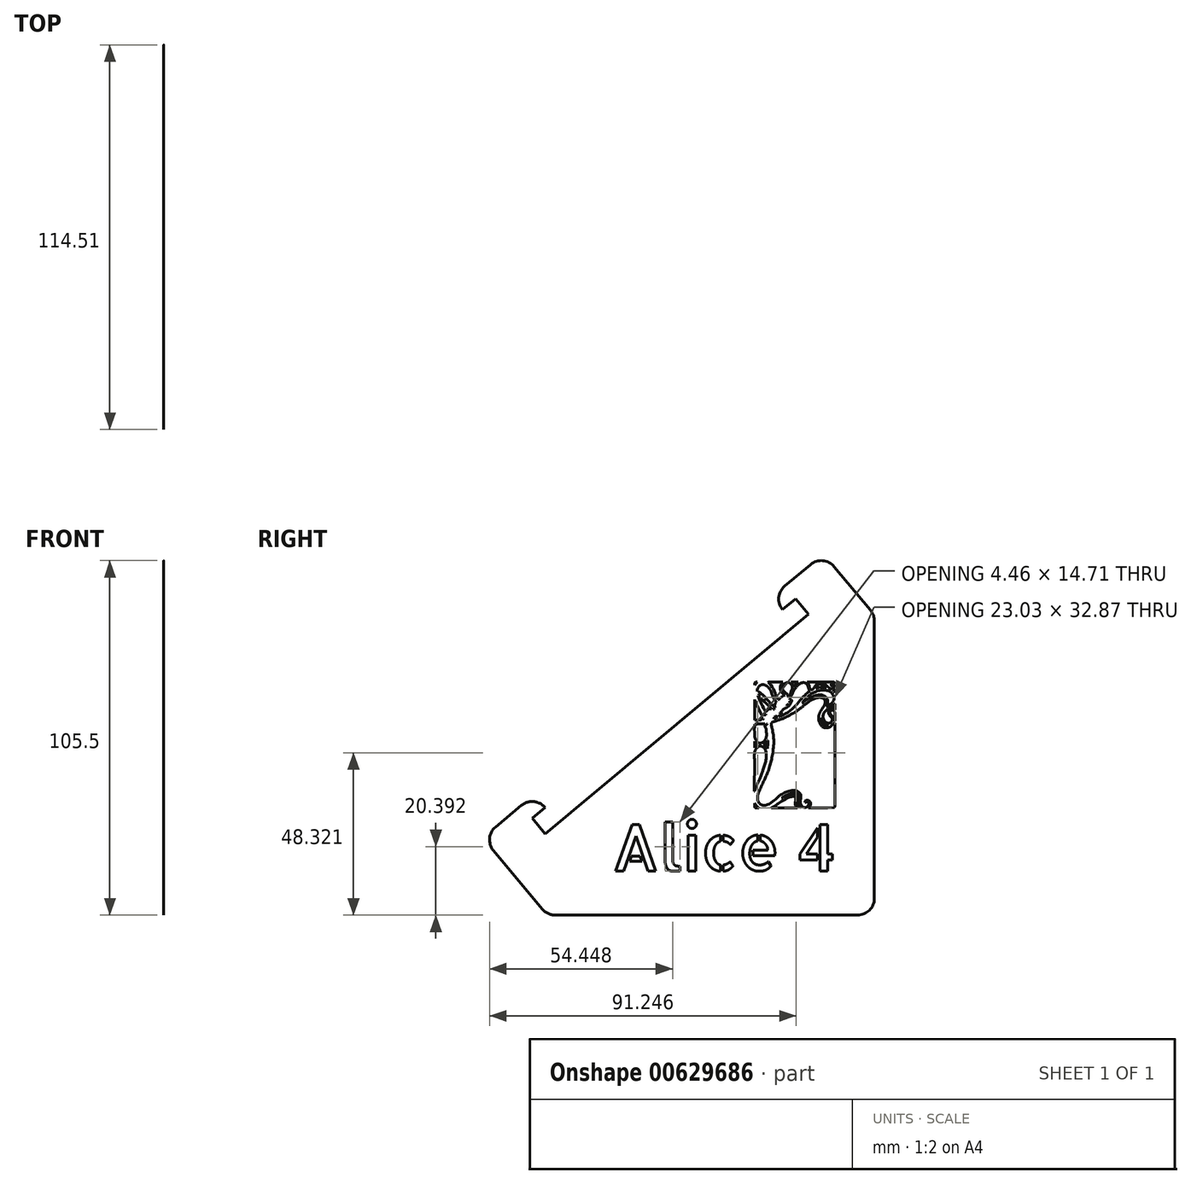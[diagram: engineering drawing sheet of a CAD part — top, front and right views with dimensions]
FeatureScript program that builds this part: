
annotation { "Feature Type Name" : "Feature", "Feature Type Description" : "" }
export const myFeature = defineFeature(function(context is Context, id is Id, definition is map)
    precondition{}
    {
        {
            var Q0;
            Q0=qCreatedBy(makeId("Right.planeOp"),FACE);
            var sketch = newSketch(context, id + "F0", { "sketchPlane" : qUnion([Q0])});
            skLineSegment(sketch, "E0", {"start": v(-36.5, -38.06) * mm, "end": v(41.85, 27.24) * mm});
            skLineSegment(sketch, "E1", {"start": v(41.85, 27.24) * mm, "end": v(38.01, 31.85) * mm});
            skLineSegment(sketch, "E2", {"start": v(38.01, 31.85) * mm, "end": v(34.17, 28.65) * mm});
            skLineSegment(sketch, "E3", {"start": v(34.17, 28.65) * mm, "end": v(34.17, 28.65) * mm});
            skLineSegment(sketch, "E4", {"start": v(-36.5, -38.06) * mm, "end": v(-40.35, -33.45) * mm});
            skLineSegment(sketch, "E5", {"start": v(-40.35, -33.45) * mm, "end": v(-36.5, -30.24) * mm});
            skLineSegment(sketch, "E6", {"start": v(-36.5, -30.24) * mm, "end": v(-36.61, -30.12) * mm});
            skLineSegment(sketch, "E7", {"start": v(-36.5, -30.24) * mm, "end": v(-36.5, -30.24) * mm});
            skLineSegment(sketch, "E8", {"start": v(34.81, 35.7) * mm, "end": v(42.5, 42.1) * mm});
            skLineSegment(sketch, "E9", {"start": v(-43.55, -29.6) * mm, "end": v(-51.23, -36) * mm});
            skLineSegment(sketch, "E10", {"start": v(49.54, 41.46) * mm, "end": v(60.32, 28.52) * mm});
            skLineSegment(sketch, "E11", {"start": v(-51.87, -43.05) * mm, "end": v(-37.36, -60.46) * mm});
            skPoint(sketch, "E12.visualSharp", {"position": v(-35.87, -62.25) * mm});
            skPoint(sketch, "E13.visualSharp", {"position": v(-55.07, -39.2) * mm});
            skArc(sketch, "E13.filletArc", {"start": v(-51.23, -36) * mm, "mid": v(-53, -39.4) * mm, "end": v(-51.87, -43.05) * mm});
            skPoint(sketch, "E14.visualSharp", {"position": v(-39.7, -26.4) * mm});
            skArc(sketch, "E14.filletArc", {"start": v(-36.5, -30.24) * mm, "mid": v(-39.9, -28.47) * mm, "end": v(-43.55, -29.6) * mm});
            skPoint(sketch, "E15.visualSharp", {"position": v(30.97, 32.5) * mm});
            skArc(sketch, "E15.filletArc", {"start": v(34.81, 35.7) * mm, "mid": v(33.03, 32.3) * mm, "end": v(34.17, 28.65) * mm});
            skPoint(sketch, "E16.visualSharp", {"position": v(46.33, 45.3) * mm});
            skArc(sketch, "E16.filletArc", {"start": v(49.54, 41.46) * mm, "mid": v(46.15, 43.23) * mm, "end": v(42.5, 42.1) * mm});
            skLineSegment(sketch, "E17", {"start": v(-33.52, -62.25) * mm, "end": v(56.48, -62.25) * mm});
            skLineSegment(sketch, "E18", {"start": v(61.48, -57.25) * mm, "end": v(61.48, 25.32) * mm});
            skArc(sketch, "E19.filletArc", {"start": v(-37.36, -60.46) * mm, "mid": v(-35.64, -61.78) * mm, "end": v(-33.52, -62.25) * mm});
            skPoint(sketch, "E20.visualSharp", {"position": v(61.48, -62.25) * mm});
            skArc(sketch, "E20.filletArc", {"start": v(56.48, -62.25) * mm, "mid": v(60.01, -60.79) * mm, "end": v(61.48, -57.25) * mm});
            skPoint(sketch, "E21.visualSharp", {"position": v(61.48, 27.13) * mm});
            skArc(sketch, "E21.filletArc", {"start": v(61.48, 25.32) * mm, "mid": v(61.18, 27.02) * mm, "end": v(60.32, 28.52) * mm});
            skText(sketch, "E22", { "text": "Alice 4", "fontName": "AllertaStencil-Regular.ttf"});
            const initialGuessF0  = {"E22": [-0.01667, -0.04912, 1, 0, 0.01387]};
            skSetInitialGuess(sketch, initialGuessF0);
            skSolve(sketch);
        }
        {
            var Q0;
            Q0=makeQuery(id+"F0.imprint","IMPRINT",FACE,{"disambiguationData":[TD([[makeQuery(id+"F0.imprint","IMPRINT",EDGE,{"derivedFrom":sQuery(id+"F0.wireOp",EDGE,"E0")}),-1.0]])]});
            extrude(context, id + "F1", {"entities" : qUnion([Q0]), "depth" : 1 / 203.2 * mm, "offsetDistance" : 25 * mm});
        }
        {
            var Q0;
            Q0=makeQuery(id+"F1.opExtrude","CAP_FACE",FACE,{"disambiguationData":[OSD([sQuery(id+"F0.wireOp",EDGE,"E0"),sQuery(id+"F0.wireOp",EDGE,"E1"),sQuery(id+"F0.wireOp",EDGE,"E2"),sQuery(id+"F0.wireOp",EDGE,"E4"),sQuery(id+"F0.wireOp",EDGE,"E5"),sQuery(id+"F0.wireOp",EDGE,"E8"),sQuery(id+"F0.wireOp",EDGE,"E9"),sQuery(id+"F0.wireOp",EDGE,"E10"),sQuery(id+"F0.wireOp",EDGE,"E11"),sQuery(id+"F0.wireOp",EDGE,"E13.filletArc"),sQuery(id+"F0.wireOp",EDGE,"E14.filletArc"),sQuery(id+"F0.wireOp",EDGE,"E15.filletArc"),sQuery(id+"F0.wireOp",EDGE,"E16.filletArc"),sQuery(id+"F0.wireOp",EDGE,"E17"),sQuery(id+"F0.wireOp",EDGE,"E18"),sQuery(id+"F0.wireOp",EDGE,"E19.filletArc"),sQuery(id+"F0.wireOp",EDGE,"E20.filletArc"),sQuery(id+"F0.wireOp",EDGE,"E21.filletArc"),sQuery(id+"F0.wireOp",EDGE,"E22.sketch_text.stroke-0"),sQuery(id+"F0.wireOp",EDGE,"E22.sketch_text.stroke-1"),sQuery(id+"F0.wireOp",EDGE,"E22.sketch_text.stroke-2"),sQuery(id+"F0.wireOp",EDGE,"E22.sketch_text.stroke-3"),sQuery(id+"F0.wireOp",EDGE,"E22.sketch_text.stroke-4"),sQuery(id+"F0.wireOp",EDGE,"E22.sketch_text.stroke-5"),sQuery(id+"F0.wireOp",EDGE,"E22.sketch_text.stroke-6"),sQuery(id+"F0.wireOp",EDGE,"E22.sketch_text.stroke-7"),sQuery(id+"F0.wireOp",EDGE,"E22.sketch_text.stroke-8"),sQuery(id+"F0.wireOp",EDGE,"E22.sketch_text.stroke-9"),sQuery(id+"F0.wireOp",EDGE,"E22.sketch_text.stroke-10"),sQuery(id+"F0.wireOp",EDGE,"E22.sketch_text.stroke-11"),sQuery(id+"F0.wireOp",EDGE,"E22.sketch_text.stroke-12"),sQuery(id+"F0.wireOp",EDGE,"E22.sketch_text.stroke-13"),sQuery(id+"F0.wireOp",EDGE,"E22.sketch_text.stroke-14"),sQuery(id+"F0.wireOp",EDGE,"E22.sketch_text.stroke-15"),sQuery(id+"F0.wireOp",EDGE,"E22.sketch_text.stroke-16"),sQuery(id+"F0.wireOp",EDGE,"E22.sketch_text.stroke-17"),sQuery(id+"F0.wireOp",EDGE,"E22.sketch_text.stroke-18"),sQuery(id+"F0.wireOp",EDGE,"E22.sketch_text.stroke-19"),sQuery(id+"F0.wireOp",EDGE,"E22.sketch_text.stroke-20"),sQuery(id+"F0.wireOp",EDGE,"E22.sketch_text.stroke-21"),sQuery(id+"F0.wireOp",EDGE,"E22.sketch_text.stroke-22"),sQuery(id+"F0.wireOp",EDGE,"E22.sketch_text.stroke-23"),sQuery(id+"F0.wireOp",EDGE,"E22.sketch_text.stroke-24"),sQuery(id+"F0.wireOp",EDGE,"E22.sketch_text.stroke-25"),sQuery(id+"F0.wireOp",EDGE,"E22.sketch_text.stroke-26"),sQuery(id+"F0.wireOp",EDGE,"E22.sketch_text.stroke-27"),sQuery(id+"F0.wireOp",EDGE,"E22.sketch_text.stroke-28"),sQuery(id+"F0.wireOp",EDGE,"E22.sketch_text.stroke-29"),sQuery(id+"F0.wireOp",EDGE,"E22.sketch_text.stroke-30"),sQuery(id+"F0.wireOp",EDGE,"E22.sketch_text.stroke-31"),sQuery(id+"F0.wireOp",EDGE,"E22.sketch_text.stroke-32"),sQuery(id+"F0.wireOp",EDGE,"E22.sketch_text.stroke-33"),sQuery(id+"F0.wireOp",EDGE,"E22.sketch_text.stroke-34"),sQuery(id+"F0.wireOp",EDGE,"E22.sketch_text.stroke-35"),sQuery(id+"F0.wireOp",EDGE,"E22.sketch_text.stroke-36"),sQuery(id+"F0.wireOp",EDGE,"E22.sketch_text.stroke-37"),sQuery(id+"F0.wireOp",EDGE,"E22.sketch_text.stroke-38"),sQuery(id+"F0.wireOp",EDGE,"E22.sketch_text.stroke-39"),sQuery(id+"F0.wireOp",EDGE,"E22.sketch_text.stroke-40"),sQuery(id+"F0.wireOp",EDGE,"E22.sketch_text.stroke-41"),sQuery(id+"F0.wireOp",EDGE,"E22.sketch_text.stroke-42"),sQuery(id+"F0.wireOp",EDGE,"E22.sketch_text.stroke-43"),sQuery(id+"F0.wireOp",EDGE,"E22.sketch_text.stroke-44"),sQuery(id+"F0.wireOp",EDGE,"E22.sketch_text.stroke-45"),sQuery(id+"F0.wireOp",EDGE,"E22.sketch_text.stroke-46"),sQuery(id+"F0.wireOp",EDGE,"E22.sketch_text.stroke-47"),sQuery(id+"F0.wireOp",EDGE,"E22.sketch_text.stroke-48"),sQuery(id+"F0.wireOp",EDGE,"E22.sketch_text.stroke-49"),sQuery(id+"F0.wireOp",EDGE,"E22.sketch_text.stroke-50"),sQuery(id+"F0.wireOp",EDGE,"E22.sketch_text.stroke-51"),sQuery(id+"F0.wireOp",EDGE,"E22.sketch_text.stroke-52"),sQuery(id+"F0.wireOp",EDGE,"E22.sketch_text.stroke-53"),sQuery(id+"F0.wireOp",EDGE,"E22.sketch_text.stroke-54"),sQuery(id+"F0.wireOp",EDGE,"E22.sketch_text.stroke-55"),sQuery(id+"F0.wireOp",EDGE,"E22.sketch_text.stroke-56"),sQuery(id+"F0.wireOp",EDGE,"E22.sketch_text.stroke-57"),sQuery(id+"F0.wireOp",EDGE,"E22.sketch_text.stroke-58"),sQuery(id+"F0.wireOp",EDGE,"E22.sketch_text.stroke-59"),sQuery(id+"F0.wireOp",EDGE,"E22.sketch_text.stroke-60"),sQuery(id+"F0.wireOp",EDGE,"E22.sketch_text.stroke-61"),sQuery(id+"F0.wireOp",EDGE,"E22.sketch_text.stroke-62"),sQuery(id+"F0.wireOp",EDGE,"E22.sketch_text.stroke-63"),sQuery(id+"F0.wireOp",EDGE,"E22.sketch_text.stroke-64"),sQuery(id+"F0.wireOp",EDGE,"E22.sketch_text.stroke-65"),sQuery(id+"F0.wireOp",EDGE,"E22.sketch_text.stroke-66"),sQuery(id+"F0.wireOp",EDGE,"E22.sketch_text.stroke-67"),sQuery(id+"F0.wireOp",EDGE,"E22.sketch_text.stroke-68"),sQuery(id+"F0.wireOp",EDGE,"E22.sketch_text.stroke-69"),sQuery(id+"F0.wireOp",EDGE,"E22.sketch_text.stroke-70"),sQuery(id+"F0.wireOp",EDGE,"E22.sketch_text.stroke-71"),sQuery(id+"F0.wireOp",EDGE,"E22.sketch_text.stroke-72"),sQuery(id+"F0.wireOp",EDGE,"E22.sketch_text.stroke-73"),sQuery(id+"F0.wireOp",EDGE,"E22.sketch_text.stroke-74"),sQuery(id+"F0.wireOp",EDGE,"E22.sketch_text.stroke-75"),sQuery(id+"F0.wireOp",EDGE,"E22.sketch_text.stroke-76"),sQuery(id+"F0.wireOp",EDGE,"E22.sketch_text.stroke-77"),sQuery(id+"F0.wireOp",EDGE,"E22.sketch_text.stroke-78"),sQuery(id+"F0.wireOp",EDGE,"E22.sketch_text.stroke-79"),sQuery(id+"F0.wireOp",EDGE,"E22.sketch_text.stroke-80"),sQuery(id+"F0.wireOp",EDGE,"E22.sketch_text.stroke-81"),sQuery(id+"F0.wireOp",EDGE,"E22.sketch_text.stroke-82"),sQuery(id+"F0.wireOp",EDGE,"E22.sketch_text.stroke-83"),sQuery(id+"F0.wireOp",EDGE,"E22.sketch_text.stroke-84"),sQuery(id+"F0.wireOp",EDGE,"E22.sketch_text.stroke-85"),sQuery(id+"F0.wireOp",EDGE,"E22.sketch_text.stroke-86"),sQuery(id+"F0.wireOp",EDGE,"E22.sketch_text.stroke-87"),sQuery(id+"F0.wireOp",EDGE,"E22.sketch_text.stroke-88"),sQuery(id+"F0.wireOp",EDGE,"E22.sketch_text.stroke-89"),sQuery(id+"F0.wireOp",EDGE,"E22.sketch_text.stroke-90"),sQuery(id+"F0.wireOp",EDGE,"E22.sketch_text.stroke-91"),sQuery(id+"F0.wireOp",EDGE,"E22.sketch_text.stroke-92"),sQuery(id+"F0.wireOp",EDGE,"E22.sketch_text.stroke-93"),sQuery(id+"F0.wireOp",EDGE,"E22.sketch_text.stroke-94"),sQuery(id+"F0.wireOp",EDGE,"E22.sketch_text.stroke-95"),sQuery(id+"F0.wireOp",EDGE,"E22.sketch_text.stroke-96"),sQuery(id+"F0.wireOp",EDGE,"E22.sketch_text.stroke-97"),sQuery(id+"F0.wireOp",EDGE,"E22.sketch_text.stroke-98"),sQuery(id+"F0.wireOp",EDGE,"E22.sketch_text.stroke-99"),sQuery(id+"F0.wireOp",EDGE,"E22.sketch_text.stroke-100"),sQuery(id+"F0.wireOp",EDGE,"E22.sketch_text.stroke-101"),sQuery(id+"F0.wireOp",EDGE,"E22.sketch_text.stroke-102"),sQuery(id+"F0.wireOp",EDGE,"E22.sketch_text.stroke-103"),sQuery(id+"F0.wireOp",EDGE,"E22.sketch_text.stroke-104"),sQuery(id+"F0.wireOp",EDGE,"E22.sketch_text.stroke-105"),sQuery(id+"F0.wireOp",EDGE,"E22.sketch_text.stroke-106"),sQuery(id+"F0.wireOp",EDGE,"E22.sketch_text.stroke-107"),sQuery(id+"F0.wireOp",EDGE,"E22.sketch_text.stroke-108"),sQuery(id+"F0.wireOp",EDGE,"E22.sketch_text.stroke-109"),sQuery(id+"F0.wireOp",EDGE,"E22.sketch_text.stroke-110"),sQuery(id+"F0.wireOp",EDGE,"E22.sketch_text.stroke-111"),sQuery(id+"F0.wireOp",EDGE,"E22.sketch_text.stroke-112"),sQuery(id+"F0.wireOp",EDGE,"E22.sketch_text.stroke-113"),sQuery(id+"F0.wireOp",EDGE,"E22.sketch_text.stroke-114"),sQuery(id+"F0.wireOp",EDGE,"E22.sketch_text.stroke-115"),sQuery(id+"F0.wireOp",EDGE,"E22.sketch_text.stroke-116"),sQuery(id+"F0.wireOp",EDGE,"E22.sketch_text.stroke-117"),sQuery(id+"F0.wireOp",EDGE,"E22.sketch_text.stroke-118"),sQuery(id+"F0.wireOp",EDGE,"E22.sketch_text.stroke-119"),sQuery(id+"F0.wireOp",EDGE,"E22.sketch_text.stroke-120")])],"isStart":false});
            var sketch = newSketch(context, id + "F2", { "sketchPlane" : qUnion([Q0])});
            skLineSegment(sketch, "E23", {"start": v(41.9, -30.34) * mm, "end": v(41.97, -30.26) * mm});
            skLineSegment(sketch, "E24", {"start": v(41.97, -30.26) * mm, "end": v(42.03, -30.2) * mm});
            skLineSegment(sketch, "E25", {"start": v(42.03, -30.2) * mm, "end": v(42.09, -30.12) * mm});
            skLineSegment(sketch, "E26", {"start": v(42.09, -30.12) * mm, "end": v(42.14, -30.06) * mm});
            skLineSegment(sketch, "E27", {"start": v(42.14, -30.06) * mm, "end": v(42.37, -29.72) * mm});
            skLineSegment(sketch, "E28", {"start": v(42.37, -29.72) * mm, "end": v(42.46, -29.36) * mm});
            skLineSegment(sketch, "E29", {"start": v(42.46, -29.36) * mm, "end": v(42.45, -29) * mm});
            skLineSegment(sketch, "E30", {"start": v(42.45, -29) * mm, "end": v(42.35, -28.61) * mm});
            skLineSegment(sketch, "E31", {"start": v(42.35, -28.61) * mm, "end": v(42.28, -28.44) * mm});
            skLineSegment(sketch, "E32", {"start": v(42.28, -28.44) * mm, "end": v(42.17, -28.28) * mm});
            skLineSegment(sketch, "E33", {"start": v(42.17, -28.28) * mm, "end": v(42.03, -28.17) * mm});
            skLineSegment(sketch, "E34", {"start": v(42.03, -28.17) * mm, "end": v(41.85, -28.1) * mm});
            skLineSegment(sketch, "E35", {"start": v(41.85, -28.1) * mm, "end": v(41.6, -28.06) * mm});
            skLineSegment(sketch, "E36", {"start": v(41.6, -28.06) * mm, "end": v(41.34, -28.06) * mm});
            skLineSegment(sketch, "E37", {"start": v(41.34, -28.06) * mm, "end": v(41.1, -28.12) * mm});
            skLineSegment(sketch, "E38", {"start": v(41.1, -28.12) * mm, "end": v(40.89, -28.3) * mm});
            skLineSegment(sketch, "E39", {"start": v(40.89, -28.3) * mm, "end": v(40.84, -28.38) * mm});
            skLineSegment(sketch, "E40", {"start": v(40.84, -28.38) * mm, "end": v(40.81, -28.45) * mm});
            skLineSegment(sketch, "E41", {"start": v(40.81, -28.45) * mm, "end": v(40.8, -28.52) * mm});
            skLineSegment(sketch, "E42", {"start": v(40.8, -28.52) * mm, "end": v(40.85, -28.6) * mm});
            skLineSegment(sketch, "E43", {"start": v(40.85, -28.6) * mm, "end": v(40.91, -28.65) * mm});
            skLineSegment(sketch, "E44", {"start": v(40.91, -28.65) * mm, "end": v(40.99, -28.69) * mm});
            skLineSegment(sketch, "E45", {"start": v(40.99, -28.69) * mm, "end": v(41.07, -28.7) * mm});
            skLineSegment(sketch, "E46", {"start": v(41.07, -28.7) * mm, "end": v(41.16, -28.66) * mm});
            skLineSegment(sketch, "E47", {"start": v(41.16, -28.66) * mm, "end": v(41.3, -28.6) * mm});
            skLineSegment(sketch, "E48", {"start": v(41.3, -28.6) * mm, "end": v(41.43, -28.55) * mm});
            skLineSegment(sketch, "E49", {"start": v(41.43, -28.55) * mm, "end": v(41.57, -28.54) * mm});
            skLineSegment(sketch, "E50", {"start": v(41.57, -28.54) * mm, "end": v(41.71, -28.57) * mm});
            skLineSegment(sketch, "E51", {"start": v(41.71, -28.57) * mm, "end": v(41.88, -28.66) * mm});
            skLineSegment(sketch, "E52", {"start": v(41.88, -28.66) * mm, "end": v(41.98, -28.8) * mm});
            skLineSegment(sketch, "E53", {"start": v(41.98, -28.8) * mm, "end": v(42.02, -28.96) * mm});
            skLineSegment(sketch, "E54", {"start": v(42.02, -28.96) * mm, "end": v(42, -29.17) * mm});
            skLineSegment(sketch, "E55", {"start": v(42, -29.17) * mm, "end": v(41.93, -29.48) * mm});
            skLineSegment(sketch, "E56", {"start": v(41.93, -29.48) * mm, "end": v(41.78, -29.74) * mm});
            skLineSegment(sketch, "E57", {"start": v(41.78, -29.74) * mm, "end": v(41.57, -29.95) * mm});
            skLineSegment(sketch, "E58", {"start": v(41.57, -29.95) * mm, "end": v(41.31, -30.11) * mm});
            skLineSegment(sketch, "E59", {"start": v(41.31, -30.11) * mm, "end": v(40.94, -30.21) * mm});
            skLineSegment(sketch, "E60", {"start": v(40.94, -30.21) * mm, "end": v(40.54, -30.2) * mm});
            skLineSegment(sketch, "E61", {"start": v(40.54, -30.2) * mm, "end": v(40.15, -30.05) * mm});
            skLineSegment(sketch, "E62", {"start": v(40.15, -30.05) * mm, "end": v(39.83, -29.76) * mm});
            skLineSegment(sketch, "E63", {"start": v(39.83, -29.76) * mm, "end": v(39.67, -29.51) * mm});
            skLineSegment(sketch, "E64", {"start": v(39.67, -29.51) * mm, "end": v(39.55, -29.25) * mm});
            skLineSegment(sketch, "E65", {"start": v(39.55, -29.25) * mm, "end": v(39.47, -28.97) * mm});
            skLineSegment(sketch, "E66", {"start": v(39.47, -28.97) * mm, "end": v(39.43, -28.68) * mm});
            skLineSegment(sketch, "E67", {"start": v(39.43, -28.68) * mm, "end": v(39.43, -28.55) * mm});
            skLineSegment(sketch, "E68", {"start": v(39.43, -28.55) * mm, "end": v(39.43, -28.43) * mm});
            skLineSegment(sketch, "E69", {"start": v(39.43, -28.43) * mm, "end": v(39.44, -28.3) * mm});
            skLineSegment(sketch, "E70", {"start": v(39.44, -28.3) * mm, "end": v(39.46, -28.17) * mm});
            skLineSegment(sketch, "E71", {"start": v(39.46, -28.17) * mm, "end": v(39.5, -28) * mm});
            skLineSegment(sketch, "E72", {"start": v(39.5, -28) * mm, "end": v(39.53, -27.83) * mm});
            skLineSegment(sketch, "E73", {"start": v(39.53, -27.83) * mm, "end": v(39.56, -27.66) * mm});
            skLineSegment(sketch, "E74", {"start": v(39.56, -27.66) * mm, "end": v(39.6, -27.5) * mm});
            skLineSegment(sketch, "E75", {"start": v(39.6, -27.5) * mm, "end": v(39.63, -27) * mm});
            skLineSegment(sketch, "E76", {"start": v(39.63, -27) * mm, "end": v(39.57, -26.54) * mm});
            skLineSegment(sketch, "E77", {"start": v(39.57, -26.54) * mm, "end": v(39.4, -26.12) * mm});
            skLineSegment(sketch, "E78", {"start": v(39.4, -26.12) * mm, "end": v(39.1, -25.74) * mm});
            skLineSegment(sketch, "E79", {"start": v(39.1, -25.74) * mm, "end": v(38.92, -25.6) * mm});
            skLineSegment(sketch, "E80", {"start": v(38.92, -25.6) * mm, "end": v(38.72, -25.5) * mm});
            skLineSegment(sketch, "E81", {"start": v(38.72, -25.5) * mm, "end": v(38.5, -25.4) * mm});
            skLineSegment(sketch, "E82", {"start": v(38.5, -25.4) * mm, "end": v(38.3, -25.31) * mm});
            skLineSegment(sketch, "E83", {"start": v(38.3, -25.31) * mm, "end": v(37.82, -25.17) * mm});
            skLineSegment(sketch, "E84", {"start": v(37.82, -25.17) * mm, "end": v(37.33, -25.13) * mm});
            skLineSegment(sketch, "E85", {"start": v(37.33, -25.13) * mm, "end": v(36.85, -25.16) * mm});
            skLineSegment(sketch, "E86", {"start": v(36.85, -25.16) * mm, "end": v(36.37, -25.28) * mm});
            skLineSegment(sketch, "E87", {"start": v(36.37, -25.28) * mm, "end": v(35.96, -25.4) * mm});
            skLineSegment(sketch, "E88", {"start": v(35.96, -25.4) * mm, "end": v(35.55, -25.53) * mm});
            skLineSegment(sketch, "E89", {"start": v(35.55, -25.53) * mm, "end": v(35.15, -25.68) * mm});
            skLineSegment(sketch, "E90", {"start": v(35.15, -25.68) * mm, "end": v(34.76, -25.84) * mm});
            skLineSegment(sketch, "E91", {"start": v(34.76, -25.84) * mm, "end": v(34.37, -26.03) * mm});
            skLineSegment(sketch, "E92", {"start": v(34.37, -26.03) * mm, "end": v(34, -26.24) * mm});
            skLineSegment(sketch, "E93", {"start": v(34, -26.24) * mm, "end": v(33.63, -26.47) * mm});
            skLineSegment(sketch, "E94", {"start": v(33.63, -26.47) * mm, "end": v(33.27, -26.72) * mm});
            skLineSegment(sketch, "E95", {"start": v(33.27, -26.72) * mm, "end": v(32.86, -27.06) * mm});
            skLineSegment(sketch, "E96", {"start": v(32.86, -27.06) * mm, "end": v(32.46, -27.41) * mm});
            skLineSegment(sketch, "E97", {"start": v(32.46, -27.41) * mm, "end": v(32.06, -27.77) * mm});
            skLineSegment(sketch, "E98", {"start": v(32.06, -27.77) * mm, "end": v(31.65, -28.13) * mm});
            skLineSegment(sketch, "E99", {"start": v(31.65, -28.13) * mm, "end": v(31.18, -28.5) * mm});
            skLineSegment(sketch, "E100", {"start": v(31.18, -28.5) * mm, "end": v(30.7, -28.86) * mm});
            skLineSegment(sketch, "E101", {"start": v(30.7, -28.86) * mm, "end": v(30.18, -29.16) * mm});
            skLineSegment(sketch, "E102", {"start": v(30.18, -29.16) * mm, "end": v(29.61, -29.38) * mm});
            skLineSegment(sketch, "E103", {"start": v(29.61, -29.38) * mm, "end": v(29.46, -29.43) * mm});
            skLineSegment(sketch, "E104", {"start": v(29.46, -29.43) * mm, "end": v(29.31, -29.5) * mm});
            skLineSegment(sketch, "E105", {"start": v(29.31, -29.5) * mm, "end": v(29.16, -29.54) * mm});
            skLineSegment(sketch, "E106", {"start": v(29.16, -29.54) * mm, "end": v(29.01, -29.58) * mm});
            skLineSegment(sketch, "E107", {"start": v(29.01, -29.58) * mm, "end": v(28.87, -29.59) * mm});
            skLineSegment(sketch, "E108", {"start": v(28.87, -29.59) * mm, "end": v(28.73, -29.58) * mm});
            skLineSegment(sketch, "E109", {"start": v(28.73, -29.58) * mm, "end": v(28.58, -29.56) * mm});
            skLineSegment(sketch, "E110", {"start": v(28.58, -29.56) * mm, "end": v(28.44, -29.55) * mm});
            skLineSegment(sketch, "E111", {"start": v(28.44, -29.55) * mm, "end": v(28.4, -29.54) * mm});
            skLineSegment(sketch, "E112", {"start": v(28.4, -29.54) * mm, "end": v(28.35, -29.54) * mm});
            skLineSegment(sketch, "E113", {"start": v(28.35, -29.54) * mm, "end": v(28.31, -29.53) * mm});
            skLineSegment(sketch, "E114", {"start": v(28.31, -29.53) * mm, "end": v(28.27, -29.53) * mm});
            skLineSegment(sketch, "E115", {"start": v(28.27, -29.53) * mm, "end": v(27.97, -29.52) * mm});
            skLineSegment(sketch, "E116", {"start": v(27.97, -29.52) * mm, "end": v(27.71, -29.42) * mm});
            skLineSegment(sketch, "E117", {"start": v(27.71, -29.42) * mm, "end": v(27.49, -29.26) * mm});
            skLineSegment(sketch, "E118", {"start": v(27.49, -29.26) * mm, "end": v(27.3, -29.05) * mm});
            skLineSegment(sketch, "E119", {"start": v(27.3, -29.05) * mm, "end": v(26.97, -28.58) * mm});
            skLineSegment(sketch, "E120", {"start": v(26.97, -28.58) * mm, "end": v(26.77, -28.07) * mm});
            skLineSegment(sketch, "E121", {"start": v(26.77, -28.07) * mm, "end": v(26.7, -27.53) * mm});
            skLineSegment(sketch, "E122", {"start": v(26.7, -27.53) * mm, "end": v(26.74, -26.96) * mm});
            skLineSegment(sketch, "E123", {"start": v(26.74, -26.96) * mm, "end": v(26.77, -26.77) * mm});
            skLineSegment(sketch, "E124", {"start": v(26.77, -26.77) * mm, "end": v(26.8, -26.57) * mm});
            skLineSegment(sketch, "E125", {"start": v(26.8, -26.57) * mm, "end": v(26.82, -26.39) * mm});
            skLineSegment(sketch, "E126", {"start": v(26.82, -26.39) * mm, "end": v(26.87, -26.2) * mm});
            skLineSegment(sketch, "E127", {"start": v(26.87, -26.2) * mm, "end": v(27.05, -25.77) * mm});
            skLineSegment(sketch, "E128", {"start": v(27.05, -25.77) * mm, "end": v(27.23, -25.33) * mm});
            skLineSegment(sketch, "E129", {"start": v(27.23, -25.33) * mm, "end": v(27.43, -24.9) * mm});
            skLineSegment(sketch, "E130", {"start": v(27.43, -24.9) * mm, "end": v(27.62, -24.47) * mm});
            skLineSegment(sketch, "E131", {"start": v(27.62, -24.47) * mm, "end": v(27.82, -24) * mm});
            skLineSegment(sketch, "E132", {"start": v(27.82, -24) * mm, "end": v(28.03, -23.54) * mm});
            skLineSegment(sketch, "E133", {"start": v(28.03, -23.54) * mm, "end": v(28.24, -23.07) * mm});
            skLineSegment(sketch, "E134", {"start": v(28.24, -23.07) * mm, "end": v(28.45, -22.6) * mm});
            skLineSegment(sketch, "E135", {"start": v(28.45, -22.6) * mm, "end": v(28.55, -22.39) * mm});
            skLineSegment(sketch, "E136", {"start": v(28.55, -22.39) * mm, "end": v(28.65, -22.17) * mm});
            skLineSegment(sketch, "E137", {"start": v(28.65, -22.17) * mm, "end": v(28.75, -21.95) * mm});
            skLineSegment(sketch, "E138", {"start": v(28.75, -21.95) * mm, "end": v(28.85, -21.73) * mm});
            skLineSegment(sketch, "E139", {"start": v(28.85, -21.73) * mm, "end": v(29.03, -21.33) * mm});
            skLineSegment(sketch, "E140", {"start": v(29.03, -21.33) * mm, "end": v(29.22, -20.93) * mm});
            skLineSegment(sketch, "E141", {"start": v(29.22, -20.93) * mm, "end": v(29.4, -20.54) * mm});
            skLineSegment(sketch, "E142", {"start": v(29.4, -20.54) * mm, "end": v(29.58, -20.14) * mm});
            skLineSegment(sketch, "E143", {"start": v(29.58, -20.14) * mm, "end": v(29.65, -19.95) * mm});
            skLineSegment(sketch, "E144", {"start": v(29.65, -19.95) * mm, "end": v(29.72, -19.76) * mm});
            skLineSegment(sketch, "E145", {"start": v(29.72, -19.76) * mm, "end": v(29.79, -19.57) * mm});
            skLineSegment(sketch, "E146", {"start": v(29.79, -19.57) * mm, "end": v(29.87, -19.39) * mm});
            skLineSegment(sketch, "E147", {"start": v(29.87, -19.39) * mm, "end": v(30.06, -18.92) * mm});
            skLineSegment(sketch, "E148", {"start": v(30.06, -18.92) * mm, "end": v(30.2, -18.45) * mm});
            skLineSegment(sketch, "E149", {"start": v(30.2, -18.45) * mm, "end": v(30.34, -17.97) * mm});
            skLineSegment(sketch, "E150", {"start": v(30.34, -17.97) * mm, "end": v(30.47, -17.49) * mm});
            skLineSegment(sketch, "E151", {"start": v(30.47, -17.49) * mm, "end": v(30.58, -17.1) * mm});
            skLineSegment(sketch, "E152", {"start": v(30.58, -17.1) * mm, "end": v(30.7, -16.7) * mm});
            skLineSegment(sketch, "E153", {"start": v(30.7, -16.7) * mm, "end": v(30.8, -16.3) * mm});
            skLineSegment(sketch, "E154", {"start": v(30.8, -16.3) * mm, "end": v(30.9, -15.89) * mm});
            skLineSegment(sketch, "E155", {"start": v(30.9, -15.89) * mm, "end": v(31, -15.4) * mm});
            skLineSegment(sketch, "E156", {"start": v(31, -15.4) * mm, "end": v(31.1, -14.9) * mm});
            skLineSegment(sketch, "E157", {"start": v(31.1, -14.9) * mm, "end": v(31.2, -14.42) * mm});
            skLineSegment(sketch, "E158", {"start": v(31.2, -14.42) * mm, "end": v(31.28, -13.92) * mm});
            skLineSegment(sketch, "E159", {"start": v(31.28, -13.92) * mm, "end": v(31.33, -13.54) * mm});
            skLineSegment(sketch, "E160", {"start": v(31.33, -13.54) * mm, "end": v(31.36, -13.16) * mm});
            skLineSegment(sketch, "E161", {"start": v(31.36, -13.16) * mm, "end": v(31.38, -12.77) * mm});
            skLineSegment(sketch, "E162", {"start": v(31.38, -12.77) * mm, "end": v(31.41, -12.39) * mm});
            skLineSegment(sketch, "E163", {"start": v(31.41, -12.39) * mm, "end": v(31.45, -12.06) * mm});
            skLineSegment(sketch, "E164", {"start": v(31.45, -12.06) * mm, "end": v(31.49, -11.73) * mm});
            skLineSegment(sketch, "E165", {"start": v(31.49, -11.73) * mm, "end": v(31.52, -11.4) * mm});
            skLineSegment(sketch, "E166", {"start": v(31.52, -11.4) * mm, "end": v(31.55, -11.07) * mm});
            skLineSegment(sketch, "E167", {"start": v(31.55, -11.07) * mm, "end": v(31.56, -10.82) * mm});
            skLineSegment(sketch, "E168", {"start": v(31.56, -10.82) * mm, "end": v(31.55, -10.57) * mm});
            skLineSegment(sketch, "E169", {"start": v(31.55, -10.57) * mm, "end": v(31.54, -10.32) * mm});
            skLineSegment(sketch, "E170", {"start": v(31.54, -10.32) * mm, "end": v(31.52, -10.07) * mm});
            skLineSegment(sketch, "E171", {"start": v(31.52, -10.07) * mm, "end": v(31.5, -9.71) * mm});
            skLineSegment(sketch, "E172", {"start": v(31.5, -9.71) * mm, "end": v(31.48, -9.35) * mm});
            skLineSegment(sketch, "E173", {"start": v(31.48, -9.35) * mm, "end": v(31.46, -9) * mm});
            skLineSegment(sketch, "E174", {"start": v(31.46, -9) * mm, "end": v(31.42, -8.64) * mm});
            skLineSegment(sketch, "E175", {"start": v(31.42, -8.64) * mm, "end": v(31.34, -8.17) * mm});
            skLineSegment(sketch, "E176", {"start": v(31.34, -8.17) * mm, "end": v(31.25, -7.7) * mm});
            skLineSegment(sketch, "E177", {"start": v(31.25, -7.7) * mm, "end": v(31.15, -7.22) * mm});
            skLineSegment(sketch, "E178", {"start": v(31.15, -7.22) * mm, "end": v(31.05, -6.75) * mm});
            skLineSegment(sketch, "E179", {"start": v(31.05, -6.75) * mm, "end": v(30.98, -6.46) * mm});
            skLineSegment(sketch, "E180", {"start": v(30.98, -6.46) * mm, "end": v(30.9, -6.17) * mm});
            skLineSegment(sketch, "E181", {"start": v(30.9, -6.17) * mm, "end": v(30.83, -5.87) * mm});
            skLineSegment(sketch, "E182", {"start": v(30.83, -5.87) * mm, "end": v(30.76, -5.58) * mm});
            skLineSegment(sketch, "E183", {"start": v(30.76, -5.58) * mm, "end": v(30.75, -5.5) * mm});
            skLineSegment(sketch, "E184", {"start": v(30.75, -5.5) * mm, "end": v(30.76, -5.43) * mm});
            skLineSegment(sketch, "E185", {"start": v(30.76, -5.43) * mm, "end": v(30.78, -5.36) * mm});
            skLineSegment(sketch, "E186", {"start": v(30.78, -5.36) * mm, "end": v(30.8, -5.28) * mm});
            skLineSegment(sketch, "E187", {"start": v(30.8, -5.28) * mm, "end": v(30.84, -5.2) * mm});
            skLineSegment(sketch, "E188", {"start": v(30.84, -5.2) * mm, "end": v(30.88, -5.13) * mm});
            skLineSegment(sketch, "E189", {"start": v(30.88, -5.13) * mm, "end": v(30.92, -5.05) * mm});
            skLineSegment(sketch, "E190", {"start": v(30.92, -5.05) * mm, "end": v(30.97, -4.97) * mm});
            skLineSegment(sketch, "E191", {"start": v(30.97, -4.97) * mm, "end": v(31.03, -4.87) * mm});
            skLineSegment(sketch, "E192", {"start": v(31.03, -4.87) * mm, "end": v(31.12, -4.8) * mm});
            skLineSegment(sketch, "E193", {"start": v(31.12, -4.8) * mm, "end": v(31.22, -4.73) * mm});
            skLineSegment(sketch, "E194", {"start": v(31.22, -4.73) * mm, "end": v(31.34, -4.7) * mm});
            skLineSegment(sketch, "E195", {"start": v(31.34, -4.7) * mm, "end": v(31.56, -4.65) * mm});
            skLineSegment(sketch, "E196", {"start": v(31.56, -4.65) * mm, "end": v(31.77, -4.59) * mm});
            skLineSegment(sketch, "E197", {"start": v(31.77, -4.59) * mm, "end": v(31.98, -4.52) * mm});
            skLineSegment(sketch, "E198", {"start": v(31.98, -4.52) * mm, "end": v(32.2, -4.45) * mm});
            skLineSegment(sketch, "E199", {"start": v(32.2, -4.45) * mm, "end": v(32.32, -4.42) * mm});
            skLineSegment(sketch, "E200", {"start": v(32.32, -4.42) * mm, "end": v(32.45, -4.39) * mm});
            skLineSegment(sketch, "E201", {"start": v(32.45, -4.39) * mm, "end": v(32.57, -4.36) * mm});
            skLineSegment(sketch, "E202", {"start": v(32.57, -4.36) * mm, "end": v(32.7, -4.32) * mm});
            skLineSegment(sketch, "E203", {"start": v(32.7, -4.32) * mm, "end": v(32.9, -4.24) * mm});
            skLineSegment(sketch, "E204", {"start": v(32.9, -4.24) * mm, "end": v(33.1, -4.17) * mm});
            skLineSegment(sketch, "E205", {"start": v(33.1, -4.17) * mm, "end": v(33.3, -4.1) * mm});
            skLineSegment(sketch, "E206", {"start": v(33.3, -4.1) * mm, "end": v(33.5, -4.02) * mm});
            skLineSegment(sketch, "E207", {"start": v(33.5, -4.02) * mm, "end": v(33.57, -4) * mm});
            skLineSegment(sketch, "E208", {"start": v(33.57, -4) * mm, "end": v(33.64, -3.98) * mm});
            skLineSegment(sketch, "E209", {"start": v(33.64, -3.98) * mm, "end": v(33.7, -3.97) * mm});
            skLineSegment(sketch, "E210", {"start": v(33.7, -3.97) * mm, "end": v(33.76, -3.95) * mm});
            skLineSegment(sketch, "E211", {"start": v(33.76, -3.95) * mm, "end": v(34, -3.85) * mm});
            skLineSegment(sketch, "E212", {"start": v(34, -3.85) * mm, "end": v(34.22, -3.75) * mm});
            skLineSegment(sketch, "E213", {"start": v(34.22, -3.75) * mm, "end": v(34.45, -3.65) * mm});
            skLineSegment(sketch, "E214", {"start": v(34.45, -3.65) * mm, "end": v(34.68, -3.55) * mm});
            skLineSegment(sketch, "E215", {"start": v(34.68, -3.55) * mm, "end": v(35.03, -3.38) * mm});
            skLineSegment(sketch, "E216", {"start": v(35.03, -3.38) * mm, "end": v(35.38, -3.22) * mm});
            skLineSegment(sketch, "E217", {"start": v(35.38, -3.22) * mm, "end": v(35.73, -3.05) * mm});
            skLineSegment(sketch, "E218", {"start": v(35.73, -3.05) * mm, "end": v(36.08, -2.87) * mm});
            skLineSegment(sketch, "E219", {"start": v(36.08, -2.87) * mm, "end": v(36.33, -2.74) * mm});
            skLineSegment(sketch, "E220", {"start": v(36.33, -2.74) * mm, "end": v(36.6, -2.6) * mm});
            skLineSegment(sketch, "E221", {"start": v(36.6, -2.6) * mm, "end": v(36.84, -2.44) * mm});
            skLineSegment(sketch, "E222", {"start": v(36.84, -2.44) * mm, "end": v(37.1, -2.3) * mm});
            skLineSegment(sketch, "E223", {"start": v(37.1, -2.3) * mm, "end": v(37.2, -2.25) * mm});
            skLineSegment(sketch, "E224", {"start": v(37.2, -2.25) * mm, "end": v(37.32, -2.2) * mm});
            skLineSegment(sketch, "E225", {"start": v(37.32, -2.2) * mm, "end": v(37.43, -2.16) * mm});
            skLineSegment(sketch, "E226", {"start": v(37.43, -2.16) * mm, "end": v(37.54, -2.1) * mm});
            skLineSegment(sketch, "E227", {"start": v(37.54, -2.1) * mm, "end": v(37.62, -2.06) * mm});
            skLineSegment(sketch, "E228", {"start": v(37.62, -2.06) * mm, "end": v(37.7, -2) * mm});
            skLineSegment(sketch, "E229", {"start": v(37.7, -2) * mm, "end": v(37.78, -1.95) * mm});
            skLineSegment(sketch, "E230", {"start": v(37.78, -1.95) * mm, "end": v(37.86, -1.9) * mm});
            skLineSegment(sketch, "E231", {"start": v(37.86, -1.9) * mm, "end": v(38.05, -1.77) * mm});
            skLineSegment(sketch, "E232", {"start": v(38.05, -1.77) * mm, "end": v(38.23, -1.64) * mm});
            skLineSegment(sketch, "E233", {"start": v(38.23, -1.64) * mm, "end": v(38.42, -1.5) * mm});
            skLineSegment(sketch, "E234", {"start": v(38.42, -1.5) * mm, "end": v(38.6, -1.37) * mm});
            skLineSegment(sketch, "E235", {"start": v(38.6, -1.37) * mm, "end": v(38.84, -1.18) * mm});
            skLineSegment(sketch, "E236", {"start": v(38.84, -1.18) * mm, "end": v(39.08, -1) * mm});
            skLineSegment(sketch, "E237", {"start": v(39.08, -1) * mm, "end": v(39.32, -0.8) * mm});
            skLineSegment(sketch, "E238", {"start": v(39.32, -0.8) * mm, "end": v(39.56, -0.61) * mm});
            skLineSegment(sketch, "E239", {"start": v(39.56, -0.61) * mm, "end": v(39.77, -0.45) * mm});
            skLineSegment(sketch, "E240", {"start": v(39.77, -0.45) * mm, "end": v(40, -0.28) * mm});
            skLineSegment(sketch, "E241", {"start": v(40, -0.28) * mm, "end": v(40.2, -0.1) * mm});
            skLineSegment(sketch, "E242", {"start": v(40.2, -0.1) * mm, "end": v(40.42, 0.06) * mm});
            skLineSegment(sketch, "E243", {"start": v(40.42, 0.06) * mm, "end": v(40.6, 0.2) * mm});
            skLineSegment(sketch, "E244", {"start": v(40.6, 0.2) * mm, "end": v(40.77, 0.36) * mm});
            skLineSegment(sketch, "E245", {"start": v(40.77, 0.36) * mm, "end": v(40.95, 0.5) * mm});
            skLineSegment(sketch, "E246", {"start": v(40.95, 0.5) * mm, "end": v(41.13, 0.65) * mm});
            skLineSegment(sketch, "E247", {"start": v(41.13, 0.65) * mm, "end": v(41.3, 0.78) * mm});
            skLineSegment(sketch, "E248", {"start": v(41.3, 0.78) * mm, "end": v(41.48, 0.9) * mm});
            skLineSegment(sketch, "E249", {"start": v(41.48, 0.9) * mm, "end": v(41.65, 1.04) * mm});
            skLineSegment(sketch, "E250", {"start": v(41.65, 1.04) * mm, "end": v(41.83, 1.17) * mm});
            skLineSegment(sketch, "E251", {"start": v(41.83, 1.17) * mm, "end": v(42.18, 1.43) * mm});
            skLineSegment(sketch, "E252", {"start": v(42.18, 1.43) * mm, "end": v(42.56, 1.65) * mm});
            skLineSegment(sketch, "E253", {"start": v(42.56, 1.65) * mm, "end": v(42.95, 1.86) * mm});
            skLineSegment(sketch, "E254", {"start": v(42.95, 1.86) * mm, "end": v(43.33, 2.06) * mm});
            skLineSegment(sketch, "E255", {"start": v(43.33, 2.06) * mm, "end": v(43.53, 2.15) * mm});
            skLineSegment(sketch, "E256", {"start": v(43.53, 2.15) * mm, "end": v(43.74, 2.21) * mm});
            skLineSegment(sketch, "E257", {"start": v(43.74, 2.21) * mm, "end": v(43.95, 2.27) * mm});
            skLineSegment(sketch, "E258", {"start": v(43.95, 2.27) * mm, "end": v(44.17, 2.32) * mm});
            skLineSegment(sketch, "E259", {"start": v(44.17, 2.32) * mm, "end": v(44.3, 2.36) * mm});
            skLineSegment(sketch, "E260", {"start": v(44.3, 2.36) * mm, "end": v(44.44, 2.4) * mm});
            skLineSegment(sketch, "E261", {"start": v(44.44, 2.4) * mm, "end": v(44.58, 2.44) * mm});
            skLineSegment(sketch, "E262", {"start": v(44.58, 2.44) * mm, "end": v(44.72, 2.47) * mm});
            skLineSegment(sketch, "E263", {"start": v(44.72, 2.47) * mm, "end": v(45.04, 2.5) * mm});
            skLineSegment(sketch, "E264", {"start": v(45.04, 2.5) * mm, "end": v(45.35, 2.49) * mm});
            skLineSegment(sketch, "E265", {"start": v(45.35, 2.49) * mm, "end": v(45.67, 2.43) * mm});
            skLineSegment(sketch, "E266", {"start": v(45.67, 2.43) * mm, "end": v(45.98, 2.37) * mm});
            skLineSegment(sketch, "E267", {"start": v(45.98, 2.37) * mm, "end": v(46.21, 2.29) * mm});
            skLineSegment(sketch, "E268", {"start": v(46.21, 2.29) * mm, "end": v(46.4, 2.15) * mm});
            skLineSegment(sketch, "E269", {"start": v(46.4, 2.15) * mm, "end": v(46.56, 2) * mm});
            skLineSegment(sketch, "E270", {"start": v(46.56, 2) * mm, "end": v(46.72, 1.83) * mm});
            skLineSegment(sketch, "E271", {"start": v(46.72, 1.83) * mm, "end": v(46.77, 1.75) * mm});
            skLineSegment(sketch, "E272", {"start": v(46.77, 1.75) * mm, "end": v(46.8, 1.65) * mm});
            skLineSegment(sketch, "E273", {"start": v(46.8, 1.65) * mm, "end": v(46.82, 1.55) * mm});
            skLineSegment(sketch, "E274", {"start": v(46.82, 1.55) * mm, "end": v(46.84, 1.44) * mm});
            skLineSegment(sketch, "E275", {"start": v(46.84, 1.44) * mm, "end": v(46.88, 1.07) * mm});
            skLineSegment(sketch, "E276", {"start": v(46.88, 1.07) * mm, "end": v(46.84, 0.71) * mm});
            skLineSegment(sketch, "E277", {"start": v(46.84, 0.71) * mm, "end": v(46.72, 0.37) * mm});
            skLineSegment(sketch, "E278", {"start": v(46.72, 0.37) * mm, "end": v(46.55, 0.05) * mm});
            skLineSegment(sketch, "E279", {"start": v(46.55, 0.05) * mm, "end": v(46.25, -0.4) * mm});
            skLineSegment(sketch, "E280", {"start": v(46.25, -0.4) * mm, "end": v(45.95, -0.86) * mm});
            skLineSegment(sketch, "E281", {"start": v(45.95, -0.86) * mm, "end": v(45.65, -1.31) * mm});
            skLineSegment(sketch, "E282", {"start": v(45.65, -1.31) * mm, "end": v(45.35, -1.77) * mm});
            skLineSegment(sketch, "E283", {"start": v(45.35, -1.77) * mm, "end": v(45.3, -1.88) * mm});
            skLineSegment(sketch, "E284", {"start": v(45.3, -1.88) * mm, "end": v(45.24, -2) * mm});
            skLineSegment(sketch, "E285", {"start": v(45.24, -2) * mm, "end": v(45.2, -2.14) * mm});
            skLineSegment(sketch, "E286", {"start": v(45.2, -2.14) * mm, "end": v(45.15, -2.27) * mm});
            skLineSegment(sketch, "E287", {"start": v(45.15, -2.27) * mm, "end": v(45.09, -2.45) * mm});
            skLineSegment(sketch, "E288", {"start": v(45.09, -2.45) * mm, "end": v(45.02, -2.64) * mm});
            skLineSegment(sketch, "E289", {"start": v(45.02, -2.64) * mm, "end": v(44.96, -2.83) * mm});
            skLineSegment(sketch, "E290", {"start": v(44.96, -2.83) * mm, "end": v(44.92, -3.03) * mm});
            skLineSegment(sketch, "E291", {"start": v(44.92, -3.03) * mm, "end": v(44.9, -3.22) * mm});
            skLineSegment(sketch, "E292", {"start": v(44.9, -3.22) * mm, "end": v(44.89, -3.42) * mm});
            skLineSegment(sketch, "E293", {"start": v(44.89, -3.42) * mm, "end": v(44.9, -3.61) * mm});
            skLineSegment(sketch, "E294", {"start": v(44.9, -3.61) * mm, "end": v(44.9, -3.81) * mm});
            skLineSegment(sketch, "E295", {"start": v(44.9, -3.81) * mm, "end": v(44.9, -3.97) * mm});
            skLineSegment(sketch, "E296", {"start": v(44.9, -3.97) * mm, "end": v(44.92, -4.13) * mm});
            skLineSegment(sketch, "E297", {"start": v(44.92, -4.13) * mm, "end": v(44.94, -4.29) * mm});
            skLineSegment(sketch, "E298", {"start": v(44.94, -4.29) * mm, "end": v(44.96, -4.44) * mm});
            skLineSegment(sketch, "E299", {"start": v(44.96, -4.44) * mm, "end": v(45, -4.59) * mm});
            skLineSegment(sketch, "E300", {"start": v(45, -4.59) * mm, "end": v(45.04, -4.73) * mm});
            skLineSegment(sketch, "E301", {"start": v(45.04, -4.73) * mm, "end": v(45.09, -4.87) * mm});
            skLineSegment(sketch, "E302", {"start": v(45.09, -4.87) * mm, "end": v(45.15, -5) * mm});
            skLineSegment(sketch, "E303", {"start": v(45.15, -5) * mm, "end": v(45.29, -5.26) * mm});
            skLineSegment(sketch, "E304", {"start": v(45.29, -5.26) * mm, "end": v(45.43, -5.52) * mm});
            skLineSegment(sketch, "E305", {"start": v(45.43, -5.52) * mm, "end": v(45.6, -5.77) * mm});
            skLineSegment(sketch, "E306", {"start": v(45.6, -5.77) * mm, "end": v(45.77, -6) * mm});
            skLineSegment(sketch, "E307", {"start": v(45.77, -6) * mm, "end": v(46, -6.2) * mm});
            skLineSegment(sketch, "E308", {"start": v(46, -6.2) * mm, "end": v(46.27, -6.36) * mm});
            skLineSegment(sketch, "E309", {"start": v(46.27, -6.36) * mm, "end": v(46.56, -6.45) * mm});
            skLineSegment(sketch, "E310", {"start": v(46.56, -6.45) * mm, "end": v(46.88, -6.5) * mm});
            skLineSegment(sketch, "E311", {"start": v(46.88, -6.5) * mm, "end": v(47.1, -6.51) * mm});
            skLineSegment(sketch, "E312", {"start": v(47.1, -6.51) * mm, "end": v(47.34, -6.52) * mm});
            skLineSegment(sketch, "E313", {"start": v(47.34, -6.52) * mm, "end": v(47.57, -6.5) * mm});
            skLineSegment(sketch, "E314", {"start": v(47.57, -6.5) * mm, "end": v(47.8, -6.47) * mm});
            skLineSegment(sketch, "E315", {"start": v(47.8, -6.47) * mm, "end": v(47.97, -6.4) * mm});
            skLineSegment(sketch, "E316", {"start": v(47.97, -6.4) * mm, "end": v(48.13, -6.32) * mm});
            skLineSegment(sketch, "E317", {"start": v(48.13, -6.32) * mm, "end": v(48.29, -6.2) * mm});
            skLineSegment(sketch, "E318", {"start": v(48.29, -6.2) * mm, "end": v(48.44, -6.09) * mm});
            skLineSegment(sketch, "E319", {"start": v(48.44, -6.09) * mm, "end": v(48.62, -5.92) * mm});
            skLineSegment(sketch, "E320", {"start": v(48.62, -5.92) * mm, "end": v(48.8, -5.75) * mm});
            skLineSegment(sketch, "E321", {"start": v(48.8, -5.75) * mm, "end": v(48.96, -5.57) * mm});
            skLineSegment(sketch, "E322", {"start": v(48.96, -5.57) * mm, "end": v(49.14, -5.4) * mm});
            skLineSegment(sketch, "E323", {"start": v(49.14, -5.4) * mm, "end": v(49.21, -5.33) * mm});
            skLineSegment(sketch, "E324", {"start": v(49.21, -5.33) * mm, "end": v(49.29, -5.26) * mm});
            skLineSegment(sketch, "E325", {"start": v(49.29, -5.26) * mm, "end": v(49.37, -5.2) * mm});
            skLineSegment(sketch, "E326", {"start": v(49.37, -5.2) * mm, "end": v(49.45, -5.14) * mm});
            skLineSegment(sketch, "E327", {"start": v(49.45, -5.14) * mm, "end": v(49.56, -5.08) * mm});
            skLineSegment(sketch, "E328", {"start": v(49.56, -5.08) * mm, "end": v(49.65, -5.08) * mm});
            skLineSegment(sketch, "E329", {"start": v(49.65, -5.08) * mm, "end": v(49.7, -5.14) * mm});
            skLineSegment(sketch, "E330", {"start": v(49.7, -5.14) * mm, "end": v(49.73, -5.26) * mm});
            skLineSegment(sketch, "E331", {"start": v(49.73, -5.26) * mm, "end": v(49.73, -5.4) * mm});
            skLineSegment(sketch, "E332", {"start": v(49.73, -5.4) * mm, "end": v(49.73, -5.52) * mm});
            skLineSegment(sketch, "E333", {"start": v(49.73, -5.52) * mm, "end": v(49.72, -5.65) * mm});
            skLineSegment(sketch, "E334", {"start": v(49.72, -5.65) * mm, "end": v(49.72, -5.78) * mm});
            skLineSegment(sketch, "E335", {"start": v(49.72, -5.78) * mm, "end": v(49.72, -10.78) * mm});
            skLineSegment(sketch, "E336", {"start": v(49.72, -10.78) * mm, "end": v(49.72, -15.78) * mm});
            skLineSegment(sketch, "E337", {"start": v(49.72, -15.78) * mm, "end": v(49.72, -20.78) * mm});
            skLineSegment(sketch, "E338", {"start": v(49.72, -20.78) * mm, "end": v(49.72, -25.78) * mm});
            skLineSegment(sketch, "E339", {"start": v(49.72, -25.78) * mm, "end": v(49.72, -26.37) * mm});
            skLineSegment(sketch, "E340", {"start": v(49.72, -26.37) * mm, "end": v(49.73, -26.96) * mm});
            skLineSegment(sketch, "E341", {"start": v(49.73, -26.96) * mm, "end": v(49.73, -27.55) * mm});
            skLineSegment(sketch, "E342", {"start": v(49.73, -27.55) * mm, "end": v(49.73, -28.14) * mm});
            skLineSegment(sketch, "E343", {"start": v(49.73, -28.14) * mm, "end": v(49.73, -28.52) * mm});
            skLineSegment(sketch, "E344", {"start": v(49.73, -28.52) * mm, "end": v(49.73, -28.9) * mm});
            skLineSegment(sketch, "E345", {"start": v(49.73, -28.9) * mm, "end": v(49.72, -29.27) * mm});
            skLineSegment(sketch, "E346", {"start": v(49.72, -29.27) * mm, "end": v(49.71, -29.65) * mm});
            skLineSegment(sketch, "E347", {"start": v(49.71, -29.65) * mm, "end": v(49.7, -29.74) * mm});
            skLineSegment(sketch, "E348", {"start": v(49.7, -29.74) * mm, "end": v(49.7, -29.84) * mm});
            skLineSegment(sketch, "E349", {"start": v(49.7, -29.84) * mm, "end": v(49.7, -29.93) * mm});
            skLineSegment(sketch, "E350", {"start": v(49.7, -29.93) * mm, "end": v(49.68, -30.02) * mm});
            skLineSegment(sketch, "E351", {"start": v(49.68, -30.02) * mm, "end": v(49.65, -30.13) * mm});
            skLineSegment(sketch, "E352", {"start": v(49.65, -30.13) * mm, "end": v(49.6, -30.21) * mm});
            skLineSegment(sketch, "E353", {"start": v(49.6, -30.21) * mm, "end": v(49.51, -30.26) * mm});
            skLineSegment(sketch, "E354", {"start": v(49.51, -30.26) * mm, "end": v(49.39, -30.29) * mm});
            skLineSegment(sketch, "E355", {"start": v(49.39, -30.29) * mm, "end": v(47.54, -30.36) * mm});
            skLineSegment(sketch, "E356", {"start": v(47.54, -30.36) * mm, "end": v(45.68, -30.37) * mm});
            skLineSegment(sketch, "E357", {"start": v(45.68, -30.37) * mm, "end": v(43.83, -30.35) * mm});
            skLineSegment(sketch, "E358", {"start": v(43.83, -30.35) * mm, "end": v(41.98, -30.36) * mm});
            skLineSegment(sketch, "E359", {"start": v(41.98, -30.36) * mm, "end": v(41.97, -30.35) * mm});
            skLineSegment(sketch, "E360", {"start": v(41.97, -30.35) * mm, "end": v(41.96, -30.35) * mm});
            skLineSegment(sketch, "E361", {"start": v(41.96, -30.35) * mm, "end": v(41.94, -30.35) * mm});
            skLineSegment(sketch, "E362", {"start": v(41.94, -30.35) * mm, "end": v(41.9, -30.34) * mm});
            skLineSegment(sketch, "E363", {"start": v(25.79, -25.44) * mm, "end": v(25.79, -24.69) * mm});
            skLineSegment(sketch, "E364", {"start": v(25.79, -24.69) * mm, "end": v(25.79, -23.93) * mm});
            skLineSegment(sketch, "E365", {"start": v(25.79, -23.93) * mm, "end": v(25.79, -23.18) * mm});
            skLineSegment(sketch, "E366", {"start": v(25.79, -23.18) * mm, "end": v(25.79, -22.42) * mm});
            skLineSegment(sketch, "E367", {"start": v(25.79, -22.42) * mm, "end": v(25.8, -21.34) * mm});
            skLineSegment(sketch, "E368", {"start": v(25.8, -21.34) * mm, "end": v(25.8, -20.25) * mm});
            skLineSegment(sketch, "E369", {"start": v(25.8, -20.25) * mm, "end": v(25.82, -19.16) * mm});
            skLineSegment(sketch, "E370", {"start": v(25.82, -19.16) * mm, "end": v(25.82, -18.07) * mm});
            skLineSegment(sketch, "E371", {"start": v(25.82, -18.07) * mm, "end": v(25.83, -17.71) * mm});
            skLineSegment(sketch, "E372", {"start": v(25.83, -17.71) * mm, "end": v(25.83, -17.36) * mm});
            skLineSegment(sketch, "E373", {"start": v(25.83, -17.36) * mm, "end": v(25.83, -17) * mm});
            skLineSegment(sketch, "E374", {"start": v(25.83, -17) * mm, "end": v(25.82, -16.64) * mm});
            skLineSegment(sketch, "E375", {"start": v(25.82, -16.64) * mm, "end": v(25.82, -16.24) * mm});
            skLineSegment(sketch, "E376", {"start": v(25.82, -16.24) * mm, "end": v(25.8, -15.84) * mm});
            skLineSegment(sketch, "E377", {"start": v(25.8, -15.84) * mm, "end": v(25.8, -15.44) * mm});
            skLineSegment(sketch, "E378", {"start": v(25.8, -15.44) * mm, "end": v(25.8, -15.04) * mm});
            skLineSegment(sketch, "E379", {"start": v(25.8, -15.04) * mm, "end": v(25.79, -14.75) * mm});
            skLineSegment(sketch, "E380", {"start": v(25.79, -14.75) * mm, "end": v(25.79, -14.46) * mm});
            skLineSegment(sketch, "E381", {"start": v(25.79, -14.46) * mm, "end": v(25.8, -14.16) * mm});
            skLineSegment(sketch, "E382", {"start": v(25.8, -14.16) * mm, "end": v(25.84, -13.88) * mm});
            skLineSegment(sketch, "E383", {"start": v(25.84, -13.88) * mm, "end": v(25.9, -13.63) * mm});
            skLineSegment(sketch, "E384", {"start": v(25.9, -13.63) * mm, "end": v(25.99, -13.38) * mm});
            skLineSegment(sketch, "E385", {"start": v(25.99, -13.38) * mm, "end": v(26.09, -13.14) * mm});
            skLineSegment(sketch, "E386", {"start": v(26.09, -13.14) * mm, "end": v(26.2, -12.9) * mm});
            skLineSegment(sketch, "E387", {"start": v(26.2, -12.9) * mm, "end": v(26.3, -12.73) * mm});
            skLineSegment(sketch, "E388", {"start": v(26.3, -12.73) * mm, "end": v(26.42, -12.55) * mm});
            skLineSegment(sketch, "E389", {"start": v(26.42, -12.55) * mm, "end": v(26.55, -12.4) * mm});
            skLineSegment(sketch, "E390", {"start": v(26.55, -12.4) * mm, "end": v(26.7, -12.27) * mm});
            skLineSegment(sketch, "E391", {"start": v(26.7, -12.27) * mm, "end": v(26.95, -12.1) * mm});
            skLineSegment(sketch, "E392", {"start": v(26.95, -12.1) * mm, "end": v(27.22, -11.99) * mm});
            skLineSegment(sketch, "E393", {"start": v(27.22, -11.99) * mm, "end": v(27.51, -11.93) * mm});
            skLineSegment(sketch, "E394", {"start": v(27.51, -11.93) * mm, "end": v(27.82, -11.95) * mm});
            skLineSegment(sketch, "E395", {"start": v(27.82, -11.95) * mm, "end": v(28.05, -12.02) * mm});
            skLineSegment(sketch, "E396", {"start": v(28.05, -12.02) * mm, "end": v(28.27, -12.13) * mm});
            skLineSegment(sketch, "E397", {"start": v(28.27, -12.13) * mm, "end": v(28.48, -12.27) * mm});
            skLineSegment(sketch, "E398", {"start": v(28.48, -12.27) * mm, "end": v(28.66, -12.45) * mm});
            skLineSegment(sketch, "E399", {"start": v(28.66, -12.45) * mm, "end": v(28.9, -12.75) * mm});
            skLineSegment(sketch, "E400", {"start": v(28.9, -12.75) * mm, "end": v(29.07, -13.07) * mm});
            skLineSegment(sketch, "E401", {"start": v(29.07, -13.07) * mm, "end": v(29.13, -13.22) * mm});
            skLineSegment(sketch, "E402", {"start": v(29.13, -13.22) * mm, "end": v(29.2, -13.42) * mm});
            skLineSegment(sketch, "E403", {"start": v(29.2, -13.42) * mm, "end": v(29.26, -13.8) * mm});
            skLineSegment(sketch, "E404", {"start": v(29.26, -13.8) * mm, "end": v(29.28, -14.08) * mm});
            skLineSegment(sketch, "E405", {"start": v(29.28, -14.08) * mm, "end": v(29.31, -14.37) * mm});
            skLineSegment(sketch, "E406", {"start": v(29.31, -14.37) * mm, "end": v(29.33, -14.65) * mm});
            skLineSegment(sketch, "E407", {"start": v(29.33, -14.65) * mm, "end": v(29.32, -14.93) * mm});
            skLineSegment(sketch, "E408", {"start": v(29.32, -14.93) * mm, "end": v(29.3, -15.32) * mm});
            skLineSegment(sketch, "E409", {"start": v(29.3, -15.32) * mm, "end": v(29.24, -15.71) * mm});
            skLineSegment(sketch, "E410", {"start": v(29.24, -15.71) * mm, "end": v(29.19, -16.1) * mm});
            skLineSegment(sketch, "E411", {"start": v(29.19, -16.1) * mm, "end": v(29.12, -16.49) * mm});
            skLineSegment(sketch, "E412", {"start": v(29.12, -16.49) * mm, "end": v(28.94, -17.3) * mm});
            skLineSegment(sketch, "E413", {"start": v(28.94, -17.3) * mm, "end": v(28.71, -18.08) * mm});
            skLineSegment(sketch, "E414", {"start": v(28.71, -18.08) * mm, "end": v(28.44, -18.86) * mm});
            skLineSegment(sketch, "E415", {"start": v(28.44, -18.86) * mm, "end": v(28.15, -19.63) * mm});
            skLineSegment(sketch, "E416", {"start": v(28.15, -19.63) * mm, "end": v(28.01, -19.99) * mm});
            skLineSegment(sketch, "E417", {"start": v(28.01, -19.99) * mm, "end": v(27.87, -20.35) * mm});
            skLineSegment(sketch, "E418", {"start": v(27.87, -20.35) * mm, "end": v(27.73, -20.71) * mm});
            skLineSegment(sketch, "E419", {"start": v(27.73, -20.71) * mm, "end": v(27.59, -21.07) * mm});
            skLineSegment(sketch, "E420", {"start": v(27.59, -21.07) * mm, "end": v(27.48, -21.36) * mm});
            skLineSegment(sketch, "E421", {"start": v(27.48, -21.36) * mm, "end": v(27.37, -21.66) * mm});
            skLineSegment(sketch, "E422", {"start": v(27.37, -21.66) * mm, "end": v(27.26, -21.95) * mm});
            skLineSegment(sketch, "E423", {"start": v(27.26, -21.95) * mm, "end": v(27.14, -22.24) * mm});
            skLineSegment(sketch, "E424", {"start": v(27.14, -22.24) * mm, "end": v(27.04, -22.48) * mm});
            skLineSegment(sketch, "E425", {"start": v(27.04, -22.48) * mm, "end": v(26.93, -22.72) * mm});
            skLineSegment(sketch, "E426", {"start": v(26.93, -22.72) * mm, "end": v(26.82, -22.96) * mm});
            skLineSegment(sketch, "E427", {"start": v(26.82, -22.96) * mm, "end": v(26.7, -23.2) * mm});
            skLineSegment(sketch, "E428", {"start": v(26.7, -23.2) * mm, "end": v(26.54, -23.58) * mm});
            skLineSegment(sketch, "E429", {"start": v(26.54, -23.58) * mm, "end": v(26.37, -23.97) * mm});
            skLineSegment(sketch, "E430", {"start": v(26.37, -23.97) * mm, "end": v(26.2, -24.36) * mm});
            skLineSegment(sketch, "E431", {"start": v(26.2, -24.36) * mm, "end": v(26.04, -24.76) * mm});
            skLineSegment(sketch, "E432", {"start": v(26.04, -24.76) * mm, "end": v(25.97, -24.93) * mm});
            skLineSegment(sketch, "E433", {"start": v(25.97, -24.93) * mm, "end": v(25.92, -25.1) * mm});
            skLineSegment(sketch, "E434", {"start": v(25.92, -25.1) * mm, "end": v(25.87, -25.27) * mm});
            skLineSegment(sketch, "E435", {"start": v(25.87, -25.27) * mm, "end": v(25.83, -25.44) * mm});
            skLineSegment(sketch, "E436", {"start": v(25.83, -25.44) * mm, "end": v(25.82, -25.44) * mm});
            skLineSegment(sketch, "E437", {"start": v(25.82, -25.44) * mm, "end": v(25.8, -25.44) * mm});
            skLineSegment(sketch, "E438", {"start": v(25.8, -25.44) * mm, "end": v(25.8, -25.44) * mm});
            skLineSegment(sketch, "E439", {"start": v(25.8, -25.44) * mm, "end": v(25.79, -25.44) * mm});
            skLineSegment(sketch, "E440", {"start": v(33.05, -3.22) * mm, "end": v(33.09, -3.1) * mm});
            skLineSegment(sketch, "E441", {"start": v(33.09, -3.1) * mm, "end": v(33.12, -2.98) * mm});
            skLineSegment(sketch, "E442", {"start": v(33.12, -2.98) * mm, "end": v(33.15, -2.87) * mm});
            skLineSegment(sketch, "E443", {"start": v(33.15, -2.87) * mm, "end": v(33.2, -2.78) * mm});
            skLineSegment(sketch, "E444", {"start": v(33.2, -2.78) * mm, "end": v(33.25, -2.72) * mm});
            skLineSegment(sketch, "E445", {"start": v(33.25, -2.72) * mm, "end": v(33.31, -2.66) * mm});
            skLineSegment(sketch, "E446", {"start": v(33.31, -2.66) * mm, "end": v(33.38, -2.62) * mm});
            skLineSegment(sketch, "E447", {"start": v(33.38, -2.62) * mm, "end": v(33.46, -2.59) * mm});
            skLineSegment(sketch, "E448", {"start": v(33.46, -2.59) * mm, "end": v(33.59, -2.53) * mm});
            skLineSegment(sketch, "E449", {"start": v(33.59, -2.53) * mm, "end": v(33.7, -2.47) * mm});
            skLineSegment(sketch, "E450", {"start": v(33.7, -2.47) * mm, "end": v(33.8, -2.37) * mm});
            skLineSegment(sketch, "E451", {"start": v(33.8, -2.37) * mm, "end": v(33.86, -2.24) * mm});
            skLineSegment(sketch, "E452", {"start": v(33.86, -2.24) * mm, "end": v(33.86, -2.17) * mm});
            skLineSegment(sketch, "E453", {"start": v(33.86, -2.17) * mm, "end": v(33.84, -2.1) * mm});
            skLineSegment(sketch, "E454", {"start": v(33.84, -2.1) * mm, "end": v(33.81, -2.03) * mm});
            skLineSegment(sketch, "E455", {"start": v(33.81, -2.03) * mm, "end": v(33.77, -2) * mm});
            skLineSegment(sketch, "E456", {"start": v(33.77, -2) * mm, "end": v(33.71, -2) * mm});
            skLineSegment(sketch, "E457", {"start": v(33.71, -2) * mm, "end": v(33.64, -2) * mm});
            skLineSegment(sketch, "E458", {"start": v(33.64, -2) * mm, "end": v(33.57, -2.03) * mm});
            skLineSegment(sketch, "E459", {"start": v(33.57, -2.03) * mm, "end": v(33.5, -2.06) * mm});
            skLineSegment(sketch, "E460", {"start": v(33.5, -2.06) * mm, "end": v(33.47, -2.07) * mm});
            skLineSegment(sketch, "E461", {"start": v(33.47, -2.07) * mm, "end": v(33.45, -2.1) * mm});
            skLineSegment(sketch, "E462", {"start": v(33.45, -2.1) * mm, "end": v(33.43, -2.11) * mm});
            skLineSegment(sketch, "E463", {"start": v(33.43, -2.11) * mm, "end": v(33.41, -2.14) * mm});
            skLineSegment(sketch, "E464", {"start": v(33.41, -2.14) * mm, "end": v(33.4, -2.12) * mm});
            skLineSegment(sketch, "E465", {"start": v(33.4, -2.12) * mm, "end": v(33.4, -2.11) * mm});
            skLineSegment(sketch, "E466", {"start": v(33.4, -2.11) * mm, "end": v(33.38, -2.1) * mm});
            skLineSegment(sketch, "E467", {"start": v(33.38, -2.1) * mm, "end": v(33.37, -2.1) * mm});
            skLineSegment(sketch, "E468", {"start": v(33.37, -2.1) * mm, "end": v(33.48, -1.97) * mm});
            skLineSegment(sketch, "E469", {"start": v(33.48, -1.97) * mm, "end": v(33.59, -1.85) * mm});
            skLineSegment(sketch, "E470", {"start": v(33.59, -1.85) * mm, "end": v(33.7, -1.73) * mm});
            skLineSegment(sketch, "E471", {"start": v(33.7, -1.73) * mm, "end": v(33.81, -1.61) * mm});
            skLineSegment(sketch, "E472", {"start": v(33.81, -1.61) * mm, "end": v(33.94, -1.46) * mm});
            skLineSegment(sketch, "E473", {"start": v(33.94, -1.46) * mm, "end": v(34.07, -1.31) * mm});
            skLineSegment(sketch, "E474", {"start": v(34.07, -1.31) * mm, "end": v(34.2, -1.16) * mm});
            skLineSegment(sketch, "E475", {"start": v(34.2, -1.16) * mm, "end": v(34.34, -1.03) * mm});
            skLineSegment(sketch, "E476", {"start": v(34.34, -1.03) * mm, "end": v(34.47, -0.93) * mm});
            skLineSegment(sketch, "E477", {"start": v(34.47, -0.93) * mm, "end": v(34.6, -0.85) * mm});
            skLineSegment(sketch, "E478", {"start": v(34.6, -0.85) * mm, "end": v(34.75, -0.77) * mm});
            skLineSegment(sketch, "E479", {"start": v(34.75, -0.77) * mm, "end": v(34.89, -0.7) * mm});
            skLineSegment(sketch, "E480", {"start": v(34.89, -0.7) * mm, "end": v(35.06, -0.6) * mm});
            skLineSegment(sketch, "E481", {"start": v(35.06, -0.6) * mm, "end": v(35.24, -0.51) * mm});
            skLineSegment(sketch, "E482", {"start": v(35.24, -0.51) * mm, "end": v(35.42, -0.42) * mm});
            skLineSegment(sketch, "E483", {"start": v(35.42, -0.42) * mm, "end": v(35.6, -0.33) * mm});
            skLineSegment(sketch, "E484", {"start": v(35.6, -0.33) * mm, "end": v(35.65, -0.29) * mm});
            skLineSegment(sketch, "E485", {"start": v(35.65, -0.29) * mm, "end": v(35.7, -0.25) * mm});
            skLineSegment(sketch, "E486", {"start": v(35.7, -0.25) * mm, "end": v(35.76, -0.2) * mm});
            skLineSegment(sketch, "E487", {"start": v(35.76, -0.2) * mm, "end": v(35.81, -0.16) * mm});
            skLineSegment(sketch, "E488", {"start": v(35.81, -0.16) * mm, "end": v(35.97, 0) * mm});
            skLineSegment(sketch, "E489", {"start": v(35.97, 0) * mm, "end": v(36.12, 0.15) * mm});
            skLineSegment(sketch, "E490", {"start": v(36.12, 0.15) * mm, "end": v(36.27, 0.3) * mm});
            skLineSegment(sketch, "E491", {"start": v(36.27, 0.3) * mm, "end": v(36.41, 0.46) * mm});
            skLineSegment(sketch, "E492", {"start": v(36.41, 0.46) * mm, "end": v(36.59, 0.7) * mm});
            skLineSegment(sketch, "E493", {"start": v(36.59, 0.7) * mm, "end": v(36.72, 0.98) * mm});
            skLineSegment(sketch, "E494", {"start": v(36.72, 0.98) * mm, "end": v(36.8, 1.26) * mm});
            skLineSegment(sketch, "E495", {"start": v(36.8, 1.26) * mm, "end": v(36.88, 1.55) * mm});
            skLineSegment(sketch, "E496", {"start": v(36.88, 1.55) * mm, "end": v(36.88, 1.68) * mm});
            skLineSegment(sketch, "E497", {"start": v(36.88, 1.68) * mm, "end": v(36.83, 1.78) * mm});
            skLineSegment(sketch, "E498", {"start": v(36.83, 1.78) * mm, "end": v(36.74, 1.85) * mm});
            skLineSegment(sketch, "E499", {"start": v(36.74, 1.85) * mm, "end": v(36.6, 1.87) * mm});
            skLineSegment(sketch, "E500", {"start": v(36.6, 1.87) * mm, "end": v(36.51, 1.88) * mm});
            skLineSegment(sketch, "E501", {"start": v(36.51, 1.88) * mm, "end": v(36.42, 1.9) * mm});
            skLineSegment(sketch, "E502", {"start": v(36.42, 1.9) * mm, "end": v(36.33, 1.9) * mm});
            skLineSegment(sketch, "E503", {"start": v(36.33, 1.9) * mm, "end": v(36.24, 1.92) * mm});
            skLineSegment(sketch, "E504", {"start": v(36.24, 1.92) * mm, "end": v(36.28, 2) * mm});
            skLineSegment(sketch, "E505", {"start": v(36.28, 2) * mm, "end": v(36.31, 2.07) * mm});
            skLineSegment(sketch, "E506", {"start": v(36.31, 2.07) * mm, "end": v(36.35, 2.15) * mm});
            skLineSegment(sketch, "E507", {"start": v(36.35, 2.15) * mm, "end": v(36.39, 2.22) * mm});
            skLineSegment(sketch, "E508", {"start": v(36.39, 2.22) * mm, "end": v(36.6, 2.64) * mm});
            skLineSegment(sketch, "E509", {"start": v(36.6, 2.64) * mm, "end": v(36.8, 3.07) * mm});
            skLineSegment(sketch, "E510", {"start": v(36.8, 3.07) * mm, "end": v(37.01, 3.5) * mm});
            skLineSegment(sketch, "E511", {"start": v(37.01, 3.5) * mm, "end": v(37.22, 3.92) * mm});
            skLineSegment(sketch, "E512", {"start": v(37.22, 3.92) * mm, "end": v(37.34, 4.18) * mm});
            skLineSegment(sketch, "E513", {"start": v(37.34, 4.18) * mm, "end": v(37.46, 4.45) * mm});
            skLineSegment(sketch, "E514", {"start": v(37.46, 4.45) * mm, "end": v(37.58, 4.7) * mm});
            skLineSegment(sketch, "E515", {"start": v(37.58, 4.7) * mm, "end": v(37.72, 4.95) * mm});
            skLineSegment(sketch, "E516", {"start": v(37.72, 4.95) * mm, "end": v(37.89, 5.19) * mm});
            skLineSegment(sketch, "E517", {"start": v(37.89, 5.19) * mm, "end": v(38.06, 5.41) * mm});
            skLineSegment(sketch, "E518", {"start": v(38.06, 5.41) * mm, "end": v(38.25, 5.63) * mm});
            skLineSegment(sketch, "E519", {"start": v(38.25, 5.63) * mm, "end": v(38.43, 5.85) * mm});
            skLineSegment(sketch, "E520", {"start": v(38.43, 5.85) * mm, "end": v(38.47, 5.9) * mm});
            skLineSegment(sketch, "E521", {"start": v(38.47, 5.9) * mm, "end": v(38.5, 5.95) * mm});
            skLineSegment(sketch, "E522", {"start": v(38.5, 5.95) * mm, "end": v(38.54, 6) * mm});
            skLineSegment(sketch, "E523", {"start": v(38.54, 6) * mm, "end": v(38.58, 6.04) * mm});
            skLineSegment(sketch, "E524", {"start": v(38.58, 6.04) * mm, "end": v(38.68, 6.13) * mm});
            skLineSegment(sketch, "E525", {"start": v(38.68, 6.13) * mm, "end": v(38.78, 6.22) * mm});
            skLineSegment(sketch, "E526", {"start": v(38.78, 6.22) * mm, "end": v(38.88, 6.3) * mm});
            skLineSegment(sketch, "E527", {"start": v(38.88, 6.3) * mm, "end": v(38.98, 6.4) * mm});
            skLineSegment(sketch, "E528", {"start": v(38.98, 6.4) * mm, "end": v(39.02, 6.42) * mm});
            skLineSegment(sketch, "E529", {"start": v(39.02, 6.42) * mm, "end": v(39.07, 6.44) * mm});
            skLineSegment(sketch, "E530", {"start": v(39.07, 6.44) * mm, "end": v(39.12, 6.46) * mm});
            skLineSegment(sketch, "E531", {"start": v(39.12, 6.46) * mm, "end": v(39.16, 6.49) * mm});
            skLineSegment(sketch, "E532", {"start": v(39.16, 6.49) * mm, "end": v(39.4, 6.68) * mm});
            skLineSegment(sketch, "E533", {"start": v(39.4, 6.68) * mm, "end": v(39.65, 6.8) * mm});
            skLineSegment(sketch, "E534", {"start": v(39.65, 6.8) * mm, "end": v(39.93, 6.87) * mm});
            skLineSegment(sketch, "E535", {"start": v(39.93, 6.87) * mm, "end": v(40.2, 6.93) * mm});
            skLineSegment(sketch, "E536", {"start": v(40.2, 6.93) * mm, "end": v(40.52, 6.94) * mm});
            skLineSegment(sketch, "E537", {"start": v(40.52, 6.94) * mm, "end": v(40.82, 6.88) * mm});
            skLineSegment(sketch, "E538", {"start": v(40.82, 6.88) * mm, "end": v(41.1, 6.76) * mm});
            skLineSegment(sketch, "E539", {"start": v(41.1, 6.76) * mm, "end": v(41.36, 6.57) * mm});
            skLineSegment(sketch, "E540", {"start": v(41.36, 6.57) * mm, "end": v(41.54, 6.36) * mm});
            skLineSegment(sketch, "E541", {"start": v(41.54, 6.36) * mm, "end": v(41.65, 6.13) * mm});
            skLineSegment(sketch, "E542", {"start": v(41.65, 6.13) * mm, "end": v(41.72, 5.88) * mm});
            skLineSegment(sketch, "E543", {"start": v(41.72, 5.88) * mm, "end": v(41.79, 5.63) * mm});
            skLineSegment(sketch, "E544", {"start": v(41.79, 5.63) * mm, "end": v(41.84, 5.44) * mm});
            skLineSegment(sketch, "E545", {"start": v(41.84, 5.44) * mm, "end": v(41.9, 5.25) * mm});
            skLineSegment(sketch, "E546", {"start": v(41.9, 5.25) * mm, "end": v(41.94, 5.07) * mm});
            skLineSegment(sketch, "E547", {"start": v(41.94, 5.07) * mm, "end": v(42.01, 4.88) * mm});
            skLineSegment(sketch, "E548", {"start": v(42.01, 4.88) * mm, "end": v(42.07, 4.78) * mm});
            skLineSegment(sketch, "E549", {"start": v(42.07, 4.78) * mm, "end": v(42.15, 4.68) * mm});
            skLineSegment(sketch, "E550", {"start": v(42.15, 4.68) * mm, "end": v(42.24, 4.6) * mm});
            skLineSegment(sketch, "E551", {"start": v(42.24, 4.6) * mm, "end": v(42.32, 4.5) * mm});
            skLineSegment(sketch, "E552", {"start": v(42.32, 4.5) * mm, "end": v(42.1, 4.33) * mm});
            skLineSegment(sketch, "E553", {"start": v(42.1, 4.33) * mm, "end": v(41.89, 4.15) * mm});
            skLineSegment(sketch, "E554", {"start": v(41.89, 4.15) * mm, "end": v(41.66, 3.96) * mm});
            skLineSegment(sketch, "E555", {"start": v(41.66, 3.96) * mm, "end": v(41.44, 3.77) * mm});
            skLineSegment(sketch, "E556", {"start": v(41.44, 3.77) * mm, "end": v(41.13, 3.5) * mm});
            skLineSegment(sketch, "E557", {"start": v(41.13, 3.5) * mm, "end": v(40.8, 3.21) * mm});
            skLineSegment(sketch, "E558", {"start": v(40.8, 3.21) * mm, "end": v(40.5, 2.92) * mm});
            skLineSegment(sketch, "E559", {"start": v(40.5, 2.92) * mm, "end": v(40.2, 2.62) * mm});
            skLineSegment(sketch, "E560", {"start": v(40.2, 2.62) * mm, "end": v(39.77, 2.13) * mm});
            skLineSegment(sketch, "E561", {"start": v(39.77, 2.13) * mm, "end": v(39.35, 1.64) * mm});
            skLineSegment(sketch, "E562", {"start": v(39.35, 1.64) * mm, "end": v(38.93, 1.14) * mm});
            skLineSegment(sketch, "E563", {"start": v(38.93, 1.14) * mm, "end": v(38.5, 0.64) * mm});
            skLineSegment(sketch, "E564", {"start": v(38.5, 0.64) * mm, "end": v(38.18, 0.28) * mm});
            skLineSegment(sketch, "E565", {"start": v(38.18, 0.28) * mm, "end": v(37.85, -0.07) * mm});
            skLineSegment(sketch, "E566", {"start": v(37.85, -0.07) * mm, "end": v(37.5, -0.42) * mm});
            skLineSegment(sketch, "E567", {"start": v(37.5, -0.42) * mm, "end": v(37.17, -0.76) * mm});
            skLineSegment(sketch, "E568", {"start": v(37.17, -0.76) * mm, "end": v(36.87, -1.04) * mm});
            skLineSegment(sketch, "E569", {"start": v(36.87, -1.04) * mm, "end": v(36.56, -1.32) * mm});
            skLineSegment(sketch, "E570", {"start": v(36.56, -1.32) * mm, "end": v(36.24, -1.57) * mm});
            skLineSegment(sketch, "E571", {"start": v(36.24, -1.57) * mm, "end": v(35.9, -1.8) * mm});
            skLineSegment(sketch, "E572", {"start": v(35.9, -1.8) * mm, "end": v(35.6, -1.98) * mm});
            skLineSegment(sketch, "E573", {"start": v(35.6, -1.98) * mm, "end": v(35.29, -2.15) * mm});
            skLineSegment(sketch, "E574", {"start": v(35.29, -2.15) * mm, "end": v(34.98, -2.33) * mm});
            skLineSegment(sketch, "E575", {"start": v(34.98, -2.33) * mm, "end": v(34.67, -2.5) * mm});
            skLineSegment(sketch, "E576", {"start": v(34.67, -2.5) * mm, "end": v(34.38, -2.65) * mm});
            skLineSegment(sketch, "E577", {"start": v(34.38, -2.65) * mm, "end": v(34.1, -2.79) * mm});
            skLineSegment(sketch, "E578", {"start": v(34.1, -2.79) * mm, "end": v(33.81, -2.93) * mm});
            skLineSegment(sketch, "E579", {"start": v(33.81, -2.93) * mm, "end": v(33.52, -3.07) * mm});
            skLineSegment(sketch, "E580", {"start": v(33.52, -3.07) * mm, "end": v(33.44, -3.1) * mm});
            skLineSegment(sketch, "E581", {"start": v(33.44, -3.1) * mm, "end": v(33.36, -3.14) * mm});
            skLineSegment(sketch, "E582", {"start": v(33.36, -3.14) * mm, "end": v(33.27, -3.17) * mm});
            skLineSegment(sketch, "E583", {"start": v(33.27, -3.17) * mm, "end": v(33.19, -3.2) * mm});
            skLineSegment(sketch, "E584", {"start": v(33.19, -3.2) * mm, "end": v(33.16, -3.21) * mm});
            skLineSegment(sketch, "E585", {"start": v(33.16, -3.21) * mm, "end": v(33.12, -3.22) * mm});
            skLineSegment(sketch, "E586", {"start": v(33.12, -3.22) * mm, "end": v(33.09, -3.22) * mm});
            skLineSegment(sketch, "E587", {"start": v(33.09, -3.22) * mm, "end": v(33.05, -3.22) * mm});
            skLineSegment(sketch, "E588", {"start": v(25.84, -8.02) * mm, "end": v(25.83, -7.78) * mm});
            skLineSegment(sketch, "E589", {"start": v(25.83, -7.78) * mm, "end": v(25.8, -7.55) * mm});
            skLineSegment(sketch, "E590", {"start": v(25.8, -7.55) * mm, "end": v(25.8, -7.32) * mm});
            skLineSegment(sketch, "E591", {"start": v(25.8, -7.32) * mm, "end": v(25.8, -7.08) * mm});
            skLineSegment(sketch, "E592", {"start": v(25.8, -7.08) * mm, "end": v(25.8, -6.71) * mm});
            skLineSegment(sketch, "E593", {"start": v(25.8, -6.71) * mm, "end": v(25.8, -6.34) * mm});
            skLineSegment(sketch, "E594", {"start": v(25.8, -6.34) * mm, "end": v(25.82, -5.97) * mm});
            skLineSegment(sketch, "E595", {"start": v(25.82, -5.97) * mm, "end": v(25.83, -5.6) * mm});
            skLineSegment(sketch, "E596", {"start": v(25.83, -5.6) * mm, "end": v(25.85, -5.55) * mm});
            skLineSegment(sketch, "E597", {"start": v(25.85, -5.55) * mm, "end": v(25.88, -5.5) * mm});
            skLineSegment(sketch, "E598", {"start": v(25.88, -5.5) * mm, "end": v(25.93, -5.47) * mm});
            skLineSegment(sketch, "E599", {"start": v(25.93, -5.47) * mm, "end": v(25.97, -5.45) * mm});
            skLineSegment(sketch, "E600", {"start": v(25.97, -5.45) * mm, "end": v(26.5, -5.42) * mm});
            skLineSegment(sketch, "E601", {"start": v(26.5, -5.42) * mm, "end": v(27.03, -5.4) * mm});
            skLineSegment(sketch, "E602", {"start": v(27.03, -5.4) * mm, "end": v(27.55, -5.37) * mm});
            skLineSegment(sketch, "E603", {"start": v(27.55, -5.37) * mm, "end": v(28.08, -5.35) * mm});
            skLineSegment(sketch, "E604", {"start": v(28.08, -5.35) * mm, "end": v(28.22, -5.34) * mm});
            skLineSegment(sketch, "E605", {"start": v(28.22, -5.34) * mm, "end": v(28.37, -5.32) * mm});
            skLineSegment(sketch, "E606", {"start": v(28.37, -5.32) * mm, "end": v(28.51, -5.3) * mm});
            skLineSegment(sketch, "E607", {"start": v(28.51, -5.3) * mm, "end": v(28.66, -5.28) * mm});
            skLineSegment(sketch, "E608", {"start": v(28.66, -5.28) * mm, "end": v(28.8, -5.29) * mm});
            skLineSegment(sketch, "E609", {"start": v(28.8, -5.29) * mm, "end": v(28.92, -5.34) * mm});
            skLineSegment(sketch, "E610", {"start": v(28.92, -5.34) * mm, "end": v(28.97, -5.45) * mm});
            skLineSegment(sketch, "E611", {"start": v(28.97, -5.45) * mm, "end": v(28.97, -5.6) * mm});
            skLineSegment(sketch, "E612", {"start": v(28.97, -5.6) * mm, "end": v(28.95, -5.78) * mm});
            skLineSegment(sketch, "E613", {"start": v(28.95, -5.78) * mm, "end": v(28.94, -5.95) * mm});
            skLineSegment(sketch, "E614", {"start": v(28.94, -5.95) * mm, "end": v(28.97, -6.13) * mm});
            skLineSegment(sketch, "E615", {"start": v(28.97, -6.13) * mm, "end": v(29.03, -6.3) * mm});
            skLineSegment(sketch, "E616", {"start": v(29.03, -6.3) * mm, "end": v(29.04, -6.32) * mm});
            skLineSegment(sketch, "E617", {"start": v(29.04, -6.32) * mm, "end": v(29.04, -6.34) * mm});
            skLineSegment(sketch, "E618", {"start": v(29.04, -6.34) * mm, "end": v(29.05, -6.36) * mm});
            skLineSegment(sketch, "E619", {"start": v(29.05, -6.36) * mm, "end": v(29.06, -6.38) * mm});
            skLineSegment(sketch, "E620", {"start": v(29.06, -6.38) * mm, "end": v(29.22, -6.64) * mm});
            skLineSegment(sketch, "E621", {"start": v(29.22, -6.64) * mm, "end": v(29.3, -6.92) * mm});
            skLineSegment(sketch, "E622", {"start": v(29.3, -6.92) * mm, "end": v(29.33, -7.2) * mm});
            skLineSegment(sketch, "E623", {"start": v(29.33, -7.2) * mm, "end": v(29.34, -7.5) * mm});
            skLineSegment(sketch, "E624", {"start": v(29.34, -7.5) * mm, "end": v(29.35, -7.83) * mm});
            skLineSegment(sketch, "E625", {"start": v(29.35, -7.83) * mm, "end": v(29.37, -8.16) * mm});
            skLineSegment(sketch, "E626", {"start": v(29.37, -8.16) * mm, "end": v(29.38, -8.48) * mm});
            skLineSegment(sketch, "E627", {"start": v(29.38, -8.48) * mm, "end": v(29.36, -8.8) * mm});
            skLineSegment(sketch, "E628", {"start": v(29.36, -8.8) * mm, "end": v(29.3, -9.3) * mm});
            skLineSegment(sketch, "E629", {"start": v(29.3, -9.3) * mm, "end": v(29.17, -9.76) * mm});
            skLineSegment(sketch, "E630", {"start": v(29.17, -9.76) * mm, "end": v(28.96, -10.2) * mm});
            skLineSegment(sketch, "E631", {"start": v(28.96, -10.2) * mm, "end": v(28.64, -10.58) * mm});
            skLineSegment(sketch, "E632", {"start": v(28.64, -10.58) * mm, "end": v(28.32, -10.82) * mm});
            skLineSegment(sketch, "E633", {"start": v(28.32, -10.82) * mm, "end": v(27.99, -10.98) * mm});
            skLineSegment(sketch, "E634", {"start": v(27.99, -10.98) * mm, "end": v(27.62, -11.05) * mm});
            skLineSegment(sketch, "E635", {"start": v(27.62, -11.05) * mm, "end": v(27.23, -11.03) * mm});
            skLineSegment(sketch, "E636", {"start": v(27.23, -11.03) * mm, "end": v(27.14, -11) * mm});
            skLineSegment(sketch, "E637", {"start": v(27.14, -11) * mm, "end": v(27.05, -10.97) * mm});
            skLineSegment(sketch, "E638", {"start": v(27.05, -10.97) * mm, "end": v(26.96, -10.92) * mm});
            skLineSegment(sketch, "E639", {"start": v(26.96, -10.92) * mm, "end": v(26.88, -10.87) * mm});
            skLineSegment(sketch, "E640", {"start": v(26.88, -10.87) * mm, "end": v(26.68, -10.71) * mm});
            skLineSegment(sketch, "E641", {"start": v(26.68, -10.71) * mm, "end": v(26.52, -10.53) * mm});
            skLineSegment(sketch, "E642", {"start": v(26.52, -10.53) * mm, "end": v(26.37, -10.33) * mm});
            skLineSegment(sketch, "E643", {"start": v(26.37, -10.33) * mm, "end": v(26.23, -10.12) * mm});
            skLineSegment(sketch, "E644", {"start": v(26.23, -10.12) * mm, "end": v(26, -9.62) * mm});
            skLineSegment(sketch, "E645", {"start": v(26, -9.62) * mm, "end": v(25.89, -9.1) * mm});
            skLineSegment(sketch, "E646", {"start": v(25.89, -9.1) * mm, "end": v(25.84, -8.56) * mm});
            skLineSegment(sketch, "E647", {"start": v(25.84, -8.56) * mm, "end": v(25.84, -8.02) * mm});
            skLineSegment(sketch, "E648", {"start": v(26.64, 4.32) * mm, "end": v(26.69, 4.76) * mm});
            skLineSegment(sketch, "E649", {"start": v(26.69, 4.76) * mm, "end": v(26.79, 5.17) * mm});
            skLineSegment(sketch, "E650", {"start": v(26.79, 5.17) * mm, "end": v(26.96, 5.53) * mm});
            skLineSegment(sketch, "E651", {"start": v(26.96, 5.53) * mm, "end": v(27.2, 5.86) * mm});
            skLineSegment(sketch, "E652", {"start": v(27.2, 5.86) * mm, "end": v(27.32, 5.99) * mm});
            skLineSegment(sketch, "E653", {"start": v(27.32, 5.99) * mm, "end": v(27.46, 6.1) * mm});
            skLineSegment(sketch, "E654", {"start": v(27.46, 6.1) * mm, "end": v(27.61, 6.2) * mm});
            skLineSegment(sketch, "E655", {"start": v(27.61, 6.2) * mm, "end": v(27.77, 6.28) * mm});
            skLineSegment(sketch, "E656", {"start": v(27.77, 6.28) * mm, "end": v(27.93, 6.33) * mm});
            skLineSegment(sketch, "E657", {"start": v(27.93, 6.33) * mm, "end": v(28.1, 6.35) * mm});
            skLineSegment(sketch, "E658", {"start": v(28.1, 6.35) * mm, "end": v(28.29, 6.36) * mm});
            skLineSegment(sketch, "E659", {"start": v(28.29, 6.36) * mm, "end": v(28.46, 6.34) * mm});
            skLineSegment(sketch, "E660", {"start": v(28.46, 6.34) * mm, "end": v(28.64, 6.3) * mm});
            skLineSegment(sketch, "E661", {"start": v(28.64, 6.3) * mm, "end": v(28.82, 6.25) * mm});
            skLineSegment(sketch, "E662", {"start": v(28.82, 6.25) * mm, "end": v(29, 6.19) * mm});
            skLineSegment(sketch, "E663", {"start": v(29, 6.19) * mm, "end": v(29.17, 6.11) * mm});
            skLineSegment(sketch, "E664", {"start": v(29.17, 6.11) * mm, "end": v(29.48, 5.94) * mm});
            skLineSegment(sketch, "E665", {"start": v(29.48, 5.94) * mm, "end": v(29.75, 5.72) * mm});
            skLineSegment(sketch, "E666", {"start": v(29.75, 5.72) * mm, "end": v(29.99, 5.46) * mm});
            skLineSegment(sketch, "E667", {"start": v(29.99, 5.46) * mm, "end": v(30.2, 5.17) * mm});
            skLineSegment(sketch, "E668", {"start": v(30.2, 5.17) * mm, "end": v(30.51, 4.67) * mm});
            skLineSegment(sketch, "E669", {"start": v(30.51, 4.67) * mm, "end": v(30.77, 4.15) * mm});
            skLineSegment(sketch, "E670", {"start": v(30.77, 4.15) * mm, "end": v(30.98, 3.62) * mm});
            skLineSegment(sketch, "E671", {"start": v(30.98, 3.62) * mm, "end": v(31.17, 3.07) * mm});
            skLineSegment(sketch, "E672", {"start": v(31.17, 3.07) * mm, "end": v(31.36, 2.6) * mm});
            skLineSegment(sketch, "E673", {"start": v(31.36, 2.6) * mm, "end": v(31.6, 2.16) * mm});
            skLineSegment(sketch, "E674", {"start": v(31.6, 2.16) * mm, "end": v(31.88, 1.75) * mm});
            skLineSegment(sketch, "E675", {"start": v(31.88, 1.75) * mm, "end": v(32.2, 1.36) * mm});
            skLineSegment(sketch, "E676", {"start": v(32.2, 1.36) * mm, "end": v(32.25, 1.31) * mm});
            skLineSegment(sketch, "E677", {"start": v(32.25, 1.31) * mm, "end": v(32.27, 1.27) * mm});
            skLineSegment(sketch, "E678", {"start": v(32.27, 1.27) * mm, "end": v(32.26, 1.22) * mm});
            skLineSegment(sketch, "E679", {"start": v(32.26, 1.22) * mm, "end": v(32.22, 1.16) * mm});
            skLineSegment(sketch, "E680", {"start": v(32.22, 1.16) * mm, "end": v(31.92, 0.8) * mm});
            skLineSegment(sketch, "E681", {"start": v(31.92, 0.8) * mm, "end": v(31.8, 0.4) * mm});
            skLineSegment(sketch, "E682", {"start": v(31.8, 0.4) * mm, "end": v(31.8, -0.03) * mm});
            skLineSegment(sketch, "E683", {"start": v(31.8, -0.03) * mm, "end": v(31.93, -0.47) * mm});
            skLineSegment(sketch, "E684", {"start": v(31.93, -0.47) * mm, "end": v(31.93, -0.49) * mm});
            skLineSegment(sketch, "E685", {"start": v(31.93, -0.49) * mm, "end": v(31.93, -0.5) * mm});
            skLineSegment(sketch, "E686", {"start": v(31.93, -0.5) * mm, "end": v(31.92, -0.52) * mm});
            skLineSegment(sketch, "E687", {"start": v(31.92, -0.52) * mm, "end": v(31.9, -0.55) * mm});
            skLineSegment(sketch, "E688", {"start": v(31.9, -0.55) * mm, "end": v(31.87, -0.52) * mm});
            skLineSegment(sketch, "E689", {"start": v(31.87, -0.52) * mm, "end": v(31.84, -0.5) * mm});
            skLineSegment(sketch, "E690", {"start": v(31.84, -0.5) * mm, "end": v(31.81, -0.46) * mm});
            skLineSegment(sketch, "E691", {"start": v(31.81, -0.46) * mm, "end": v(31.8, -0.42) * mm});
            skLineSegment(sketch, "E692", {"start": v(31.8, -0.42) * mm, "end": v(31.76, -0.32) * mm});
            skLineSegment(sketch, "E693", {"start": v(31.76, -0.32) * mm, "end": v(31.7, -0.24) * mm});
            skLineSegment(sketch, "E694", {"start": v(31.7, -0.24) * mm, "end": v(31.62, -0.17) * mm});
            skLineSegment(sketch, "E695", {"start": v(31.62, -0.17) * mm, "end": v(31.53, -0.12) * mm});
            skLineSegment(sketch, "E696", {"start": v(31.53, -0.12) * mm, "end": v(31.48, -0.1) * mm});
            skLineSegment(sketch, "E697", {"start": v(31.48, -0.1) * mm, "end": v(31.45, -0.05) * mm});
            skLineSegment(sketch, "E698", {"start": v(31.45, -0.05) * mm, "end": v(31.4, 0) * mm});
            skLineSegment(sketch, "E699", {"start": v(31.4, 0) * mm, "end": v(31.37, 0.03) * mm});
            skLineSegment(sketch, "E700", {"start": v(31.37, 0.03) * mm, "end": v(31.29, 0.1) * mm});
            skLineSegment(sketch, "E701", {"start": v(31.29, 0.1) * mm, "end": v(31.2, 0.17) * mm});
            skLineSegment(sketch, "E702", {"start": v(31.2, 0.17) * mm, "end": v(31.12, 0.24) * mm});
            skLineSegment(sketch, "E703", {"start": v(31.12, 0.24) * mm, "end": v(31.04, 0.3) * mm});
            skLineSegment(sketch, "E704", {"start": v(31.04, 0.3) * mm, "end": v(30.71, 0.59) * mm});
            skLineSegment(sketch, "E705", {"start": v(30.71, 0.59) * mm, "end": v(30.43, 0.9) * mm});
            skLineSegment(sketch, "E706", {"start": v(30.43, 0.9) * mm, "end": v(30.16, 1.24) * mm});
            skLineSegment(sketch, "E707", {"start": v(30.16, 1.24) * mm, "end": v(29.88, 1.57) * mm});
            skLineSegment(sketch, "E708", {"start": v(29.88, 1.57) * mm, "end": v(29.58, 1.9) * mm});
            skLineSegment(sketch, "E709", {"start": v(29.58, 1.9) * mm, "end": v(29.29, 2.24) * mm});
            skLineSegment(sketch, "E710", {"start": v(29.29, 2.24) * mm, "end": v(29, 2.58) * mm});
            skLineSegment(sketch, "E711", {"start": v(29, 2.58) * mm, "end": v(28.68, 2.9) * mm});
            skLineSegment(sketch, "E712", {"start": v(28.68, 2.9) * mm, "end": v(28.4, 3.17) * mm});
            skLineSegment(sketch, "E713", {"start": v(28.4, 3.17) * mm, "end": v(28.1, 3.42) * mm});
            skLineSegment(sketch, "E714", {"start": v(28.1, 3.42) * mm, "end": v(27.8, 3.67) * mm});
            skLineSegment(sketch, "E715", {"start": v(27.8, 3.67) * mm, "end": v(27.5, 3.92) * mm});
            skLineSegment(sketch, "E716", {"start": v(27.5, 3.92) * mm, "end": v(27.38, 4.02) * mm});
            skLineSegment(sketch, "E717", {"start": v(27.38, 4.02) * mm, "end": v(27.26, 4.12) * mm});
            skLineSegment(sketch, "E718", {"start": v(27.26, 4.12) * mm, "end": v(27.14, 4.22) * mm});
            skLineSegment(sketch, "E719", {"start": v(27.14, 4.22) * mm, "end": v(27.02, 4.32) * mm});
            skLineSegment(sketch, "E720", {"start": v(27.02, 4.32) * mm, "end": v(26.94, 4.38) * mm});
            skLineSegment(sketch, "E721", {"start": v(26.94, 4.38) * mm, "end": v(26.86, 4.42) * mm});
            skLineSegment(sketch, "E722", {"start": v(26.86, 4.42) * mm, "end": v(26.76, 4.4) * mm});
            skLineSegment(sketch, "E723", {"start": v(26.76, 4.4) * mm, "end": v(26.64, 4.32) * mm});
            skLineSegment(sketch, "E724", {"start": v(38.6, -30.36) * mm, "end": v(36.67, -30.36) * mm});
            skLineSegment(sketch, "E725", {"start": v(36.67, -30.36) * mm, "end": v(34.73, -30.36) * mm});
            skLineSegment(sketch, "E726", {"start": v(34.73, -30.36) * mm, "end": v(32.77, -30.36) * mm});
            skLineSegment(sketch, "E727", {"start": v(32.77, -30.36) * mm, "end": v(30.81, -30.36) * mm});
            skLineSegment(sketch, "E728", {"start": v(30.81, -30.36) * mm, "end": v(30.81, -30.35) * mm});
            skLineSegment(sketch, "E729", {"start": v(30.81, -30.35) * mm, "end": v(30.8, -30.34) * mm});
            skLineSegment(sketch, "E730", {"start": v(30.8, -30.34) * mm, "end": v(30.8, -30.32) * mm});
            skLineSegment(sketch, "E731", {"start": v(30.8, -30.32) * mm, "end": v(30.8, -30.31) * mm});
            skLineSegment(sketch, "E732", {"start": v(30.8, -30.31) * mm, "end": v(30.9, -30.27) * mm});
            skLineSegment(sketch, "E733", {"start": v(30.9, -30.27) * mm, "end": v(30.98, -30.22) * mm});
            skLineSegment(sketch, "E734", {"start": v(30.98, -30.22) * mm, "end": v(31.08, -30.17) * mm});
            skLineSegment(sketch, "E735", {"start": v(31.08, -30.17) * mm, "end": v(31.17, -30.13) * mm});
            skLineSegment(sketch, "E736", {"start": v(31.17, -30.13) * mm, "end": v(31.38, -30.03) * mm});
            skLineSegment(sketch, "E737", {"start": v(31.38, -30.03) * mm, "end": v(31.59, -29.93) * mm});
            skLineSegment(sketch, "E738", {"start": v(31.59, -29.93) * mm, "end": v(31.8, -29.83) * mm});
            skLineSegment(sketch, "E739", {"start": v(31.8, -29.83) * mm, "end": v(32, -29.71) * mm});
            skLineSegment(sketch, "E740", {"start": v(32, -29.71) * mm, "end": v(32.2, -29.57) * mm});
            skLineSegment(sketch, "E741", {"start": v(32.2, -29.57) * mm, "end": v(32.41, -29.42) * mm});
            skLineSegment(sketch, "E742", {"start": v(32.41, -29.42) * mm, "end": v(32.61, -29.27) * mm});
            skLineSegment(sketch, "E743", {"start": v(32.61, -29.27) * mm, "end": v(32.82, -29.12) * mm});
            skLineSegment(sketch, "E744", {"start": v(32.82, -29.12) * mm, "end": v(33.28, -28.8) * mm});
            skLineSegment(sketch, "E745", {"start": v(33.28, -28.8) * mm, "end": v(33.75, -28.47) * mm});
            skLineSegment(sketch, "E746", {"start": v(33.75, -28.47) * mm, "end": v(34.22, -28.16) * mm});
            skLineSegment(sketch, "E747", {"start": v(34.22, -28.16) * mm, "end": v(34.72, -27.9) * mm});
            skLineSegment(sketch, "E748", {"start": v(34.72, -27.9) * mm, "end": v(35, -27.75) * mm});
            skLineSegment(sketch, "E749", {"start": v(35, -27.75) * mm, "end": v(35.26, -27.6) * mm});
            skLineSegment(sketch, "E750", {"start": v(35.26, -27.6) * mm, "end": v(35.52, -27.47) * mm});
            skLineSegment(sketch, "E751", {"start": v(35.52, -27.47) * mm, "end": v(35.8, -27.34) * mm});
            skLineSegment(sketch, "E752", {"start": v(35.8, -27.34) * mm, "end": v(36.11, -27.22) * mm});
            skLineSegment(sketch, "E753", {"start": v(36.11, -27.22) * mm, "end": v(36.43, -27.1) * mm});
            skLineSegment(sketch, "E754", {"start": v(36.43, -27.1) * mm, "end": v(36.76, -27) * mm});
            skLineSegment(sketch, "E755", {"start": v(36.76, -27) * mm, "end": v(37.09, -26.91) * mm});
            skLineSegment(sketch, "E756", {"start": v(37.09, -26.91) * mm, "end": v(37.33, -26.9) * mm});
            skLineSegment(sketch, "E757", {"start": v(37.33, -26.9) * mm, "end": v(37.63, -26.95) * mm});
            skLineSegment(sketch, "E758", {"start": v(37.63, -26.95) * mm, "end": v(37.9, -27.08) * mm});
            skLineSegment(sketch, "E759", {"start": v(37.9, -27.08) * mm, "end": v(38.05, -27.28) * mm});
            skLineSegment(sketch, "E760", {"start": v(38.05, -27.28) * mm, "end": v(38.08, -27.41) * mm});
            skLineSegment(sketch, "E761", {"start": v(38.08, -27.41) * mm, "end": v(38.1, -27.55) * mm});
            skLineSegment(sketch, "E762", {"start": v(38.1, -27.55) * mm, "end": v(38.1, -27.68) * mm});
            skLineSegment(sketch, "E763", {"start": v(38.1, -27.68) * mm, "end": v(38.1, -27.81) * mm});
            skLineSegment(sketch, "E764", {"start": v(38.1, -27.81) * mm, "end": v(38.06, -28.06) * mm});
            skLineSegment(sketch, "E765", {"start": v(38.06, -28.06) * mm, "end": v(38.02, -28.31) * mm});
            skLineSegment(sketch, "E766", {"start": v(38.02, -28.31) * mm, "end": v(37.98, -28.56) * mm});
            skLineSegment(sketch, "E767", {"start": v(37.98, -28.56) * mm, "end": v(37.93, -28.8) * mm});
            skLineSegment(sketch, "E768", {"start": v(37.93, -28.8) * mm, "end": v(37.92, -29.12) * mm});
            skLineSegment(sketch, "E769", {"start": v(37.92, -29.12) * mm, "end": v(37.98, -29.42) * mm});
            skLineSegment(sketch, "E770", {"start": v(37.98, -29.42) * mm, "end": v(38.1, -29.7) * mm});
            skLineSegment(sketch, "E771", {"start": v(38.1, -29.7) * mm, "end": v(38.27, -29.95) * mm});
            skLineSegment(sketch, "E772", {"start": v(38.27, -29.95) * mm, "end": v(38.35, -30.06) * mm});
            skLineSegment(sketch, "E773", {"start": v(38.35, -30.06) * mm, "end": v(38.43, -30.16) * mm});
            skLineSegment(sketch, "E774", {"start": v(38.43, -30.16) * mm, "end": v(38.52, -30.26) * mm});
            skLineSegment(sketch, "E775", {"start": v(38.52, -30.26) * mm, "end": v(38.6, -30.36) * mm});
            skLineSegment(sketch, "E776", {"start": v(47.26, -0.21) * mm, "end": v(47.32, -0.1) * mm});
            skLineSegment(sketch, "E777", {"start": v(47.32, -0.1) * mm, "end": v(47.37, 0) * mm});
            skLineSegment(sketch, "E778", {"start": v(47.37, 0) * mm, "end": v(47.43, 0.1) * mm});
            skLineSegment(sketch, "E779", {"start": v(47.43, 0.1) * mm, "end": v(47.47, 0.22) * mm});
            skLineSegment(sketch, "E780", {"start": v(47.47, 0.22) * mm, "end": v(47.52, 0.35) * mm});
            skLineSegment(sketch, "E781", {"start": v(47.52, 0.35) * mm, "end": v(47.56, 0.49) * mm});
            skLineSegment(sketch, "E782", {"start": v(47.56, 0.49) * mm, "end": v(47.59, 0.63) * mm});
            skLineSegment(sketch, "E783", {"start": v(47.59, 0.63) * mm, "end": v(47.6, 0.77) * mm});
            skLineSegment(sketch, "E784", {"start": v(47.6, 0.77) * mm, "end": v(47.6, 1) * mm});
            skLineSegment(sketch, "E785", {"start": v(47.6, 1) * mm, "end": v(47.6, 1.24) * mm});
            skLineSegment(sketch, "E786", {"start": v(47.6, 1.24) * mm, "end": v(47.6, 1.47) * mm});
            skLineSegment(sketch, "E787", {"start": v(47.6, 1.47) * mm, "end": v(47.55, 1.7) * mm});
            skLineSegment(sketch, "E788", {"start": v(47.55, 1.7) * mm, "end": v(47.43, 2.05) * mm});
            skLineSegment(sketch, "E789", {"start": v(47.43, 2.05) * mm, "end": v(47.25, 2.36) * mm});
            skLineSegment(sketch, "E790", {"start": v(47.25, 2.36) * mm, "end": v(47.01, 2.63) * mm});
            skLineSegment(sketch, "E791", {"start": v(47.01, 2.63) * mm, "end": v(46.7, 2.87) * mm});
            skLineSegment(sketch, "E792", {"start": v(46.7, 2.87) * mm, "end": v(46.48, 3) * mm});
            skLineSegment(sketch, "E793", {"start": v(46.48, 3) * mm, "end": v(46.26, 3.12) * mm});
            skLineSegment(sketch, "E794", {"start": v(46.26, 3.12) * mm, "end": v(46.02, 3.22) * mm});
            skLineSegment(sketch, "E795", {"start": v(46.02, 3.22) * mm, "end": v(45.78, 3.27) * mm});
            skLineSegment(sketch, "E796", {"start": v(45.78, 3.27) * mm, "end": v(45.54, 3.3) * mm});
            skLineSegment(sketch, "E797", {"start": v(45.54, 3.3) * mm, "end": v(45.3, 3.33) * mm});
            skLineSegment(sketch, "E798", {"start": v(45.3, 3.33) * mm, "end": v(45.05, 3.33) * mm});
            skLineSegment(sketch, "E799", {"start": v(45.05, 3.33) * mm, "end": v(44.81, 3.32) * mm});
            skLineSegment(sketch, "E800", {"start": v(44.81, 3.32) * mm, "end": v(44.1, 3.2) * mm});
            skLineSegment(sketch, "E801", {"start": v(44.1, 3.2) * mm, "end": v(43.44, 2.98) * mm});
            skLineSegment(sketch, "E802", {"start": v(43.44, 2.98) * mm, "end": v(42.79, 2.7) * mm});
            skLineSegment(sketch, "E803", {"start": v(42.79, 2.7) * mm, "end": v(42.15, 2.38) * mm});
            skLineSegment(sketch, "E804", {"start": v(42.15, 2.38) * mm, "end": v(41.95, 2.27) * mm});
            skLineSegment(sketch, "E805", {"start": v(41.95, 2.27) * mm, "end": v(41.75, 2.14) * mm});
            skLineSegment(sketch, "E806", {"start": v(41.75, 2.14) * mm, "end": v(41.55, 2) * mm});
            skLineSegment(sketch, "E807", {"start": v(41.55, 2) * mm, "end": v(41.36, 1.87) * mm});
            skLineSegment(sketch, "E808", {"start": v(41.36, 1.87) * mm, "end": v(41.04, 1.62) * mm});
            skLineSegment(sketch, "E809", {"start": v(41.04, 1.62) * mm, "end": v(40.72, 1.37) * mm});
            skLineSegment(sketch, "E810", {"start": v(40.72, 1.37) * mm, "end": v(40.4, 1.12) * mm});
            skLineSegment(sketch, "E811", {"start": v(40.4, 1.12) * mm, "end": v(40.08, 0.87) * mm});
            skLineSegment(sketch, "E812", {"start": v(40.08, 0.87) * mm, "end": v(40.06, 0.85) * mm});
            skLineSegment(sketch, "E813", {"start": v(40.06, 0.85) * mm, "end": v(40.03, 0.84) * mm});
            skLineSegment(sketch, "E814", {"start": v(40.03, 0.84) * mm, "end": v(40, 0.84) * mm});
            skLineSegment(sketch, "E815", {"start": v(40, 0.84) * mm, "end": v(39.95, 0.84) * mm});
            skLineSegment(sketch, "E816", {"start": v(39.95, 0.84) * mm, "end": v(40.06, 0.99) * mm});
            skLineSegment(sketch, "E817", {"start": v(40.06, 0.99) * mm, "end": v(40.17, 1.13) * mm});
            skLineSegment(sketch, "E818", {"start": v(40.17, 1.13) * mm, "end": v(40.28, 1.28) * mm});
            skLineSegment(sketch, "E819", {"start": v(40.28, 1.28) * mm, "end": v(40.4, 1.42) * mm});
            skLineSegment(sketch, "E820", {"start": v(40.4, 1.42) * mm, "end": v(40.62, 1.68) * mm});
            skLineSegment(sketch, "E821", {"start": v(40.62, 1.68) * mm, "end": v(40.85, 1.94) * mm});
            skLineSegment(sketch, "E822", {"start": v(40.85, 1.94) * mm, "end": v(41.09, 2.2) * mm});
            skLineSegment(sketch, "E823", {"start": v(41.09, 2.2) * mm, "end": v(41.33, 2.44) * mm});
            skLineSegment(sketch, "E824", {"start": v(41.33, 2.44) * mm, "end": v(41.51, 2.62) * mm});
            skLineSegment(sketch, "E825", {"start": v(41.51, 2.62) * mm, "end": v(41.7, 2.79) * mm});
            skLineSegment(sketch, "E826", {"start": v(41.7, 2.79) * mm, "end": v(41.9, 2.96) * mm});
            skLineSegment(sketch, "E827", {"start": v(41.9, 2.96) * mm, "end": v(42.1, 3.12) * mm});
            skLineSegment(sketch, "E828", {"start": v(42.1, 3.12) * mm, "end": v(42.18, 3.2) * mm});
            skLineSegment(sketch, "E829", {"start": v(42.18, 3.2) * mm, "end": v(42.25, 3.27) * mm});
            skLineSegment(sketch, "E830", {"start": v(42.25, 3.27) * mm, "end": v(42.34, 3.34) * mm});
            skLineSegment(sketch, "E831", {"start": v(42.34, 3.34) * mm, "end": v(42.42, 3.4) * mm});
            skLineSegment(sketch, "E832", {"start": v(42.42, 3.4) * mm, "end": v(42.6, 3.52) * mm});
            skLineSegment(sketch, "E833", {"start": v(42.6, 3.52) * mm, "end": v(42.8, 3.65) * mm});
            skLineSegment(sketch, "E834", {"start": v(42.8, 3.65) * mm, "end": v(43, 3.77) * mm});
            skLineSegment(sketch, "E835", {"start": v(43, 3.77) * mm, "end": v(43.2, 3.87) * mm});
            skLineSegment(sketch, "E836", {"start": v(43.2, 3.87) * mm, "end": v(43.6, 4.06) * mm});
            skLineSegment(sketch, "E837", {"start": v(43.6, 4.06) * mm, "end": v(44.01, 4.24) * mm});
            skLineSegment(sketch, "E838", {"start": v(44.01, 4.24) * mm, "end": v(44.43, 4.4) * mm});
            skLineSegment(sketch, "E839", {"start": v(44.43, 4.4) * mm, "end": v(44.85, 4.55) * mm});
            skLineSegment(sketch, "E840", {"start": v(44.85, 4.55) * mm, "end": v(45.2, 4.63) * mm});
            skLineSegment(sketch, "E841", {"start": v(45.2, 4.63) * mm, "end": v(45.56, 4.68) * mm});
            skLineSegment(sketch, "E842", {"start": v(45.56, 4.68) * mm, "end": v(45.92, 4.7) * mm});
            skLineSegment(sketch, "E843", {"start": v(45.92, 4.7) * mm, "end": v(46.28, 4.74) * mm});
            skLineSegment(sketch, "E844", {"start": v(46.28, 4.74) * mm, "end": v(46.63, 4.74) * mm});
            skLineSegment(sketch, "E845", {"start": v(46.63, 4.74) * mm, "end": v(46.98, 4.7) * mm});
            skLineSegment(sketch, "E846", {"start": v(46.98, 4.7) * mm, "end": v(47.33, 4.62) * mm});
            skLineSegment(sketch, "E847", {"start": v(47.33, 4.62) * mm, "end": v(47.67, 4.52) * mm});
            skLineSegment(sketch, "E848", {"start": v(47.67, 4.52) * mm, "end": v(48.2, 4.3) * mm});
            skLineSegment(sketch, "E849", {"start": v(48.2, 4.3) * mm, "end": v(48.63, 4) * mm});
            skLineSegment(sketch, "E850", {"start": v(48.63, 4) * mm, "end": v(49, 3.6) * mm});
            skLineSegment(sketch, "E851", {"start": v(49, 3.6) * mm, "end": v(49.29, 3.14) * mm});
            skLineSegment(sketch, "E852", {"start": v(49.29, 3.14) * mm, "end": v(49.42, 2.78) * mm});
            skLineSegment(sketch, "E853", {"start": v(49.42, 2.78) * mm, "end": v(49.47, 2.41) * mm});
            skLineSegment(sketch, "E854", {"start": v(49.47, 2.41) * mm, "end": v(49.43, 2.03) * mm});
            skLineSegment(sketch, "E855", {"start": v(49.43, 2.03) * mm, "end": v(49.33, 1.66) * mm});
            skLineSegment(sketch, "E856", {"start": v(49.33, 1.66) * mm, "end": v(49.16, 1.32) * mm});
            skLineSegment(sketch, "E857", {"start": v(49.16, 1.32) * mm, "end": v(48.93, 1.02) * mm});
            skLineSegment(sketch, "E858", {"start": v(48.93, 1.02) * mm, "end": v(48.67, 0.77) * mm});
            skLineSegment(sketch, "E859", {"start": v(48.67, 0.77) * mm, "end": v(48.38, 0.53) * mm});
            skLineSegment(sketch, "E860", {"start": v(48.38, 0.53) * mm, "end": v(48.14, 0.34) * mm});
            skLineSegment(sketch, "E861", {"start": v(48.14, 0.34) * mm, "end": v(47.89, 0.15) * mm});
            skLineSegment(sketch, "E862", {"start": v(47.89, 0.15) * mm, "end": v(47.64, -0.03) * mm});
            skLineSegment(sketch, "E863", {"start": v(47.64, -0.03) * mm, "end": v(47.39, -0.2) * mm});
            skLineSegment(sketch, "E864", {"start": v(47.39, -0.2) * mm, "end": v(47.37, -0.22) * mm});
            skLineSegment(sketch, "E865", {"start": v(47.37, -0.22) * mm, "end": v(47.35, -0.23) * mm});
            skLineSegment(sketch, "E866", {"start": v(47.35, -0.23) * mm, "end": v(47.33, -0.24) * mm});
            skLineSegment(sketch, "E867", {"start": v(47.33, -0.24) * mm, "end": v(47.3, -0.25) * mm});
            skLineSegment(sketch, "E868", {"start": v(47.3, -0.25) * mm, "end": v(47.3, -0.24) * mm});
            skLineSegment(sketch, "E869", {"start": v(47.3, -0.24) * mm, "end": v(47.28, -0.23) * mm});
            skLineSegment(sketch, "E870", {"start": v(47.28, -0.23) * mm, "end": v(47.27, -0.22) * mm});
            skLineSegment(sketch, "E871", {"start": v(47.27, -0.22) * mm, "end": v(47.26, -0.21) * mm});
            skLineSegment(sketch, "E872", {"start": v(29.87, 7.07) * mm, "end": v(30.95, 7.07) * mm});
            skLineSegment(sketch, "E873", {"start": v(30.95, 7.07) * mm, "end": v(32.04, 7.07) * mm});
            skLineSegment(sketch, "E874", {"start": v(32.04, 7.07) * mm, "end": v(33.12, 7.07) * mm});
            skLineSegment(sketch, "E875", {"start": v(33.12, 7.07) * mm, "end": v(34.2, 7.07) * mm});
            skLineSegment(sketch, "E876", {"start": v(34.2, 7.07) * mm, "end": v(33.98, 6.75) * mm});
            skLineSegment(sketch, "E877", {"start": v(33.98, 6.75) * mm, "end": v(33.77, 6.44) * mm});
            skLineSegment(sketch, "E878", {"start": v(33.77, 6.44) * mm, "end": v(33.61, 6.1) * mm});
            skLineSegment(sketch, "E879", {"start": v(33.61, 6.1) * mm, "end": v(33.51, 5.72) * mm});
            skLineSegment(sketch, "E880", {"start": v(33.51, 5.72) * mm, "end": v(33.5, 5.33) * mm});
            skLineSegment(sketch, "E881", {"start": v(33.5, 5.33) * mm, "end": v(33.54, 4.96) * mm});
            skLineSegment(sketch, "E882", {"start": v(33.54, 4.96) * mm, "end": v(33.63, 4.6) * mm});
            skLineSegment(sketch, "E883", {"start": v(33.63, 4.6) * mm, "end": v(33.77, 4.24) * mm});
            skLineSegment(sketch, "E884", {"start": v(33.77, 4.24) * mm, "end": v(33.98, 3.92) * mm});
            skLineSegment(sketch, "E885", {"start": v(33.98, 3.92) * mm, "end": v(34.26, 3.67) * mm});
            skLineSegment(sketch, "E886", {"start": v(34.26, 3.67) * mm, "end": v(34.56, 3.44) * mm});
            skLineSegment(sketch, "E887", {"start": v(34.56, 3.44) * mm, "end": v(34.85, 3.18) * mm});
            skLineSegment(sketch, "E888", {"start": v(34.85, 3.18) * mm, "end": v(34.32, 3) * mm});
            skLineSegment(sketch, "E889", {"start": v(34.32, 3) * mm, "end": v(33.87, 2.7) * mm});
            skLineSegment(sketch, "E890", {"start": v(33.87, 2.7) * mm, "end": v(33.47, 2.35) * mm});
            skLineSegment(sketch, "E891", {"start": v(33.47, 2.35) * mm, "end": v(33.1, 1.97) * mm});
            skLineSegment(sketch, "E892", {"start": v(33.1, 1.97) * mm, "end": v(33.02, 1.9) * mm});
            skLineSegment(sketch, "E893", {"start": v(33.02, 1.9) * mm, "end": v(32.95, 1.88) * mm});
            skLineSegment(sketch, "E894", {"start": v(32.95, 1.88) * mm, "end": v(32.88, 1.91) * mm});
            skLineSegment(sketch, "E895", {"start": v(32.88, 1.91) * mm, "end": v(32.8, 1.98) * mm});
            skLineSegment(sketch, "E896", {"start": v(32.8, 1.98) * mm, "end": v(32.5, 2.39) * mm});
            skLineSegment(sketch, "E897", {"start": v(32.5, 2.39) * mm, "end": v(32.27, 2.83) * mm});
            skLineSegment(sketch, "E898", {"start": v(32.27, 2.83) * mm, "end": v(32.1, 3.29) * mm});
            skLineSegment(sketch, "E899", {"start": v(32.1, 3.29) * mm, "end": v(31.94, 3.76) * mm});
            skLineSegment(sketch, "E900", {"start": v(31.94, 3.76) * mm, "end": v(31.71, 4.4) * mm});
            skLineSegment(sketch, "E901", {"start": v(31.71, 4.4) * mm, "end": v(31.45, 5.03) * mm});
            skLineSegment(sketch, "E902", {"start": v(31.45, 5.03) * mm, "end": v(31.13, 5.63) * mm});
            skLineSegment(sketch, "E903", {"start": v(31.13, 5.63) * mm, "end": v(30.74, 6.2) * mm});
            skLineSegment(sketch, "E904", {"start": v(30.74, 6.2) * mm, "end": v(30.56, 6.4) * mm});
            skLineSegment(sketch, "E905", {"start": v(30.56, 6.4) * mm, "end": v(30.35, 6.6) * mm});
            skLineSegment(sketch, "E906", {"start": v(30.35, 6.6) * mm, "end": v(30.13, 6.79) * mm});
            skLineSegment(sketch, "E907", {"start": v(30.13, 6.79) * mm, "end": v(29.92, 6.98) * mm});
            skLineSegment(sketch, "E908", {"start": v(29.92, 6.98) * mm, "end": v(29.9, 7) * mm});
            skLineSegment(sketch, "E909", {"start": v(29.9, 7) * mm, "end": v(29.88, 7) * mm});
            skLineSegment(sketch, "E910", {"start": v(29.88, 7) * mm, "end": v(29.86, 7) * mm});
            skLineSegment(sketch, "E911", {"start": v(29.86, 7) * mm, "end": v(29.84, 7.01) * mm});
            skLineSegment(sketch, "E912", {"start": v(29.84, 7.01) * mm, "end": v(29.85, 7.03) * mm});
            skLineSegment(sketch, "E913", {"start": v(29.85, 7.03) * mm, "end": v(29.85, 7.04) * mm});
            skLineSegment(sketch, "E914", {"start": v(29.85, 7.04) * mm, "end": v(29.86, 7.05) * mm});
            skLineSegment(sketch, "E915", {"start": v(29.86, 7.05) * mm, "end": v(29.87, 7.07) * mm});
            skLineSegment(sketch, "E916", {"start": v(49.71, 0.65) * mm, "end": v(49.71, 0.22) * mm});
            skLineSegment(sketch, "E917", {"start": v(49.71, 0.22) * mm, "end": v(49.71, -0.22) * mm});
            skLineSegment(sketch, "E918", {"start": v(49.71, -0.22) * mm, "end": v(49.71, -0.65) * mm});
            skLineSegment(sketch, "E919", {"start": v(49.71, -0.65) * mm, "end": v(49.71, -1.1) * mm});
            skLineSegment(sketch, "E920", {"start": v(49.71, -1.1) * mm, "end": v(49.68, -1.08) * mm});
            skLineSegment(sketch, "E921", {"start": v(49.68, -1.08) * mm, "end": v(49.64, -1.06) * mm});
            skLineSegment(sketch, "E922", {"start": v(49.64, -1.06) * mm, "end": v(49.61, -1.05) * mm});
            skLineSegment(sketch, "E923", {"start": v(49.61, -1.05) * mm, "end": v(49.58, -1.03) * mm});
            skLineSegment(sketch, "E924", {"start": v(49.58, -1.03) * mm, "end": v(49.33, -0.9) * mm});
            skLineSegment(sketch, "E925", {"start": v(49.33, -0.9) * mm, "end": v(49.08, -0.82) * mm});
            skLineSegment(sketch, "E926", {"start": v(49.08, -0.82) * mm, "end": v(48.8, -0.8) * mm});
            skLineSegment(sketch, "E927", {"start": v(48.8, -0.8) * mm, "end": v(48.53, -0.85) * mm});
            skLineSegment(sketch, "E928", {"start": v(48.53, -0.85) * mm, "end": v(48.5, -0.86) * mm});
            skLineSegment(sketch, "E929", {"start": v(48.5, -0.86) * mm, "end": v(48.49, -0.87) * mm});
            skLineSegment(sketch, "E930", {"start": v(48.49, -0.87) * mm, "end": v(48.46, -0.88) * mm});
            skLineSegment(sketch, "E931", {"start": v(48.46, -0.88) * mm, "end": v(48.44, -0.89) * mm});
            skLineSegment(sketch, "E932", {"start": v(48.44, -0.89) * mm, "end": v(48.16, -1.1) * mm});
            skLineSegment(sketch, "E933", {"start": v(48.16, -1.1) * mm, "end": v(47.95, -1.34) * mm});
            skLineSegment(sketch, "E934", {"start": v(47.95, -1.34) * mm, "end": v(47.82, -1.63) * mm});
            skLineSegment(sketch, "E935", {"start": v(47.82, -1.63) * mm, "end": v(47.8, -1.98) * mm});
            skLineSegment(sketch, "E936", {"start": v(47.8, -1.98) * mm, "end": v(47.85, -2.2) * mm});
            skLineSegment(sketch, "E937", {"start": v(47.85, -2.2) * mm, "end": v(47.93, -2.4) * mm});
            skLineSegment(sketch, "E938", {"start": v(47.93, -2.4) * mm, "end": v(48.03, -2.62) * mm});
            skLineSegment(sketch, "E939", {"start": v(48.03, -2.62) * mm, "end": v(48.15, -2.82) * mm});
            skLineSegment(sketch, "E940", {"start": v(48.15, -2.82) * mm, "end": v(48.24, -2.95) * mm});
            skLineSegment(sketch, "E941", {"start": v(48.24, -2.95) * mm, "end": v(48.34, -3.07) * mm});
            skLineSegment(sketch, "E942", {"start": v(48.34, -3.07) * mm, "end": v(48.46, -3.19) * mm});
            skLineSegment(sketch, "E943", {"start": v(48.46, -3.19) * mm, "end": v(48.59, -3.3) * mm});
            skLineSegment(sketch, "E944", {"start": v(48.59, -3.3) * mm, "end": v(48.83, -3.62) * mm});
            skLineSegment(sketch, "E945", {"start": v(48.83, -3.62) * mm, "end": v(48.92, -4.01) * mm});
            skLineSegment(sketch, "E946", {"start": v(48.92, -4.01) * mm, "end": v(48.85, -4.42) * mm});
            skLineSegment(sketch, "E947", {"start": v(48.85, -4.42) * mm, "end": v(48.6, -4.8) * mm});
            skLineSegment(sketch, "E948", {"start": v(48.6, -4.8) * mm, "end": v(48.43, -4.94) * mm});
            skLineSegment(sketch, "E949", {"start": v(48.43, -4.94) * mm, "end": v(48.25, -5.05) * mm});
            skLineSegment(sketch, "E950", {"start": v(48.25, -5.05) * mm, "end": v(48.06, -5.13) * mm});
            skLineSegment(sketch, "E951", {"start": v(48.06, -5.13) * mm, "end": v(47.83, -5.15) * mm});
            skLineSegment(sketch, "E952", {"start": v(47.83, -5.15) * mm, "end": v(47.6, -5.13) * mm});
            skLineSegment(sketch, "E953", {"start": v(47.6, -5.13) * mm, "end": v(47.4, -5.08) * mm});
            skLineSegment(sketch, "E954", {"start": v(47.4, -5.08) * mm, "end": v(47.2, -5) * mm});
            skLineSegment(sketch, "E955", {"start": v(47.2, -5) * mm, "end": v(47, -4.89) * mm});
            skLineSegment(sketch, "E956", {"start": v(47, -4.89) * mm, "end": v(46.73, -4.66) * mm});
            skLineSegment(sketch, "E957", {"start": v(46.73, -4.66) * mm, "end": v(46.54, -4.4) * mm});
            skLineSegment(sketch, "E958", {"start": v(46.54, -4.4) * mm, "end": v(46.4, -4.1) * mm});
            skLineSegment(sketch, "E959", {"start": v(46.4, -4.1) * mm, "end": v(46.29, -3.78) * mm});
            skLineSegment(sketch, "E960", {"start": v(46.29, -3.78) * mm, "end": v(46.18, -3.34) * mm});
            skLineSegment(sketch, "E961", {"start": v(46.18, -3.34) * mm, "end": v(46.19, -2.91) * mm});
            skLineSegment(sketch, "E962", {"start": v(46.19, -2.91) * mm, "end": v(46.29, -2.5) * mm});
            skLineSegment(sketch, "E963", {"start": v(46.29, -2.5) * mm, "end": v(46.45, -2.08) * mm});
            skLineSegment(sketch, "E964", {"start": v(46.45, -2.08) * mm, "end": v(46.54, -1.9) * mm});
            skLineSegment(sketch, "E965", {"start": v(46.54, -1.9) * mm, "end": v(46.65, -1.75) * mm});
            skLineSegment(sketch, "E966", {"start": v(46.65, -1.75) * mm, "end": v(46.79, -1.62) * mm});
            skLineSegment(sketch, "E967", {"start": v(46.79, -1.62) * mm, "end": v(46.94, -1.5) * mm});
            skLineSegment(sketch, "E968", {"start": v(46.94, -1.5) * mm, "end": v(47.06, -1.4) * mm});
            skLineSegment(sketch, "E969", {"start": v(47.06, -1.4) * mm, "end": v(47.16, -1.3) * mm});
            skLineSegment(sketch, "E970", {"start": v(47.16, -1.3) * mm, "end": v(47.27, -1.2) * mm});
            skLineSegment(sketch, "E971", {"start": v(47.27, -1.2) * mm, "end": v(47.38, -1.1) * mm});
            skLineSegment(sketch, "E972", {"start": v(47.38, -1.1) * mm, "end": v(47.5, -1) * mm});
            skLineSegment(sketch, "E973", {"start": v(47.5, -1) * mm, "end": v(47.64, -0.92) * mm});
            skLineSegment(sketch, "E974", {"start": v(47.64, -0.92) * mm, "end": v(47.78, -0.84) * mm});
            skLineSegment(sketch, "E975", {"start": v(47.78, -0.84) * mm, "end": v(47.92, -0.76) * mm});
            skLineSegment(sketch, "E976", {"start": v(47.92, -0.76) * mm, "end": v(47.96, -0.73) * mm});
            skLineSegment(sketch, "E977", {"start": v(47.96, -0.73) * mm, "end": v(48, -0.7) * mm});
            skLineSegment(sketch, "E978", {"start": v(48, -0.7) * mm, "end": v(48.04, -0.66) * mm});
            skLineSegment(sketch, "E979", {"start": v(48.04, -0.66) * mm, "end": v(48.08, -0.63) * mm});
            skLineSegment(sketch, "E980", {"start": v(48.08, -0.63) * mm, "end": v(48.28, -0.5) * mm});
            skLineSegment(sketch, "E981", {"start": v(48.28, -0.5) * mm, "end": v(48.48, -0.37) * mm});
            skLineSegment(sketch, "E982", {"start": v(48.48, -0.37) * mm, "end": v(48.67, -0.23) * mm});
            skLineSegment(sketch, "E983", {"start": v(48.67, -0.23) * mm, "end": v(48.86, -0.1) * mm});
            skLineSegment(sketch, "E984", {"start": v(48.86, -0.1) * mm, "end": v(49, 0.01) * mm});
            skLineSegment(sketch, "E985", {"start": v(49, 0.01) * mm, "end": v(49.1, 0.12) * mm});
            skLineSegment(sketch, "E986", {"start": v(49.1, 0.12) * mm, "end": v(49.22, 0.24) * mm});
            skLineSegment(sketch, "E987", {"start": v(49.22, 0.24) * mm, "end": v(49.34, 0.36) * mm});
            skLineSegment(sketch, "E988", {"start": v(49.34, 0.36) * mm, "end": v(49.42, 0.44) * mm});
            skLineSegment(sketch, "E989", {"start": v(49.42, 0.44) * mm, "end": v(49.5, 0.52) * mm});
            skLineSegment(sketch, "E990", {"start": v(49.5, 0.52) * mm, "end": v(49.59, 0.6) * mm});
            skLineSegment(sketch, "E991", {"start": v(49.59, 0.6) * mm, "end": v(49.67, 0.68) * mm});
            skLineSegment(sketch, "E992", {"start": v(49.67, 0.68) * mm, "end": v(49.68, 0.67) * mm});
            skLineSegment(sketch, "E993", {"start": v(49.68, 0.67) * mm, "end": v(49.7, 0.66) * mm});
            skLineSegment(sketch, "E994", {"start": v(49.7, 0.66) * mm, "end": v(49.7, 0.65) * mm});
            skLineSegment(sketch, "E995", {"start": v(49.7, 0.65) * mm, "end": v(49.71, 0.65) * mm});
            skLineSegment(sketch, "E996", {"start": v(41.48, 7.12) * mm, "end": v(41.5, 7.13) * mm});
            skLineSegment(sketch, "E997", {"start": v(41.5, 7.13) * mm, "end": v(41.52, 7.13) * mm});
            skLineSegment(sketch, "E998", {"start": v(41.52, 7.13) * mm, "end": v(41.54, 7.14) * mm});
            skLineSegment(sketch, "E999", {"start": v(41.54, 7.14) * mm, "end": v(41.55, 7.14) * mm});
            skLineSegment(sketch, "E1000", {"start": v(41.55, 7.14) * mm, "end": v(42.09, 7.13) * mm});
            skLineSegment(sketch, "E1001", {"start": v(42.09, 7.13) * mm, "end": v(42.63, 7.12) * mm});
            skLineSegment(sketch, "E1002", {"start": v(42.63, 7.12) * mm, "end": v(43.16, 7.11) * mm});
            skLineSegment(sketch, "E1003", {"start": v(43.16, 7.11) * mm, "end": v(43.7, 7.1) * mm});
            skLineSegment(sketch, "E1004", {"start": v(43.7, 7.1) * mm, "end": v(44.12, 7.1) * mm});
            skLineSegment(sketch, "E1005", {"start": v(44.12, 7.1) * mm, "end": v(44.54, 7.1) * mm});
            skLineSegment(sketch, "E1006", {"start": v(44.54, 7.1) * mm, "end": v(44.96, 7.1) * mm});
            skLineSegment(sketch, "E1007", {"start": v(44.96, 7.1) * mm, "end": v(45.37, 7.1) * mm});
            skLineSegment(sketch, "E1008", {"start": v(45.37, 7.1) * mm, "end": v(45.74, 7.1) * mm});
            skLineSegment(sketch, "E1009", {"start": v(45.74, 7.1) * mm, "end": v(46.11, 7.1) * mm});
            skLineSegment(sketch, "E1010", {"start": v(46.11, 7.1) * mm, "end": v(46.48, 7.11) * mm});
            skLineSegment(sketch, "E1011", {"start": v(46.48, 7.11) * mm, "end": v(46.85, 7.11) * mm});
            skLineSegment(sketch, "E1012", {"start": v(46.85, 7.11) * mm, "end": v(47.24, 7.1) * mm});
            skLineSegment(sketch, "E1013", {"start": v(47.24, 7.1) * mm, "end": v(47.64, 7.1) * mm});
            skLineSegment(sketch, "E1014", {"start": v(47.64, 7.1) * mm, "end": v(48.03, 7.1) * mm});
            skLineSegment(sketch, "E1015", {"start": v(48.03, 7.1) * mm, "end": v(48.42, 7.09) * mm});
            skLineSegment(sketch, "E1016", {"start": v(48.42, 7.09) * mm, "end": v(48.65, 7.09) * mm});
            skLineSegment(sketch, "E1017", {"start": v(48.65, 7.09) * mm, "end": v(48.88, 7.09) * mm});
            skLineSegment(sketch, "E1018", {"start": v(48.88, 7.09) * mm, "end": v(49.12, 7.1) * mm});
            skLineSegment(sketch, "E1019", {"start": v(49.12, 7.1) * mm, "end": v(49.35, 7.09) * mm});
            skLineSegment(sketch, "E1020", {"start": v(49.35, 7.09) * mm, "end": v(49.48, 7.06) * mm});
            skLineSegment(sketch, "E1021", {"start": v(49.48, 7.06) * mm, "end": v(49.58, 7) * mm});
            skLineSegment(sketch, "E1022", {"start": v(49.58, 7) * mm, "end": v(49.66, 6.9) * mm});
            skLineSegment(sketch, "E1023", {"start": v(49.66, 6.9) * mm, "end": v(49.73, 6.76) * mm});
            skLineSegment(sketch, "E1024", {"start": v(49.73, 6.76) * mm, "end": v(49.68, 6.78) * mm});
            skLineSegment(sketch, "E1025", {"start": v(49.68, 6.78) * mm, "end": v(49.64, 6.8) * mm});
            skLineSegment(sketch, "E1026", {"start": v(49.64, 6.8) * mm, "end": v(49.6, 6.8) * mm});
            skLineSegment(sketch, "E1027", {"start": v(49.6, 6.8) * mm, "end": v(49.58, 6.82) * mm});
            skLineSegment(sketch, "E1028", {"start": v(49.58, 6.82) * mm, "end": v(49.47, 6.9) * mm});
            skLineSegment(sketch, "E1029", {"start": v(49.47, 6.9) * mm, "end": v(49.37, 6.93) * mm});
            skLineSegment(sketch, "E1030", {"start": v(49.37, 6.93) * mm, "end": v(49.25, 6.92) * mm});
            skLineSegment(sketch, "E1031", {"start": v(49.25, 6.92) * mm, "end": v(49.13, 6.9) * mm});
            skLineSegment(sketch, "E1032", {"start": v(49.13, 6.9) * mm, "end": v(49.03, 6.86) * mm});
            skLineSegment(sketch, "E1033", {"start": v(49.03, 6.86) * mm, "end": v(48.93, 6.83) * mm});
            skLineSegment(sketch, "E1034", {"start": v(48.93, 6.83) * mm, "end": v(48.83, 6.78) * mm});
            skLineSegment(sketch, "E1035", {"start": v(48.83, 6.78) * mm, "end": v(48.74, 6.7) * mm});
            skLineSegment(sketch, "E1036", {"start": v(48.74, 6.7) * mm, "end": v(48.67, 6.58) * mm});
            skLineSegment(sketch, "E1037", {"start": v(48.67, 6.58) * mm, "end": v(48.63, 6.42) * mm});
            skLineSegment(sketch, "E1038", {"start": v(48.63, 6.42) * mm, "end": v(48.63, 6.25) * mm});
            skLineSegment(sketch, "E1039", {"start": v(48.63, 6.25) * mm, "end": v(48.67, 6.08) * mm});
            skLineSegment(sketch, "E1040", {"start": v(48.67, 6.08) * mm, "end": v(48.73, 5.97) * mm});
            skLineSegment(sketch, "E1041", {"start": v(48.73, 5.97) * mm, "end": v(48.83, 5.9) * mm});
            skLineSegment(sketch, "E1042", {"start": v(48.83, 5.9) * mm, "end": v(48.96, 5.86) * mm});
            skLineSegment(sketch, "E1043", {"start": v(48.96, 5.86) * mm, "end": v(49.1, 5.86) * mm});
            skLineSegment(sketch, "E1044", {"start": v(49.1, 5.86) * mm, "end": v(49.15, 5.87) * mm});
            skLineSegment(sketch, "E1045", {"start": v(49.15, 5.87) * mm, "end": v(49.21, 5.9) * mm});
            skLineSegment(sketch, "E1046", {"start": v(49.21, 5.9) * mm, "end": v(49.26, 5.93) * mm});
            skLineSegment(sketch, "E1047", {"start": v(49.26, 5.93) * mm, "end": v(49.28, 5.96) * mm});
            skLineSegment(sketch, "E1048", {"start": v(49.28, 5.96) * mm, "end": v(49.29, 6.02) * mm});
            skLineSegment(sketch, "E1049", {"start": v(49.29, 6.02) * mm, "end": v(49.28, 6.09) * mm});
            skLineSegment(sketch, "E1050", {"start": v(49.28, 6.09) * mm, "end": v(49.26, 6.15) * mm});
            skLineSegment(sketch, "E1051", {"start": v(49.26, 6.15) * mm, "end": v(49.24, 6.22) * mm});
            skLineSegment(sketch, "E1052", {"start": v(49.24, 6.22) * mm, "end": v(49.22, 6.27) * mm});
            skLineSegment(sketch, "E1053", {"start": v(49.22, 6.27) * mm, "end": v(49.2, 6.32) * mm});
            skLineSegment(sketch, "E1054", {"start": v(49.2, 6.32) * mm, "end": v(49.18, 6.37) * mm});
            skLineSegment(sketch, "E1055", {"start": v(49.18, 6.37) * mm, "end": v(49.17, 6.42) * mm});
            skLineSegment(sketch, "E1056", {"start": v(49.17, 6.42) * mm, "end": v(49.22, 6.42) * mm});
            skLineSegment(sketch, "E1057", {"start": v(49.22, 6.42) * mm, "end": v(49.27, 6.41) * mm});
            skLineSegment(sketch, "E1058", {"start": v(49.27, 6.41) * mm, "end": v(49.33, 6.41) * mm});
            skLineSegment(sketch, "E1059", {"start": v(49.33, 6.41) * mm, "end": v(49.38, 6.4) * mm});
            skLineSegment(sketch, "E1060", {"start": v(49.38, 6.4) * mm, "end": v(49.5, 6.34) * mm});
            skLineSegment(sketch, "E1061", {"start": v(49.5, 6.34) * mm, "end": v(49.59, 6.26) * mm});
            skLineSegment(sketch, "E1062", {"start": v(49.59, 6.26) * mm, "end": v(49.63, 6.14) * mm});
            skLineSegment(sketch, "E1063", {"start": v(49.63, 6.14) * mm, "end": v(49.64, 6) * mm});
            skLineSegment(sketch, "E1064", {"start": v(49.64, 6) * mm, "end": v(49.61, 5.75) * mm});
            skLineSegment(sketch, "E1065", {"start": v(49.61, 5.75) * mm, "end": v(49.53, 5.53) * mm});
            skLineSegment(sketch, "E1066", {"start": v(49.53, 5.53) * mm, "end": v(49.4, 5.35) * mm});
            skLineSegment(sketch, "E1067", {"start": v(49.4, 5.35) * mm, "end": v(49.18, 5.22) * mm});
            skLineSegment(sketch, "E1068", {"start": v(49.18, 5.22) * mm, "end": v(48.95, 5.14) * mm});
            skLineSegment(sketch, "E1069", {"start": v(48.95, 5.14) * mm, "end": v(48.71, 5.11) * mm});
            skLineSegment(sketch, "E1070", {"start": v(48.71, 5.11) * mm, "end": v(48.48, 5.14) * mm});
            skLineSegment(sketch, "E1071", {"start": v(48.48, 5.14) * mm, "end": v(48.26, 5.25) * mm});
            skLineSegment(sketch, "E1072", {"start": v(48.26, 5.25) * mm, "end": v(47.94, 5.47) * mm});
            skLineSegment(sketch, "E1073", {"start": v(47.94, 5.47) * mm, "end": v(47.64, 5.71) * mm});
            skLineSegment(sketch, "E1074", {"start": v(47.64, 5.71) * mm, "end": v(47.34, 5.96) * mm});
            skLineSegment(sketch, "E1075", {"start": v(47.34, 5.96) * mm, "end": v(47.05, 6.2) * mm});
            skLineSegment(sketch, "E1076", {"start": v(47.05, 6.2) * mm, "end": v(46.8, 6.43) * mm});
            skLineSegment(sketch, "E1077", {"start": v(46.8, 6.43) * mm, "end": v(46.52, 6.63) * mm});
            skLineSegment(sketch, "E1078", {"start": v(46.52, 6.63) * mm, "end": v(46.24, 6.8) * mm});
            skLineSegment(sketch, "E1079", {"start": v(46.24, 6.8) * mm, "end": v(45.92, 6.9) * mm});
            skLineSegment(sketch, "E1080", {"start": v(45.92, 6.9) * mm, "end": v(45.32, 6.98) * mm});
            skLineSegment(sketch, "E1081", {"start": v(45.32, 6.98) * mm, "end": v(44.75, 6.86) * mm});
            skLineSegment(sketch, "E1082", {"start": v(44.75, 6.86) * mm, "end": v(44.26, 6.54) * mm});
            skLineSegment(sketch, "E1083", {"start": v(44.26, 6.54) * mm, "end": v(43.86, 6) * mm});
            skLineSegment(sketch, "E1084", {"start": v(43.86, 6) * mm, "end": v(43.76, 5.8) * mm});
            skLineSegment(sketch, "E1085", {"start": v(43.76, 5.8) * mm, "end": v(43.66, 5.6) * mm});
            skLineSegment(sketch, "E1086", {"start": v(43.66, 5.6) * mm, "end": v(43.56, 5.4) * mm});
            skLineSegment(sketch, "E1087", {"start": v(43.56, 5.4) * mm, "end": v(43.44, 5.2) * mm});
            skLineSegment(sketch, "E1088", {"start": v(43.44, 5.2) * mm, "end": v(43.38, 5.12) * mm});
            skLineSegment(sketch, "E1089", {"start": v(43.38, 5.12) * mm, "end": v(43.3, 5.04) * mm});
            skLineSegment(sketch, "E1090", {"start": v(43.3, 5.04) * mm, "end": v(43.2, 4.96) * mm});
            skLineSegment(sketch, "E1091", {"start": v(43.2, 4.96) * mm, "end": v(43.11, 4.9) * mm});
            skLineSegment(sketch, "E1092", {"start": v(43.11, 4.9) * mm, "end": v(42.92, 4.82) * mm});
            skLineSegment(sketch, "E1093", {"start": v(42.92, 4.82) * mm, "end": v(42.72, 4.84) * mm});
            skLineSegment(sketch, "E1094", {"start": v(42.72, 4.84) * mm, "end": v(42.54, 4.92) * mm});
            skLineSegment(sketch, "E1095", {"start": v(42.54, 4.92) * mm, "end": v(42.41, 5.06) * mm});
            skLineSegment(sketch, "E1096", {"start": v(42.41, 5.06) * mm, "end": v(42.34, 5.2) * mm});
            skLineSegment(sketch, "E1097", {"start": v(42.34, 5.2) * mm, "end": v(42.27, 5.33) * mm});
            skLineSegment(sketch, "E1098", {"start": v(42.27, 5.33) * mm, "end": v(42.22, 5.47) * mm});
            skLineSegment(sketch, "E1099", {"start": v(42.22, 5.47) * mm, "end": v(42.17, 5.62) * mm});
            skLineSegment(sketch, "E1100", {"start": v(42.17, 5.62) * mm, "end": v(42.09, 5.9) * mm});
            skLineSegment(sketch, "E1101", {"start": v(42.09, 5.9) * mm, "end": v(42, 6.16) * mm});
            skLineSegment(sketch, "E1102", {"start": v(42, 6.16) * mm, "end": v(41.93, 6.43) * mm});
            skLineSegment(sketch, "E1103", {"start": v(41.93, 6.43) * mm, "end": v(41.84, 6.7) * mm});
            skLineSegment(sketch, "E1104", {"start": v(41.84, 6.7) * mm, "end": v(41.8, 6.78) * mm});
            skLineSegment(sketch, "E1105", {"start": v(41.8, 6.78) * mm, "end": v(41.72, 6.86) * mm});
            skLineSegment(sketch, "E1106", {"start": v(41.72, 6.86) * mm, "end": v(41.65, 6.93) * mm});
            skLineSegment(sketch, "E1107", {"start": v(41.65, 6.93) * mm, "end": v(41.57, 7) * mm});
            skLineSegment(sketch, "E1108", {"start": v(41.57, 7) * mm, "end": v(41.54, 7.02) * mm});
            skLineSegment(sketch, "E1109", {"start": v(41.54, 7.02) * mm, "end": v(41.5, 7.04) * mm});
            skLineSegment(sketch, "E1110", {"start": v(41.5, 7.04) * mm, "end": v(41.47, 7.05) * mm});
            skLineSegment(sketch, "E1111", {"start": v(41.47, 7.05) * mm, "end": v(41.44, 7.07) * mm});
            skLineSegment(sketch, "E1112", {"start": v(41.44, 7.07) * mm, "end": v(41.45, 7.08) * mm});
            skLineSegment(sketch, "E1113", {"start": v(41.45, 7.08) * mm, "end": v(41.46, 7.1) * mm});
            skLineSegment(sketch, "E1114", {"start": v(41.46, 7.1) * mm, "end": v(41.47, 7.1) * mm});
            skLineSegment(sketch, "E1115", {"start": v(41.47, 7.1) * mm, "end": v(41.48, 7.12) * mm});
            skLineSegment(sketch, "E1116", {"start": v(35.93, 2.66) * mm, "end": v(35.82, 3.08) * mm});
            skLineSegment(sketch, "E1117", {"start": v(35.82, 3.08) * mm, "end": v(35.62, 3.43) * mm});
            skLineSegment(sketch, "E1118", {"start": v(35.62, 3.43) * mm, "end": v(35.34, 3.72) * mm});
            skLineSegment(sketch, "E1119", {"start": v(35.34, 3.72) * mm, "end": v(35.02, 3.96) * mm});
            skLineSegment(sketch, "E1120", {"start": v(35.02, 3.96) * mm, "end": v(34.71, 4.2) * mm});
            skLineSegment(sketch, "E1121", {"start": v(34.71, 4.2) * mm, "end": v(34.47, 4.46) * mm});
            skLineSegment(sketch, "E1122", {"start": v(34.47, 4.46) * mm, "end": v(34.28, 4.77) * mm});
            skLineSegment(sketch, "E1123", {"start": v(34.28, 4.77) * mm, "end": v(34.16, 5.12) * mm});
            skLineSegment(sketch, "E1124", {"start": v(34.16, 5.12) * mm, "end": v(34.15, 5.27) * mm});
            skLineSegment(sketch, "E1125", {"start": v(34.15, 5.27) * mm, "end": v(34.16, 5.43) * mm});
            skLineSegment(sketch, "E1126", {"start": v(34.16, 5.43) * mm, "end": v(34.19, 5.6) * mm});
            skLineSegment(sketch, "E1127", {"start": v(34.19, 5.6) * mm, "end": v(34.21, 5.75) * mm});
            skLineSegment(sketch, "E1128", {"start": v(34.21, 5.75) * mm, "end": v(34.24, 5.93) * mm});
            skLineSegment(sketch, "E1129", {"start": v(34.24, 5.93) * mm, "end": v(34.3, 6.1) * mm});
            skLineSegment(sketch, "E1130", {"start": v(34.3, 6.1) * mm, "end": v(34.38, 6.27) * mm});
            skLineSegment(sketch, "E1131", {"start": v(34.38, 6.27) * mm, "end": v(34.5, 6.43) * mm});
            skLineSegment(sketch, "E1132", {"start": v(34.5, 6.43) * mm, "end": v(34.93, 6.8) * mm});
            skLineSegment(sketch, "E1133", {"start": v(34.93, 6.8) * mm, "end": v(35.46, 6.98) * mm});
            skLineSegment(sketch, "E1134", {"start": v(35.46, 6.98) * mm, "end": v(36.02, 6.94) * mm});
            skLineSegment(sketch, "E1135", {"start": v(36.02, 6.94) * mm, "end": v(36.55, 6.6) * mm});
            skLineSegment(sketch, "E1136", {"start": v(36.55, 6.6) * mm, "end": v(36.7, 6.43) * mm});
            skLineSegment(sketch, "E1137", {"start": v(36.7, 6.43) * mm, "end": v(36.85, 6.26) * mm});
            skLineSegment(sketch, "E1138", {"start": v(36.85, 6.26) * mm, "end": v(36.96, 6.06) * mm});
            skLineSegment(sketch, "E1139", {"start": v(36.96, 6.06) * mm, "end": v(37.04, 5.84) * mm});
            skLineSegment(sketch, "E1140", {"start": v(37.04, 5.84) * mm, "end": v(37.08, 5.59) * mm});
            skLineSegment(sketch, "E1141", {"start": v(37.08, 5.59) * mm, "end": v(37.06, 5.34) * mm});
            skLineSegment(sketch, "E1142", {"start": v(37.06, 5.34) * mm, "end": v(37, 5.1) * mm});
            skLineSegment(sketch, "E1143", {"start": v(37, 5.1) * mm, "end": v(36.92, 4.86) * mm});
            skLineSegment(sketch, "E1144", {"start": v(36.92, 4.86) * mm, "end": v(36.82, 4.58) * mm});
            skLineSegment(sketch, "E1145", {"start": v(36.82, 4.58) * mm, "end": v(36.71, 4.3) * mm});
            skLineSegment(sketch, "E1146", {"start": v(36.71, 4.3) * mm, "end": v(36.6, 4.02) * mm});
            skLineSegment(sketch, "E1147", {"start": v(36.6, 4.02) * mm, "end": v(36.5, 3.74) * mm});
            skLineSegment(sketch, "E1148", {"start": v(36.5, 3.74) * mm, "end": v(36.36, 3.47) * mm});
            skLineSegment(sketch, "E1149", {"start": v(36.36, 3.47) * mm, "end": v(36.23, 3.2) * mm});
            skLineSegment(sketch, "E1150", {"start": v(36.23, 3.2) * mm, "end": v(36.08, 2.94) * mm});
            skLineSegment(sketch, "E1151", {"start": v(36.08, 2.94) * mm, "end": v(35.93, 2.66) * mm});
            skLineSegment(sketch, "E1152", {"start": v(25.81, -4.21) * mm, "end": v(25.81, -2.7) * mm});
            skLineSegment(sketch, "E1153", {"start": v(25.81, -2.7) * mm, "end": v(25.81, -1.18) * mm});
            skLineSegment(sketch, "E1154", {"start": v(25.81, -1.18) * mm, "end": v(25.81, 0.34) * mm});
            skLineSegment(sketch, "E1155", {"start": v(25.81, 0.34) * mm, "end": v(25.81, 1.86) * mm});
            skLineSegment(sketch, "E1156", {"start": v(25.81, 1.86) * mm, "end": v(25.82, 1.86) * mm});
            skLineSegment(sketch, "E1157", {"start": v(25.82, 1.86) * mm, "end": v(25.83, 1.86) * mm});
            skLineSegment(sketch, "E1158", {"start": v(25.83, 1.86) * mm, "end": v(25.84, 1.86) * mm});
            skLineSegment(sketch, "E1159", {"start": v(25.84, 1.86) * mm, "end": v(25.85, 1.87) * mm});
            skLineSegment(sketch, "E1160", {"start": v(25.85, 1.87) * mm, "end": v(25.86, 1.84) * mm});
            skLineSegment(sketch, "E1161", {"start": v(25.86, 1.84) * mm, "end": v(25.87, 1.82) * mm});
            skLineSegment(sketch, "E1162", {"start": v(25.87, 1.82) * mm, "end": v(25.89, 1.8) * mm});
            skLineSegment(sketch, "E1163", {"start": v(25.89, 1.8) * mm, "end": v(25.9, 1.77) * mm});
            skLineSegment(sketch, "E1164", {"start": v(25.9, 1.77) * mm, "end": v(26.14, 1.21) * mm});
            skLineSegment(sketch, "E1165", {"start": v(26.14, 1.21) * mm, "end": v(26.38, 0.65) * mm});
            skLineSegment(sketch, "E1166", {"start": v(26.38, 0.65) * mm, "end": v(26.62, 0.1) * mm});
            skLineSegment(sketch, "E1167", {"start": v(26.62, 0.1) * mm, "end": v(26.87, -0.47) * mm});
            skLineSegment(sketch, "E1168", {"start": v(26.87, -0.47) * mm, "end": v(27.11, -1.01) * mm});
            skLineSegment(sketch, "E1169", {"start": v(27.11, -1.01) * mm, "end": v(27.37, -1.56) * mm});
            skLineSegment(sketch, "E1170", {"start": v(27.37, -1.56) * mm, "end": v(27.63, -2.1) * mm});
            skLineSegment(sketch, "E1171", {"start": v(27.63, -2.1) * mm, "end": v(27.88, -2.65) * mm});
            skLineSegment(sketch, "E1172", {"start": v(27.88, -2.65) * mm, "end": v(27.9, -2.68) * mm});
            skLineSegment(sketch, "E1173", {"start": v(27.9, -2.68) * mm, "end": v(27.91, -2.7) * mm});
            skLineSegment(sketch, "E1174", {"start": v(27.91, -2.7) * mm, "end": v(27.93, -2.73) * mm});
            skLineSegment(sketch, "E1175", {"start": v(27.93, -2.73) * mm, "end": v(27.94, -2.76) * mm});
            skLineSegment(sketch, "E1176", {"start": v(27.94, -2.76) * mm, "end": v(28.06, -2.95) * mm});
            skLineSegment(sketch, "E1177", {"start": v(28.06, -2.95) * mm, "end": v(28.1, -3.15) * mm});
            skLineSegment(sketch, "E1178", {"start": v(28.1, -3.15) * mm, "end": v(28.08, -3.35) * mm});
            skLineSegment(sketch, "E1179", {"start": v(28.08, -3.35) * mm, "end": v(28, -3.56) * mm});
            skLineSegment(sketch, "E1180", {"start": v(28, -3.56) * mm, "end": v(27.95, -3.67) * mm});
            skLineSegment(sketch, "E1181", {"start": v(27.95, -3.67) * mm, "end": v(27.92, -3.79) * mm});
            skLineSegment(sketch, "E1182", {"start": v(27.92, -3.79) * mm, "end": v(27.9, -3.91) * mm});
            skLineSegment(sketch, "E1183", {"start": v(27.9, -3.91) * mm, "end": v(27.86, -4.04) * mm});
            skLineSegment(sketch, "E1184", {"start": v(27.86, -4.04) * mm, "end": v(27.84, -4.07) * mm});
            skLineSegment(sketch, "E1185", {"start": v(27.84, -4.07) * mm, "end": v(27.81, -4.1) * mm});
            skLineSegment(sketch, "E1186", {"start": v(27.81, -4.1) * mm, "end": v(27.78, -4.14) * mm});
            skLineSegment(sketch, "E1187", {"start": v(27.78, -4.14) * mm, "end": v(27.75, -4.15) * mm});
            skLineSegment(sketch, "E1188", {"start": v(27.75, -4.15) * mm, "end": v(27.28, -4.18) * mm});
            skLineSegment(sketch, "E1189", {"start": v(27.28, -4.18) * mm, "end": v(26.82, -4.2) * mm});
            skLineSegment(sketch, "E1190", {"start": v(26.82, -4.2) * mm, "end": v(26.35, -4.22) * mm});
            skLineSegment(sketch, "E1191", {"start": v(26.35, -4.22) * mm, "end": v(25.88, -4.24) * mm});
            skLineSegment(sketch, "E1192", {"start": v(25.88, -4.24) * mm, "end": v(25.87, -4.24) * mm});
            skLineSegment(sketch, "E1193", {"start": v(25.87, -4.24) * mm, "end": v(25.86, -4.23) * mm});
            skLineSegment(sketch, "E1194", {"start": v(25.86, -4.23) * mm, "end": v(25.84, -4.22) * mm});
            skLineSegment(sketch, "E1195", {"start": v(25.84, -4.22) * mm, "end": v(25.81, -4.21) * mm});
            skLineSegment(sketch, "E1196", {"start": v(26.85, 3.1) * mm, "end": v(27.16, 2.77) * mm});
            skLineSegment(sketch, "E1197", {"start": v(27.16, 2.77) * mm, "end": v(27.46, 2.44) * mm});
            skLineSegment(sketch, "E1198", {"start": v(27.46, 2.44) * mm, "end": v(27.77, 2.1) * mm});
            skLineSegment(sketch, "E1199", {"start": v(27.77, 2.1) * mm, "end": v(28.1, 1.78) * mm});
            skLineSegment(sketch, "E1200", {"start": v(28.1, 1.78) * mm, "end": v(28.36, 1.55) * mm});
            skLineSegment(sketch, "E1201", {"start": v(28.36, 1.55) * mm, "end": v(28.63, 1.33) * mm});
            skLineSegment(sketch, "E1202", {"start": v(28.63, 1.33) * mm, "end": v(28.91, 1.1) * mm});
            skLineSegment(sketch, "E1203", {"start": v(28.91, 1.1) * mm, "end": v(29.19, 0.89) * mm});
            skLineSegment(sketch, "E1204", {"start": v(29.19, 0.89) * mm, "end": v(29.32, 0.77) * mm});
            skLineSegment(sketch, "E1205", {"start": v(29.32, 0.77) * mm, "end": v(29.45, 0.65) * mm});
            skLineSegment(sketch, "E1206", {"start": v(29.45, 0.65) * mm, "end": v(29.58, 0.53) * mm});
            skLineSegment(sketch, "E1207", {"start": v(29.58, 0.53) * mm, "end": v(29.7, 0.4) * mm});
            skLineSegment(sketch, "E1208", {"start": v(29.7, 0.4) * mm, "end": v(29.9, 0.22) * mm});
            skLineSegment(sketch, "E1209", {"start": v(29.9, 0.22) * mm, "end": v(30.1, 0.04) * mm});
            skLineSegment(sketch, "E1210", {"start": v(30.1, 0.04) * mm, "end": v(30.3, -0.15) * mm});
            skLineSegment(sketch, "E1211", {"start": v(30.3, -0.15) * mm, "end": v(30.5, -0.34) * mm});
            skLineSegment(sketch, "E1212", {"start": v(30.5, -0.34) * mm, "end": v(30.56, -0.4) * mm});
            skLineSegment(sketch, "E1213", {"start": v(30.56, -0.4) * mm, "end": v(30.62, -0.47) * mm});
            skLineSegment(sketch, "E1214", {"start": v(30.62, -0.47) * mm, "end": v(30.68, -0.54) * mm});
            skLineSegment(sketch, "E1215", {"start": v(30.68, -0.54) * mm, "end": v(30.73, -0.62) * mm});
            skLineSegment(sketch, "E1216", {"start": v(30.73, -0.62) * mm, "end": v(30.76, -0.66) * mm});
            skLineSegment(sketch, "E1217", {"start": v(30.76, -0.66) * mm, "end": v(30.78, -0.72) * mm});
            skLineSegment(sketch, "E1218", {"start": v(30.78, -0.72) * mm, "end": v(30.8, -0.77) * mm});
            skLineSegment(sketch, "E1219", {"start": v(30.8, -0.77) * mm, "end": v(30.83, -0.83) * mm});
            skLineSegment(sketch, "E1220", {"start": v(30.83, -0.83) * mm, "end": v(30.7, -0.84) * mm});
            skLineSegment(sketch, "E1221", {"start": v(30.7, -0.84) * mm, "end": v(30.6, -0.85) * mm});
            skLineSegment(sketch, "E1222", {"start": v(30.6, -0.85) * mm, "end": v(30.49, -0.86) * mm});
            skLineSegment(sketch, "E1223", {"start": v(30.49, -0.86) * mm, "end": v(30.38, -0.87) * mm});
            skLineSegment(sketch, "E1224", {"start": v(30.38, -0.87) * mm, "end": v(30.14, -0.94) * mm});
            skLineSegment(sketch, "E1225", {"start": v(30.14, -0.94) * mm, "end": v(29.92, -1.06) * mm});
            skLineSegment(sketch, "E1226", {"start": v(29.92, -1.06) * mm, "end": v(29.73, -1.22) * mm});
            skLineSegment(sketch, "E1227", {"start": v(29.73, -1.22) * mm, "end": v(29.56, -1.4) * mm});
            skLineSegment(sketch, "E1228", {"start": v(29.56, -1.4) * mm, "end": v(29.48, -1.49) * mm});
            skLineSegment(sketch, "E1229", {"start": v(29.48, -1.49) * mm, "end": v(29.4, -1.56) * mm});
            skLineSegment(sketch, "E1230", {"start": v(29.4, -1.56) * mm, "end": v(29.32, -1.64) * mm});
            skLineSegment(sketch, "E1231", {"start": v(29.32, -1.64) * mm, "end": v(29.24, -1.7) * mm});
            skLineSegment(sketch, "E1232", {"start": v(29.24, -1.7) * mm, "end": v(29.18, -1.75) * mm});
            skLineSegment(sketch, "E1233", {"start": v(29.18, -1.75) * mm, "end": v(29.13, -1.76) * mm});
            skLineSegment(sketch, "E1234", {"start": v(29.13, -1.76) * mm, "end": v(29.08, -1.73) * mm});
            skLineSegment(sketch, "E1235", {"start": v(29.08, -1.73) * mm, "end": v(29.03, -1.67) * mm});
            skLineSegment(sketch, "E1236", {"start": v(29.03, -1.67) * mm, "end": v(28.76, -1.13) * mm});
            skLineSegment(sketch, "E1237", {"start": v(28.76, -1.13) * mm, "end": v(28.48, -0.59) * mm});
            skLineSegment(sketch, "E1238", {"start": v(28.48, -0.59) * mm, "end": v(28.2, -0.05) * mm});
            skLineSegment(sketch, "E1239", {"start": v(28.2, -0.05) * mm, "end": v(27.94, 0.5) * mm});
            skLineSegment(sketch, "E1240", {"start": v(27.94, 0.5) * mm, "end": v(27.67, 1.08) * mm});
            skLineSegment(sketch, "E1241", {"start": v(27.67, 1.08) * mm, "end": v(27.42, 1.67) * mm});
            skLineSegment(sketch, "E1242", {"start": v(27.42, 1.67) * mm, "end": v(27.16, 2.27) * mm});
            skLineSegment(sketch, "E1243", {"start": v(27.16, 2.27) * mm, "end": v(26.91, 2.86) * mm});
            skLineSegment(sketch, "E1244", {"start": v(26.91, 2.86) * mm, "end": v(26.9, 2.92) * mm});
            skLineSegment(sketch, "E1245", {"start": v(26.9, 2.92) * mm, "end": v(26.88, 2.99) * mm});
            skLineSegment(sketch, "E1246", {"start": v(26.88, 2.99) * mm, "end": v(26.87, 3.05) * mm});
            skLineSegment(sketch, "E1247", {"start": v(26.87, 3.05) * mm, "end": v(26.85, 3.1) * mm});
            skLineSegment(sketch, "E1248", {"start": v(39.71, -30.34) * mm, "end": v(39.29, -30.15) * mm});
            skLineSegment(sketch, "E1249", {"start": v(39.29, -30.15) * mm, "end": v(38.91, -29.9) * mm});
            skLineSegment(sketch, "E1250", {"start": v(38.91, -29.9) * mm, "end": v(38.62, -29.58) * mm});
            skLineSegment(sketch, "E1251", {"start": v(38.62, -29.58) * mm, "end": v(38.46, -29.12) * mm});
            skLineSegment(sketch, "E1252", {"start": v(38.46, -29.12) * mm, "end": v(38.45, -29.06) * mm});
            skLineSegment(sketch, "E1253", {"start": v(38.45, -29.06) * mm, "end": v(38.44, -29) * mm});
            skLineSegment(sketch, "E1254", {"start": v(38.44, -29) * mm, "end": v(38.45, -28.93) * mm});
            skLineSegment(sketch, "E1255", {"start": v(38.45, -28.93) * mm, "end": v(38.45, -28.86) * mm});
            skLineSegment(sketch, "E1256", {"start": v(38.45, -28.86) * mm, "end": v(38.5, -28.66) * mm});
            skLineSegment(sketch, "E1257", {"start": v(38.5, -28.66) * mm, "end": v(38.57, -28.45) * mm});
            skLineSegment(sketch, "E1258", {"start": v(38.57, -28.45) * mm, "end": v(38.62, -28.24) * mm});
            skLineSegment(sketch, "E1259", {"start": v(38.62, -28.24) * mm, "end": v(38.66, -28.03) * mm});
            skLineSegment(sketch, "E1260", {"start": v(38.66, -28.03) * mm, "end": v(38.7, -27.7) * mm});
            skLineSegment(sketch, "E1261", {"start": v(38.7, -27.7) * mm, "end": v(38.7, -27.36) * mm});
            skLineSegment(sketch, "E1262", {"start": v(38.7, -27.36) * mm, "end": v(38.6, -27.04) * mm});
            skLineSegment(sketch, "E1263", {"start": v(38.6, -27.04) * mm, "end": v(38.4, -26.75) * mm});
            skLineSegment(sketch, "E1264", {"start": v(38.4, -26.75) * mm, "end": v(38.26, -26.6) * mm});
            skLineSegment(sketch, "E1265", {"start": v(38.26, -26.6) * mm, "end": v(38.12, -26.45) * mm});
            skLineSegment(sketch, "E1266", {"start": v(38.12, -26.45) * mm, "end": v(37.96, -26.34) * mm});
            skLineSegment(sketch, "E1267", {"start": v(37.96, -26.34) * mm, "end": v(37.76, -26.3) * mm});
            skLineSegment(sketch, "E1268", {"start": v(37.76, -26.3) * mm, "end": v(37.48, -26.3) * mm});
            skLineSegment(sketch, "E1269", {"start": v(37.48, -26.3) * mm, "end": v(37.2, -26.3) * mm});
            skLineSegment(sketch, "E1270", {"start": v(37.2, -26.3) * mm, "end": v(36.91, -26.32) * mm});
            skLineSegment(sketch, "E1271", {"start": v(36.91, -26.32) * mm, "end": v(36.63, -26.36) * mm});
            skLineSegment(sketch, "E1272", {"start": v(36.63, -26.36) * mm, "end": v(36.32, -26.41) * mm});
            skLineSegment(sketch, "E1273", {"start": v(36.32, -26.41) * mm, "end": v(36.02, -26.49) * mm});
            skLineSegment(sketch, "E1274", {"start": v(36.02, -26.49) * mm, "end": v(35.71, -26.57) * mm});
            skLineSegment(sketch, "E1275", {"start": v(35.71, -26.57) * mm, "end": v(35.41, -26.67) * mm});
            skLineSegment(sketch, "E1276", {"start": v(35.41, -26.67) * mm, "end": v(35.23, -26.75) * mm});
            skLineSegment(sketch, "E1277", {"start": v(35.23, -26.75) * mm, "end": v(35.05, -26.84) * mm});
            skLineSegment(sketch, "E1278", {"start": v(35.05, -26.84) * mm, "end": v(34.88, -26.94) * mm});
            skLineSegment(sketch, "E1279", {"start": v(34.88, -26.94) * mm, "end": v(34.7, -27.05) * mm});
            skLineSegment(sketch, "E1280", {"start": v(34.7, -27.05) * mm, "end": v(34.5, -27.15) * mm});
            skLineSegment(sketch, "E1281", {"start": v(34.5, -27.15) * mm, "end": v(34.31, -27.26) * mm});
            skLineSegment(sketch, "E1282", {"start": v(34.31, -27.26) * mm, "end": v(34.1, -27.36) * mm});
            skLineSegment(sketch, "E1283", {"start": v(34.1, -27.36) * mm, "end": v(33.9, -27.45) * mm});
            skLineSegment(sketch, "E1284", {"start": v(33.9, -27.45) * mm, "end": v(33.98, -27.37) * mm});
            skLineSegment(sketch, "E1285", {"start": v(33.98, -27.37) * mm, "end": v(34.07, -27.3) * mm});
            skLineSegment(sketch, "E1286", {"start": v(34.07, -27.3) * mm, "end": v(34.16, -27.22) * mm});
            skLineSegment(sketch, "E1287", {"start": v(34.16, -27.22) * mm, "end": v(34.25, -27.15) * mm});
            skLineSegment(sketch, "E1288", {"start": v(34.25, -27.15) * mm, "end": v(34.45, -27.02) * mm});
            skLineSegment(sketch, "E1289", {"start": v(34.45, -27.02) * mm, "end": v(34.65, -26.9) * mm});
            skLineSegment(sketch, "E1290", {"start": v(34.65, -26.9) * mm, "end": v(34.85, -26.78) * mm});
            skLineSegment(sketch, "E1291", {"start": v(34.85, -26.78) * mm, "end": v(35.05, -26.67) * mm});
            skLineSegment(sketch, "E1292", {"start": v(35.05, -26.67) * mm, "end": v(35.38, -26.5) * mm});
            skLineSegment(sketch, "E1293", {"start": v(35.38, -26.5) * mm, "end": v(35.71, -26.36) * mm});
            skLineSegment(sketch, "E1294", {"start": v(35.71, -26.36) * mm, "end": v(36.05, -26.23) * mm});
            skLineSegment(sketch, "E1295", {"start": v(36.05, -26.23) * mm, "end": v(36.4, -26.1) * mm});
            skLineSegment(sketch, "E1296", {"start": v(36.4, -26.1) * mm, "end": v(36.77, -26) * mm});
            skLineSegment(sketch, "E1297", {"start": v(36.77, -26) * mm, "end": v(37.15, -25.93) * mm});
            skLineSegment(sketch, "E1298", {"start": v(37.15, -25.93) * mm, "end": v(37.53, -25.9) * mm});
            skLineSegment(sketch, "E1299", {"start": v(37.53, -25.9) * mm, "end": v(37.91, -25.9) * mm});
            skLineSegment(sketch, "E1300", {"start": v(37.91, -25.9) * mm, "end": v(38.15, -25.94) * mm});
            skLineSegment(sketch, "E1301", {"start": v(38.15, -25.94) * mm, "end": v(38.36, -26.03) * mm});
            skLineSegment(sketch, "E1302", {"start": v(38.36, -26.03) * mm, "end": v(38.55, -26.16) * mm});
            skLineSegment(sketch, "E1303", {"start": v(38.55, -26.16) * mm, "end": v(38.72, -26.31) * mm});
            skLineSegment(sketch, "E1304", {"start": v(38.72, -26.31) * mm, "end": v(38.94, -26.6) * mm});
            skLineSegment(sketch, "E1305", {"start": v(38.94, -26.6) * mm, "end": v(39.03, -26.93) * mm});
            skLineSegment(sketch, "E1306", {"start": v(39.03, -26.93) * mm, "end": v(39.03, -27.27) * mm});
            skLineSegment(sketch, "E1307", {"start": v(39.03, -27.27) * mm, "end": v(38.98, -27.62) * mm});
            skLineSegment(sketch, "E1308", {"start": v(38.98, -27.62) * mm, "end": v(38.92, -28.08) * mm});
            skLineSegment(sketch, "E1309", {"start": v(38.92, -28.08) * mm, "end": v(38.9, -28.53) * mm});
            skLineSegment(sketch, "E1310", {"start": v(38.9, -28.53) * mm, "end": v(38.95, -28.98) * mm});
            skLineSegment(sketch, "E1311", {"start": v(38.95, -28.98) * mm, "end": v(39.08, -29.43) * mm});
            skLineSegment(sketch, "E1312", {"start": v(39.08, -29.43) * mm, "end": v(39.2, -29.68) * mm});
            skLineSegment(sketch, "E1313", {"start": v(39.2, -29.68) * mm, "end": v(39.33, -29.93) * mm});
            skLineSegment(sketch, "E1314", {"start": v(39.33, -29.93) * mm, "end": v(39.5, -30.15) * mm});
            skLineSegment(sketch, "E1315", {"start": v(39.5, -30.15) * mm, "end": v(39.71, -30.34) * mm});
            skLineSegment(sketch, "E1316", {"start": v(49.71, -4.46) * mm, "end": v(49.63, -4.47) * mm});
            skLineSegment(sketch, "E1317", {"start": v(49.63, -4.47) * mm, "end": v(49.55, -4.49) * mm});
            skLineSegment(sketch, "E1318", {"start": v(49.55, -4.49) * mm, "end": v(49.47, -4.5) * mm});
            skLineSegment(sketch, "E1319", {"start": v(49.47, -4.5) * mm, "end": v(49.4, -4.51) * mm});
            skLineSegment(sketch, "E1320", {"start": v(49.4, -4.51) * mm, "end": v(49.4, -4.23) * mm});
            skLineSegment(sketch, "E1321", {"start": v(49.4, -4.23) * mm, "end": v(49.42, -3.97) * mm});
            skLineSegment(sketch, "E1322", {"start": v(49.42, -3.97) * mm, "end": v(49.39, -3.71) * mm});
            skLineSegment(sketch, "E1323", {"start": v(49.39, -3.71) * mm, "end": v(49.3, -3.47) * mm});
            skLineSegment(sketch, "E1324", {"start": v(49.3, -3.47) * mm, "end": v(49.23, -3.36) * mm});
            skLineSegment(sketch, "E1325", {"start": v(49.23, -3.36) * mm, "end": v(49.16, -3.25) * mm});
            skLineSegment(sketch, "E1326", {"start": v(49.16, -3.25) * mm, "end": v(49.1, -3.14) * mm});
            skLineSegment(sketch, "E1327", {"start": v(49.1, -3.14) * mm, "end": v(49, -3.05) * mm});
            skLineSegment(sketch, "E1328", {"start": v(49, -3.05) * mm, "end": v(48.82, -2.87) * mm});
            skLineSegment(sketch, "E1329", {"start": v(48.82, -2.87) * mm, "end": v(48.63, -2.68) * mm});
            skLineSegment(sketch, "E1330", {"start": v(48.63, -2.68) * mm, "end": v(48.46, -2.48) * mm});
            skLineSegment(sketch, "E1331", {"start": v(48.46, -2.48) * mm, "end": v(48.33, -2.24) * mm});
            skLineSegment(sketch, "E1332", {"start": v(48.33, -2.24) * mm, "end": v(48.28, -2.07) * mm});
            skLineSegment(sketch, "E1333", {"start": v(48.28, -2.07) * mm, "end": v(48.28, -1.9) * mm});
            skLineSegment(sketch, "E1334", {"start": v(48.28, -1.9) * mm, "end": v(48.33, -1.75) * mm});
            skLineSegment(sketch, "E1335", {"start": v(48.33, -1.75) * mm, "end": v(48.4, -1.6) * mm});
            skLineSegment(sketch, "E1336", {"start": v(48.4, -1.6) * mm, "end": v(48.63, -1.37) * mm});
            skLineSegment(sketch, "E1337", {"start": v(48.63, -1.37) * mm, "end": v(48.9, -1.28) * mm});
            skLineSegment(sketch, "E1338", {"start": v(48.9, -1.28) * mm, "end": v(49.19, -1.33) * mm});
            skLineSegment(sketch, "E1339", {"start": v(49.19, -1.33) * mm, "end": v(49.47, -1.5) * mm});
            skLineSegment(sketch, "E1340", {"start": v(49.47, -1.5) * mm, "end": v(49.58, -1.6) * mm});
            skLineSegment(sketch, "E1341", {"start": v(49.58, -1.6) * mm, "end": v(49.66, -1.72) * mm});
            skLineSegment(sketch, "E1342", {"start": v(49.66, -1.72) * mm, "end": v(49.7, -1.85) * mm});
            skLineSegment(sketch, "E1343", {"start": v(49.7, -1.85) * mm, "end": v(49.72, -2.02) * mm});
            skLineSegment(sketch, "E1344", {"start": v(49.72, -2.02) * mm, "end": v(49.71, -2.63) * mm});
            skLineSegment(sketch, "E1345", {"start": v(49.71, -2.63) * mm, "end": v(49.71, -3.23) * mm});
            skLineSegment(sketch, "E1346", {"start": v(49.71, -3.23) * mm, "end": v(49.71, -3.84) * mm});
            skLineSegment(sketch, "E1347", {"start": v(49.71, -3.84) * mm, "end": v(49.71, -4.46) * mm});
            skLineSegment(sketch, "E1348", {"start": v(44, 5.24) * mm, "end": v(44.1, 5.44) * mm});
            skLineSegment(sketch, "E1349", {"start": v(44.1, 5.44) * mm, "end": v(44.2, 5.63) * mm});
            skLineSegment(sketch, "E1350", {"start": v(44.2, 5.63) * mm, "end": v(44.28, 5.82) * mm});
            skLineSegment(sketch, "E1351", {"start": v(44.28, 5.82) * mm, "end": v(44.37, 6) * mm});
            skLineSegment(sketch, "E1352", {"start": v(44.37, 6) * mm, "end": v(44.55, 6.2) * mm});
            skLineSegment(sketch, "E1353", {"start": v(44.55, 6.2) * mm, "end": v(44.82, 6.38) * mm});
            skLineSegment(sketch, "E1354", {"start": v(44.82, 6.38) * mm, "end": v(45.12, 6.49) * mm});
            skLineSegment(sketch, "E1355", {"start": v(45.12, 6.49) * mm, "end": v(45.4, 6.5) * mm});
            skLineSegment(sketch, "E1356", {"start": v(45.4, 6.5) * mm, "end": v(45.58, 6.48) * mm});
            skLineSegment(sketch, "E1357", {"start": v(45.58, 6.48) * mm, "end": v(45.76, 6.46) * mm});
            skLineSegment(sketch, "E1358", {"start": v(45.76, 6.46) * mm, "end": v(45.93, 6.42) * mm});
            skLineSegment(sketch, "E1359", {"start": v(45.93, 6.42) * mm, "end": v(46.1, 6.35) * mm});
            skLineSegment(sketch, "E1360", {"start": v(46.1, 6.35) * mm, "end": v(46.3, 6.24) * mm});
            skLineSegment(sketch, "E1361", {"start": v(46.3, 6.24) * mm, "end": v(46.5, 6.12) * mm});
            skLineSegment(sketch, "E1362", {"start": v(46.5, 6.12) * mm, "end": v(46.68, 5.98) * mm});
            skLineSegment(sketch, "E1363", {"start": v(46.68, 5.98) * mm, "end": v(46.85, 5.83) * mm});
            skLineSegment(sketch, "E1364", {"start": v(46.85, 5.83) * mm, "end": v(46.92, 5.76) * mm});
            skLineSegment(sketch, "E1365", {"start": v(46.92, 5.76) * mm, "end": v(47, 5.68) * mm});
            skLineSegment(sketch, "E1366", {"start": v(47, 5.68) * mm, "end": v(47.08, 5.6) * mm});
            skLineSegment(sketch, "E1367", {"start": v(47.08, 5.6) * mm, "end": v(47.17, 5.52) * mm});
            skLineSegment(sketch, "E1368", {"start": v(47.17, 5.52) * mm, "end": v(46.36, 5.63) * mm});
            skLineSegment(sketch, "E1369", {"start": v(46.36, 5.63) * mm, "end": v(45.56, 5.6) * mm});
            skLineSegment(sketch, "E1370", {"start": v(45.56, 5.6) * mm, "end": v(44.78, 5.46) * mm});
            skLineSegment(sketch, "E1371", {"start": v(44.78, 5.46) * mm, "end": v(44, 5.24) * mm});
            skLineSegment(sketch, "E1372", {"start": v(36.72, 7.1) * mm, "end": v(37.26, 7.1) * mm});
            skLineSegment(sketch, "E1373", {"start": v(37.26, 7.1) * mm, "end": v(37.8, 7.1) * mm});
            skLineSegment(sketch, "E1374", {"start": v(37.8, 7.1) * mm, "end": v(38.34, 7.1) * mm});
            skLineSegment(sketch, "E1375", {"start": v(38.34, 7.1) * mm, "end": v(38.88, 7.1) * mm});
            skLineSegment(sketch, "E1376", {"start": v(38.88, 7.1) * mm, "end": v(38.5, 6.78) * mm});
            skLineSegment(sketch, "E1377", {"start": v(38.5, 6.78) * mm, "end": v(38.15, 6.43) * mm});
            skLineSegment(sketch, "E1378", {"start": v(38.15, 6.43) * mm, "end": v(37.83, 6.05) * mm});
            skLineSegment(sketch, "E1379", {"start": v(37.83, 6.05) * mm, "end": v(37.52, 5.64) * mm});
            skLineSegment(sketch, "E1380", {"start": v(37.52, 5.64) * mm, "end": v(37.42, 6.08) * mm});
            skLineSegment(sketch, "E1381", {"start": v(37.42, 6.08) * mm, "end": v(37.24, 6.45) * mm});
            skLineSegment(sketch, "E1382", {"start": v(37.24, 6.45) * mm, "end": v(37, 6.79) * mm});
            skLineSegment(sketch, "E1383", {"start": v(37, 6.79) * mm, "end": v(36.72, 7.1) * mm});
            skLineSegment(sketch, "E1384", {"start": v(29.66, -12.71) * mm, "end": v(29.45, -12.34) * mm});
            skLineSegment(sketch, "E1385", {"start": v(29.45, -12.34) * mm, "end": v(29.18, -12.02) * mm});
            skLineSegment(sketch, "E1386", {"start": v(29.18, -12.02) * mm, "end": v(28.86, -11.74) * mm});
            skLineSegment(sketch, "E1387", {"start": v(28.86, -11.74) * mm, "end": v(28.46, -11.52) * mm});
            skLineSegment(sketch, "E1388", {"start": v(28.46, -11.52) * mm, "end": v(28.87, -11.28) * mm});
            skLineSegment(sketch, "E1389", {"start": v(28.87, -11.28) * mm, "end": v(29.22, -11) * mm});
            skLineSegment(sketch, "E1390", {"start": v(29.22, -11) * mm, "end": v(29.5, -10.66) * mm});
            skLineSegment(sketch, "E1391", {"start": v(29.5, -10.66) * mm, "end": v(29.72, -10.27) * mm});
            skLineSegment(sketch, "E1392", {"start": v(29.72, -10.27) * mm, "end": v(29.74, -10.28) * mm});
            skLineSegment(sketch, "E1393", {"start": v(29.74, -10.28) * mm, "end": v(29.75, -10.28) * mm});
            skLineSegment(sketch, "E1394", {"start": v(29.75, -10.28) * mm, "end": v(29.77, -10.28) * mm});
            skLineSegment(sketch, "E1395", {"start": v(29.77, -10.28) * mm, "end": v(29.78, -10.28) * mm});
            skLineSegment(sketch, "E1396", {"start": v(29.78, -10.28) * mm, "end": v(29.76, -10.89) * mm});
            skLineSegment(sketch, "E1397", {"start": v(29.76, -10.89) * mm, "end": v(29.74, -11.49) * mm});
            skLineSegment(sketch, "E1398", {"start": v(29.74, -11.49) * mm, "end": v(29.72, -12.09) * mm});
            skLineSegment(sketch, "E1399", {"start": v(29.72, -12.09) * mm, "end": v(29.7, -12.69) * mm});
            skLineSegment(sketch, "E1400", {"start": v(29.7, -12.69) * mm, "end": v(29.7, -12.7) * mm});
            skLineSegment(sketch, "E1401", {"start": v(29.7, -12.7) * mm, "end": v(29.68, -12.7) * mm});
            skLineSegment(sketch, "E1402", {"start": v(29.68, -12.7) * mm, "end": v(29.67, -12.7) * mm});
            skLineSegment(sketch, "E1403", {"start": v(29.67, -12.7) * mm, "end": v(29.66, -12.71) * mm});
            skLineSegment(sketch, "E1404", {"start": v(47.87, -5.7) * mm, "end": v(47.5, -5.9) * mm});
            skLineSegment(sketch, "E1405", {"start": v(47.5, -5.9) * mm, "end": v(47.1, -5.94) * mm});
            skLineSegment(sketch, "E1406", {"start": v(47.1, -5.94) * mm, "end": v(46.7, -5.85) * mm});
            skLineSegment(sketch, "E1407", {"start": v(46.7, -5.85) * mm, "end": v(46.32, -5.63) * mm});
            skLineSegment(sketch, "E1408", {"start": v(46.32, -5.63) * mm, "end": v(45.97, -5.27) * mm});
            skLineSegment(sketch, "E1409", {"start": v(45.97, -5.27) * mm, "end": v(45.75, -4.85) * mm});
            skLineSegment(sketch, "E1410", {"start": v(45.75, -4.85) * mm, "end": v(45.61, -4.4) * mm});
            skLineSegment(sketch, "E1411", {"start": v(45.61, -4.4) * mm, "end": v(45.53, -3.9) * mm});
            skLineSegment(sketch, "E1412", {"start": v(45.53, -3.9) * mm, "end": v(45.53, -3.83) * mm});
            skLineSegment(sketch, "E1413", {"start": v(45.53, -3.83) * mm, "end": v(45.54, -3.74) * mm});
            skLineSegment(sketch, "E1414", {"start": v(45.54, -3.74) * mm, "end": v(45.56, -3.66) * mm});
            skLineSegment(sketch, "E1415", {"start": v(45.56, -3.66) * mm, "end": v(45.6, -3.57) * mm});
            skLineSegment(sketch, "E1416", {"start": v(45.6, -3.57) * mm, "end": v(45.63, -3.7) * mm});
            skLineSegment(sketch, "E1417", {"start": v(45.63, -3.7) * mm, "end": v(45.67, -3.82) * mm});
            skLineSegment(sketch, "E1418", {"start": v(45.67, -3.82) * mm, "end": v(45.7, -3.95) * mm});
            skLineSegment(sketch, "E1419", {"start": v(45.7, -3.95) * mm, "end": v(45.75, -4.07) * mm});
            skLineSegment(sketch, "E1420", {"start": v(45.75, -4.07) * mm, "end": v(45.9, -4.4) * mm});
            skLineSegment(sketch, "E1421", {"start": v(45.9, -4.4) * mm, "end": v(46.09, -4.73) * mm});
            skLineSegment(sketch, "E1422", {"start": v(46.09, -4.73) * mm, "end": v(46.3, -5.03) * mm});
            skLineSegment(sketch, "E1423", {"start": v(46.3, -5.03) * mm, "end": v(46.57, -5.3) * mm});
            skLineSegment(sketch, "E1424", {"start": v(46.57, -5.3) * mm, "end": v(46.82, -5.47) * mm});
            skLineSegment(sketch, "E1425", {"start": v(46.82, -5.47) * mm, "end": v(47.09, -5.58) * mm});
            skLineSegment(sketch, "E1426", {"start": v(47.09, -5.58) * mm, "end": v(47.38, -5.65) * mm});
            skLineSegment(sketch, "E1427", {"start": v(47.38, -5.65) * mm, "end": v(47.67, -5.68) * mm});
            skLineSegment(sketch, "E1428", {"start": v(47.67, -5.68) * mm, "end": v(47.72, -5.69) * mm});
            skLineSegment(sketch, "E1429", {"start": v(47.72, -5.69) * mm, "end": v(47.77, -5.7) * mm});
            skLineSegment(sketch, "E1430", {"start": v(47.77, -5.7) * mm, "end": v(47.82, -5.7) * mm});
            skLineSegment(sketch, "E1431", {"start": v(47.82, -5.7) * mm, "end": v(47.87, -5.7) * mm});
            skLineSegment(sketch, "E1432", {"start": v(26.78, -11.45) * mm, "end": v(26.65, -11.56) * mm});
            skLineSegment(sketch, "E1433", {"start": v(26.65, -11.56) * mm, "end": v(26.51, -11.67) * mm});
            skLineSegment(sketch, "E1434", {"start": v(26.51, -11.67) * mm, "end": v(26.37, -11.78) * mm});
            skLineSegment(sketch, "E1435", {"start": v(26.37, -11.78) * mm, "end": v(26.25, -11.9) * mm});
            skLineSegment(sketch, "E1436", {"start": v(26.25, -11.9) * mm, "end": v(26.14, -12.03) * mm});
            skLineSegment(sketch, "E1437", {"start": v(26.14, -12.03) * mm, "end": v(26.03, -12.17) * mm});
            skLineSegment(sketch, "E1438", {"start": v(26.03, -12.17) * mm, "end": v(25.93, -12.32) * mm});
            skLineSegment(sketch, "E1439", {"start": v(25.93, -12.32) * mm, "end": v(25.81, -12.48) * mm});
            skLineSegment(sketch, "E1440", {"start": v(25.81, -12.48) * mm, "end": v(25.81, -11.99) * mm});
            skLineSegment(sketch, "E1441", {"start": v(25.81, -11.99) * mm, "end": v(25.81, -11.5) * mm});
            skLineSegment(sketch, "E1442", {"start": v(25.81, -11.5) * mm, "end": v(25.81, -11.03) * mm});
            skLineSegment(sketch, "E1443", {"start": v(25.81, -11.03) * mm, "end": v(25.81, -10.56) * mm});
            skLineSegment(sketch, "E1444", {"start": v(25.81, -10.56) * mm, "end": v(25.82, -10.56) * mm});
            skLineSegment(sketch, "E1445", {"start": v(25.82, -10.56) * mm, "end": v(25.83, -10.55) * mm});
            skLineSegment(sketch, "E1446", {"start": v(25.83, -10.55) * mm, "end": v(25.85, -10.54) * mm});
            skLineSegment(sketch, "E1447", {"start": v(25.85, -10.54) * mm, "end": v(25.86, -10.54) * mm});
            skLineSegment(sketch, "E1448", {"start": v(25.86, -10.54) * mm, "end": v(26.05, -10.81) * mm});
            skLineSegment(sketch, "E1449", {"start": v(26.05, -10.81) * mm, "end": v(26.27, -11.07) * mm});
            skLineSegment(sketch, "E1450", {"start": v(26.27, -11.07) * mm, "end": v(26.5, -11.29) * mm});
            skLineSegment(sketch, "E1451", {"start": v(26.5, -11.29) * mm, "end": v(26.78, -11.45) * mm});
            skLineSegment(sketch, "E1452", {"start": v(25.83, -28.9) * mm, "end": v(26.09, -29.32) * mm});
            skLineSegment(sketch, "E1453", {"start": v(26.09, -29.32) * mm, "end": v(26.37, -29.72) * mm});
            skLineSegment(sketch, "E1454", {"start": v(26.37, -29.72) * mm, "end": v(26.7, -30.06) * mm});
            skLineSegment(sketch, "E1455", {"start": v(26.7, -30.06) * mm, "end": v(27.13, -30.32) * mm});
            skLineSegment(sketch, "E1456", {"start": v(27.13, -30.32) * mm, "end": v(27.13, -30.33) * mm});
            skLineSegment(sketch, "E1457", {"start": v(27.13, -30.33) * mm, "end": v(27.13, -30.35) * mm});
            skLineSegment(sketch, "E1458", {"start": v(27.13, -30.35) * mm, "end": v(27.12, -30.36) * mm});
            skLineSegment(sketch, "E1459", {"start": v(27.12, -30.36) * mm, "end": v(27.12, -30.38) * mm});
            skLineSegment(sketch, "E1460", {"start": v(27.12, -30.38) * mm, "end": v(26.85, -30.36) * mm});
            skLineSegment(sketch, "E1461", {"start": v(26.85, -30.36) * mm, "end": v(26.58, -30.35) * mm});
            skLineSegment(sketch, "E1462", {"start": v(26.58, -30.35) * mm, "end": v(26.32, -30.33) * mm});
            skLineSegment(sketch, "E1463", {"start": v(26.32, -30.33) * mm, "end": v(26.05, -30.3) * mm});
            skLineSegment(sketch, "E1464", {"start": v(26.05, -30.3) * mm, "end": v(25.94, -30.27) * mm});
            skLineSegment(sketch, "E1465", {"start": v(25.94, -30.27) * mm, "end": v(25.87, -30.2) * mm});
            skLineSegment(sketch, "E1466", {"start": v(25.87, -30.2) * mm, "end": v(25.84, -30.09) * mm});
            skLineSegment(sketch, "E1467", {"start": v(25.84, -30.09) * mm, "end": v(25.83, -29.97) * mm});
            skLineSegment(sketch, "E1468", {"start": v(25.83, -29.97) * mm, "end": v(25.83, -29.7) * mm});
            skLineSegment(sketch, "E1469", {"start": v(25.83, -29.7) * mm, "end": v(25.83, -29.45) * mm});
            skLineSegment(sketch, "E1470", {"start": v(25.83, -29.45) * mm, "end": v(25.83, -29.18) * mm});
            skLineSegment(sketch, "E1471", {"start": v(25.83, -29.18) * mm, "end": v(25.83, -28.9) * mm});
            skLineSegment(sketch, "E1472", {"start": v(31.6, -3.78) * mm, "end": v(31.6, -3.63) * mm});
            skLineSegment(sketch, "E1473", {"start": v(31.6, -3.63) * mm, "end": v(31.65, -3.47) * mm});
            skLineSegment(sketch, "E1474", {"start": v(31.65, -3.47) * mm, "end": v(31.75, -3.32) * mm});
            skLineSegment(sketch, "E1475", {"start": v(31.75, -3.32) * mm, "end": v(31.9, -3.19) * mm});
            skLineSegment(sketch, "E1476", {"start": v(31.9, -3.19) * mm, "end": v(32.02, -3.12) * mm});
            skLineSegment(sketch, "E1477", {"start": v(32.02, -3.12) * mm, "end": v(32.14, -3.1) * mm});
            skLineSegment(sketch, "E1478", {"start": v(32.14, -3.1) * mm, "end": v(32.26, -3.09) * mm});
            skLineSegment(sketch, "E1479", {"start": v(32.26, -3.09) * mm, "end": v(32.39, -3.1) * mm});
            skLineSegment(sketch, "E1480", {"start": v(32.39, -3.1) * mm, "end": v(32.46, -3.12) * mm});
            skLineSegment(sketch, "E1481", {"start": v(32.46, -3.12) * mm, "end": v(32.53, -3.15) * mm});
            skLineSegment(sketch, "E1482", {"start": v(32.53, -3.15) * mm, "end": v(32.62, -3.21) * mm});
            skLineSegment(sketch, "E1483", {"start": v(32.62, -3.21) * mm, "end": v(32.78, -3.34) * mm});
            skLineSegment(sketch, "E1484", {"start": v(32.78, -3.34) * mm, "end": v(32.48, -3.45) * mm});
            skLineSegment(sketch, "E1485", {"start": v(32.48, -3.45) * mm, "end": v(32.2, -3.56) * mm});
            skLineSegment(sketch, "E1486", {"start": v(32.2, -3.56) * mm, "end": v(31.9, -3.67) * mm});
            skLineSegment(sketch, "E1487", {"start": v(31.9, -3.67) * mm, "end": v(31.6, -3.78) * mm});
            skLineSegment(sketch, "E1488", {"start": v(49.7, 3.98) * mm, "end": v(49.55, 4.17) * mm});
            skLineSegment(sketch, "E1489", {"start": v(49.55, 4.17) * mm, "end": v(49.4, 4.35) * mm});
            skLineSegment(sketch, "E1490", {"start": v(49.4, 4.35) * mm, "end": v(49.24, 4.53) * mm});
            skLineSegment(sketch, "E1491", {"start": v(49.24, 4.53) * mm, "end": v(49.08, 4.72) * mm});
            skLineSegment(sketch, "E1492", {"start": v(49.08, 4.72) * mm, "end": v(49.16, 4.75) * mm});
            skLineSegment(sketch, "E1493", {"start": v(49.16, 4.75) * mm, "end": v(49.23, 4.78) * mm});
            skLineSegment(sketch, "E1494", {"start": v(49.23, 4.78) * mm, "end": v(49.3, 4.8) * mm});
            skLineSegment(sketch, "E1495", {"start": v(49.3, 4.8) * mm, "end": v(49.38, 4.84) * mm});
            skLineSegment(sketch, "E1496", {"start": v(49.38, 4.84) * mm, "end": v(49.42, 4.86) * mm});
            skLineSegment(sketch, "E1497", {"start": v(49.42, 4.86) * mm, "end": v(49.46, 4.88) * mm});
            skLineSegment(sketch, "E1498", {"start": v(49.46, 4.88) * mm, "end": v(49.5, 4.9) * mm});
            skLineSegment(sketch, "E1499", {"start": v(49.5, 4.9) * mm, "end": v(49.54, 4.93) * mm});
            skLineSegment(sketch, "E1500", {"start": v(49.54, 4.93) * mm, "end": v(49.6, 4.97) * mm});
            skLineSegment(sketch, "E1501", {"start": v(49.6, 4.97) * mm, "end": v(49.65, 4.98) * mm});
            skLineSegment(sketch, "E1502", {"start": v(49.65, 4.98) * mm, "end": v(49.69, 4.96) * mm});
            skLineSegment(sketch, "E1503", {"start": v(49.69, 4.96) * mm, "end": v(49.7, 4.9) * mm});
            skLineSegment(sketch, "E1504", {"start": v(49.7, 4.9) * mm, "end": v(49.71, 4.67) * mm});
            skLineSegment(sketch, "E1505", {"start": v(49.71, 4.67) * mm, "end": v(49.71, 4.44) * mm});
            skLineSegment(sketch, "E1506", {"start": v(49.71, 4.44) * mm, "end": v(49.71, 4.21) * mm});
            skLineSegment(sketch, "E1507", {"start": v(49.71, 4.21) * mm, "end": v(49.7, 3.98) * mm});
            skLineSegment(sketch, "E1508", {"start": v(25.82, 6.17) * mm, "end": v(25.83, 6.36) * mm});
            skLineSegment(sketch, "E1509", {"start": v(25.83, 6.36) * mm, "end": v(25.84, 6.53) * mm});
            skLineSegment(sketch, "E1510", {"start": v(25.84, 6.53) * mm, "end": v(25.85, 6.7) * mm});
            skLineSegment(sketch, "E1511", {"start": v(25.85, 6.7) * mm, "end": v(25.88, 6.85) * mm});
            skLineSegment(sketch, "E1512", {"start": v(25.88, 6.85) * mm, "end": v(25.91, 6.92) * mm});
            skLineSegment(sketch, "E1513", {"start": v(25.91, 6.92) * mm, "end": v(25.97, 6.98) * mm});
            skLineSegment(sketch, "E1514", {"start": v(25.97, 6.98) * mm, "end": v(26.05, 7.03) * mm});
            skLineSegment(sketch, "E1515", {"start": v(26.05, 7.03) * mm, "end": v(26.13, 7.06) * mm});
            skLineSegment(sketch, "E1516", {"start": v(26.13, 7.06) * mm, "end": v(26.24, 7.08) * mm});
            skLineSegment(sketch, "E1517", {"start": v(26.24, 7.08) * mm, "end": v(26.35, 7.1) * mm});
            skLineSegment(sketch, "E1518", {"start": v(26.35, 7.1) * mm, "end": v(26.48, 7.1) * mm});
            skLineSegment(sketch, "E1519", {"start": v(26.48, 7.1) * mm, "end": v(26.62, 7.11) * mm});
            skLineSegment(sketch, "E1520", {"start": v(26.62, 7.11) * mm, "end": v(26.42, 6.87) * mm});
            skLineSegment(sketch, "E1521", {"start": v(26.42, 6.87) * mm, "end": v(26.22, 6.64) * mm});
            skLineSegment(sketch, "E1522", {"start": v(26.22, 6.64) * mm, "end": v(26.02, 6.4) * mm});
            skLineSegment(sketch, "E1523", {"start": v(26.02, 6.4) * mm, "end": v(25.82, 6.17) * mm});
            skLineSegment(sketch, "E1524", {"start": v(27.55, 3.17) * mm, "end": v(27.32, 3.19) * mm});
            skLineSegment(sketch, "E1525", {"start": v(27.32, 3.19) * mm, "end": v(27.2, 3.32) * mm});
            skLineSegment(sketch, "E1526", {"start": v(27.2, 3.32) * mm, "end": v(27.1, 3.49) * mm});
            skLineSegment(sketch, "E1527", {"start": v(27.1, 3.49) * mm, "end": v(26.98, 3.64) * mm});
            skLineSegment(sketch, "E1528", {"start": v(26.98, 3.64) * mm, "end": v(27.18, 3.68) * mm});
            skLineSegment(sketch, "E1529", {"start": v(27.18, 3.68) * mm, "end": v(27.36, 3.6) * mm});
            skLineSegment(sketch, "E1530", {"start": v(27.36, 3.6) * mm, "end": v(27.5, 3.43) * mm});
            skLineSegment(sketch, "E1531", {"start": v(27.5, 3.43) * mm, "end": v(27.55, 3.17) * mm});
            skLineSegment(sketch, "E1532", {"start": v(31.44, -0.6) * mm, "end": v(31.53, -0.7) * mm});
            skLineSegment(sketch, "E1533", {"start": v(31.53, -0.7) * mm, "end": v(31.63, -0.77) * mm});
            skLineSegment(sketch, "E1534", {"start": v(31.63, -0.77) * mm, "end": v(31.72, -0.87) * mm});
            skLineSegment(sketch, "E1535", {"start": v(31.72, -0.87) * mm, "end": v(31.75, -1.02) * mm});
            skLineSegment(sketch, "E1536", {"start": v(31.75, -1.02) * mm, "end": v(31.6, -1.03) * mm});
            skLineSegment(sketch, "E1537", {"start": v(31.6, -1.03) * mm, "end": v(31.5, -0.98) * mm});
            skLineSegment(sketch, "E1538", {"start": v(31.5, -0.98) * mm, "end": v(31.43, -0.88) * mm});
            skLineSegment(sketch, "E1539", {"start": v(31.43, -0.88) * mm, "end": v(31.35, -0.79) * mm});
            skLineSegment(sketch, "E1540", {"start": v(31.35, -0.79) * mm, "end": v(31.34, -0.76) * mm});
            skLineSegment(sketch, "E1541", {"start": v(31.34, -0.76) * mm, "end": v(31.35, -0.71) * mm});
            skLineSegment(sketch, "E1542", {"start": v(31.35, -0.71) * mm, "end": v(31.37, -0.66) * mm});
            skLineSegment(sketch, "E1543", {"start": v(31.37, -0.66) * mm, "end": v(31.39, -0.6) * mm});
            skLineSegment(sketch, "E1544", {"start": v(31.39, -0.6) * mm, "end": v(31.4, -0.6) * mm});
            skLineSegment(sketch, "E1545", {"start": v(31.4, -0.6) * mm, "end": v(31.42, -0.6) * mm});
            skLineSegment(sketch, "E1546", {"start": v(31.42, -0.6) * mm, "end": v(31.43, -0.6) * mm});
            skLineSegment(sketch, "E1547", {"start": v(31.43, -0.6) * mm, "end": v(31.44, -0.6) * mm});
            skLineSegment(sketch, "E1548", {"start": v(36, 0.63) * mm, "end": v(35.87, 0.48) * mm});
            skLineSegment(sketch, "E1549", {"start": v(35.87, 0.48) * mm, "end": v(35.73, 0.32) * mm});
            skLineSegment(sketch, "E1550", {"start": v(35.73, 0.32) * mm, "end": v(35.59, 0.18) * mm});
            skLineSegment(sketch, "E1551", {"start": v(35.59, 0.18) * mm, "end": v(35.42, 0.06) * mm});
            skLineSegment(sketch, "E1552", {"start": v(35.42, 0.06) * mm, "end": v(35.5, 0.22) * mm});
            skLineSegment(sketch, "E1553", {"start": v(35.5, 0.22) * mm, "end": v(35.65, 0.4) * mm});
            skLineSegment(sketch, "E1554", {"start": v(35.65, 0.4) * mm, "end": v(35.85, 0.56) * mm});
            skLineSegment(sketch, "E1555", {"start": v(35.85, 0.56) * mm, "end": v(36, 0.63) * mm});
            skLineSegment(sketch, "E1556", {"start": v(28.76, 1.79) * mm, "end": v(28.83, 1.83) * mm});
            skLineSegment(sketch, "E1557", {"start": v(28.83, 1.83) * mm, "end": v(28.9, 1.88) * mm});
            skLineSegment(sketch, "E1558", {"start": v(28.9, 1.88) * mm, "end": v(28.97, 1.92) * mm});
            skLineSegment(sketch, "E1559", {"start": v(28.97, 1.92) * mm, "end": v(29.04, 1.97) * mm});
            skLineSegment(sketch, "E1560", {"start": v(29.04, 1.97) * mm, "end": v(29.06, 1.94) * mm});
            skLineSegment(sketch, "E1561", {"start": v(29.06, 1.94) * mm, "end": v(29.08, 1.9) * mm});
            skLineSegment(sketch, "E1562", {"start": v(29.08, 1.9) * mm, "end": v(29.1, 1.87) * mm});
            skLineSegment(sketch, "E1563", {"start": v(29.1, 1.87) * mm, "end": v(29.1, 1.85) * mm});
            skLineSegment(sketch, "E1564", {"start": v(29.1, 1.85) * mm, "end": v(29.08, 1.8) * mm});
            skLineSegment(sketch, "E1565", {"start": v(29.08, 1.8) * mm, "end": v(29.05, 1.75) * mm});
            skLineSegment(sketch, "E1566", {"start": v(29.05, 1.75) * mm, "end": v(29.02, 1.7) * mm});
            skLineSegment(sketch, "E1567", {"start": v(29.02, 1.7) * mm, "end": v(28.98, 1.68) * mm});
            skLineSegment(sketch, "E1568", {"start": v(28.98, 1.68) * mm, "end": v(28.94, 1.67) * mm});
            skLineSegment(sketch, "E1569", {"start": v(28.94, 1.67) * mm, "end": v(28.89, 1.67) * mm});
            skLineSegment(sketch, "E1570", {"start": v(28.89, 1.67) * mm, "end": v(28.83, 1.68) * mm});
            skLineSegment(sketch, "E1571", {"start": v(28.83, 1.68) * mm, "end": v(28.78, 1.7) * mm});
            skLineSegment(sketch, "E1572", {"start": v(28.78, 1.7) * mm, "end": v(28.77, 1.72) * mm});
            skLineSegment(sketch, "E1573", {"start": v(28.77, 1.72) * mm, "end": v(28.77, 1.74) * mm});
            skLineSegment(sketch, "E1574", {"start": v(28.77, 1.74) * mm, "end": v(28.76, 1.76) * mm});
            skLineSegment(sketch, "E1575", {"start": v(28.76, 1.76) * mm, "end": v(28.76, 1.79) * mm});
            skLineSegment(sketch, "E1576", {"start": v(36.49, 1.4) * mm, "end": v(36.44, 1.3) * mm});
            skLineSegment(sketch, "E1577", {"start": v(36.44, 1.3) * mm, "end": v(36.4, 1.21) * mm});
            skLineSegment(sketch, "E1578", {"start": v(36.4, 1.21) * mm, "end": v(36.35, 1.13) * mm});
            skLineSegment(sketch, "E1579", {"start": v(36.35, 1.13) * mm, "end": v(36.3, 1.04) * mm});
            skLineSegment(sketch, "E1580", {"start": v(36.3, 1.04) * mm, "end": v(36.28, 1.04) * mm});
            skLineSegment(sketch, "E1581", {"start": v(36.28, 1.04) * mm, "end": v(36.27, 1.04) * mm});
            skLineSegment(sketch, "E1582", {"start": v(36.27, 1.04) * mm, "end": v(36.25, 1.04) * mm});
            skLineSegment(sketch, "E1583", {"start": v(36.25, 1.04) * mm, "end": v(36.24, 1.04) * mm});
            skLineSegment(sketch, "E1584", {"start": v(36.24, 1.04) * mm, "end": v(36.23, 1.1) * mm});
            skLineSegment(sketch, "E1585", {"start": v(36.23, 1.1) * mm, "end": v(36.22, 1.16) * mm});
            skLineSegment(sketch, "E1586", {"start": v(36.22, 1.16) * mm, "end": v(36.22, 1.2) * mm});
            skLineSegment(sketch, "E1587", {"start": v(36.22, 1.2) * mm, "end": v(36.23, 1.26) * mm});
            skLineSegment(sketch, "E1588", {"start": v(36.23, 1.26) * mm, "end": v(36.26, 1.31) * mm});
            skLineSegment(sketch, "E1589", {"start": v(36.26, 1.31) * mm, "end": v(36.31, 1.36) * mm});
            skLineSegment(sketch, "E1590", {"start": v(36.31, 1.36) * mm, "end": v(36.36, 1.4) * mm});
            skLineSegment(sketch, "E1591", {"start": v(36.36, 1.4) * mm, "end": v(36.41, 1.45) * mm});
            skLineSegment(sketch, "E1592", {"start": v(36.41, 1.45) * mm, "end": v(36.43, 1.44) * mm});
            skLineSegment(sketch, "E1593", {"start": v(36.43, 1.44) * mm, "end": v(36.45, 1.42) * mm});
            skLineSegment(sketch, "E1594", {"start": v(36.45, 1.42) * mm, "end": v(36.47, 1.4) * mm});
            skLineSegment(sketch, "E1595", {"start": v(36.47, 1.4) * mm, "end": v(36.49, 1.4) * mm});
            skLineSegment(sketch, "E1596", {"start": v(28.85, -2.73) * mm, "end": v(28.9, -2.65) * mm});
            skLineSegment(sketch, "E1597", {"start": v(28.9, -2.65) * mm, "end": v(28.95, -2.58) * mm});
            skLineSegment(sketch, "E1598", {"start": v(28.95, -2.58) * mm, "end": v(29, -2.5) * mm});
            skLineSegment(sketch, "E1599", {"start": v(29, -2.5) * mm, "end": v(29.06, -2.41) * mm});
            skLineSegment(sketch, "E1600", {"start": v(29.06, -2.41) * mm, "end": v(29.1, -2.47) * mm});
            skLineSegment(sketch, "E1601", {"start": v(29.1, -2.47) * mm, "end": v(29.14, -2.52) * mm});
            skLineSegment(sketch, "E1602", {"start": v(29.14, -2.52) * mm, "end": v(29.17, -2.58) * mm});
            skLineSegment(sketch, "E1603", {"start": v(29.17, -2.58) * mm, "end": v(29.21, -2.63) * mm});
            skLineSegment(sketch, "E1604", {"start": v(29.21, -2.63) * mm, "end": v(29.13, -2.67) * mm});
            skLineSegment(sketch, "E1605", {"start": v(29.13, -2.67) * mm, "end": v(29.05, -2.71) * mm});
            skLineSegment(sketch, "E1606", {"start": v(29.05, -2.71) * mm, "end": v(28.97, -2.75) * mm});
            skLineSegment(sketch, "E1607", {"start": v(28.97, -2.75) * mm, "end": v(28.9, -2.78) * mm});
            skLineSegment(sketch, "E1608", {"start": v(28.9, -2.78) * mm, "end": v(28.89, -2.77) * mm});
            skLineSegment(sketch, "E1609", {"start": v(28.89, -2.77) * mm, "end": v(28.88, -2.75) * mm});
            skLineSegment(sketch, "E1610", {"start": v(28.88, -2.75) * mm, "end": v(28.86, -2.74) * mm});
            skLineSegment(sketch, "E1611", {"start": v(28.86, -2.74) * mm, "end": v(28.85, -2.73) * mm});
            skLineSegment(sketch, "E1612", {"start": v(29.34, -5.58) * mm, "end": v(29.37, -5.52) * mm});
            skLineSegment(sketch, "E1613", {"start": v(29.37, -5.52) * mm, "end": v(29.39, -5.47) * mm});
            skLineSegment(sketch, "E1614", {"start": v(29.39, -5.47) * mm, "end": v(29.41, -5.4) * mm});
            skLineSegment(sketch, "E1615", {"start": v(29.41, -5.4) * mm, "end": v(29.44, -5.36) * mm});
            skLineSegment(sketch, "E1616", {"start": v(29.44, -5.36) * mm, "end": v(29.46, -5.34) * mm});
            skLineSegment(sketch, "E1617", {"start": v(29.46, -5.34) * mm, "end": v(29.5, -5.33) * mm});
            skLineSegment(sketch, "E1618", {"start": v(29.5, -5.33) * mm, "end": v(29.54, -5.32) * mm});
            skLineSegment(sketch, "E1619", {"start": v(29.54, -5.32) * mm, "end": v(29.58, -5.31) * mm});
            skLineSegment(sketch, "E1620", {"start": v(29.58, -5.31) * mm, "end": v(29.59, -5.36) * mm});
            skLineSegment(sketch, "E1621", {"start": v(29.59, -5.36) * mm, "end": v(29.6, -5.41) * mm});
            skLineSegment(sketch, "E1622", {"start": v(29.6, -5.41) * mm, "end": v(29.6, -5.46) * mm});
            skLineSegment(sketch, "E1623", {"start": v(29.6, -5.46) * mm, "end": v(29.6, -5.49) * mm});
            skLineSegment(sketch, "E1624", {"start": v(29.6, -5.49) * mm, "end": v(29.55, -5.53) * mm});
            skLineSegment(sketch, "E1625", {"start": v(29.55, -5.53) * mm, "end": v(29.5, -5.56) * mm});
            skLineSegment(sketch, "E1626", {"start": v(29.5, -5.56) * mm, "end": v(29.44, -5.6) * mm});
            skLineSegment(sketch, "E1627", {"start": v(29.44, -5.6) * mm, "end": v(29.39, -5.62) * mm});
            skLineSegment(sketch, "E1628", {"start": v(29.39, -5.62) * mm, "end": v(29.38, -5.61) * mm});
            skLineSegment(sketch, "E1629", {"start": v(29.38, -5.61) * mm, "end": v(29.36, -5.6) * mm});
            skLineSegment(sketch, "E1630", {"start": v(29.36, -5.6) * mm, "end": v(29.35, -5.6) * mm});
            skLineSegment(sketch, "E1631", {"start": v(29.35, -5.6) * mm, "end": v(29.34, -5.58) * mm});
            skLineSegment(sketch, "E1632", {"start": v(28.24, -3.99) * mm, "end": v(28.27, -3.94) * mm});
            skLineSegment(sketch, "E1633", {"start": v(28.27, -3.94) * mm, "end": v(28.29, -3.89) * mm});
            skLineSegment(sketch, "E1634", {"start": v(28.29, -3.89) * mm, "end": v(28.31, -3.84) * mm});
            skLineSegment(sketch, "E1635", {"start": v(28.31, -3.84) * mm, "end": v(28.34, -3.8) * mm});
            skLineSegment(sketch, "E1636", {"start": v(28.34, -3.8) * mm, "end": v(28.36, -3.8) * mm});
            skLineSegment(sketch, "E1637", {"start": v(28.36, -3.8) * mm, "end": v(28.39, -3.82) * mm});
            skLineSegment(sketch, "E1638", {"start": v(28.39, -3.82) * mm, "end": v(28.41, -3.83) * mm});
            skLineSegment(sketch, "E1639", {"start": v(28.41, -3.83) * mm, "end": v(28.44, -3.84) * mm});
            skLineSegment(sketch, "E1640", {"start": v(28.44, -3.84) * mm, "end": v(28.4, -3.9) * mm});
            skLineSegment(sketch, "E1641", {"start": v(28.4, -3.9) * mm, "end": v(28.38, -3.94) * mm});
            skLineSegment(sketch, "E1642", {"start": v(28.38, -3.94) * mm, "end": v(28.36, -3.99) * mm});
            skLineSegment(sketch, "E1643", {"start": v(28.36, -3.99) * mm, "end": v(28.33, -4.03) * mm});
            skLineSegment(sketch, "E1644", {"start": v(28.33, -4.03) * mm, "end": v(28.3, -4.02) * mm});
            skLineSegment(sketch, "E1645", {"start": v(28.3, -4.02) * mm, "end": v(28.29, -4.01) * mm});
            skLineSegment(sketch, "E1646", {"start": v(28.29, -4.01) * mm, "end": v(28.26, -4) * mm});
            skLineSegment(sketch, "E1647", {"start": v(28.26, -4) * mm, "end": v(28.24, -3.99) * mm});
            skSolve(sketch);
        }
        {
            var Q0;
            Q0 = qSketchRegion(id + "F2", true);
            extrude(context, id + "F3", {"entities" : qUnion([Q0]), "operationType" : NewBodyOperationType.REMOVE, "oppositeDirection" : true, "depth" : 1 / 101.6 * mm, "offsetDistance" : 25 * mm});
        }
    });
